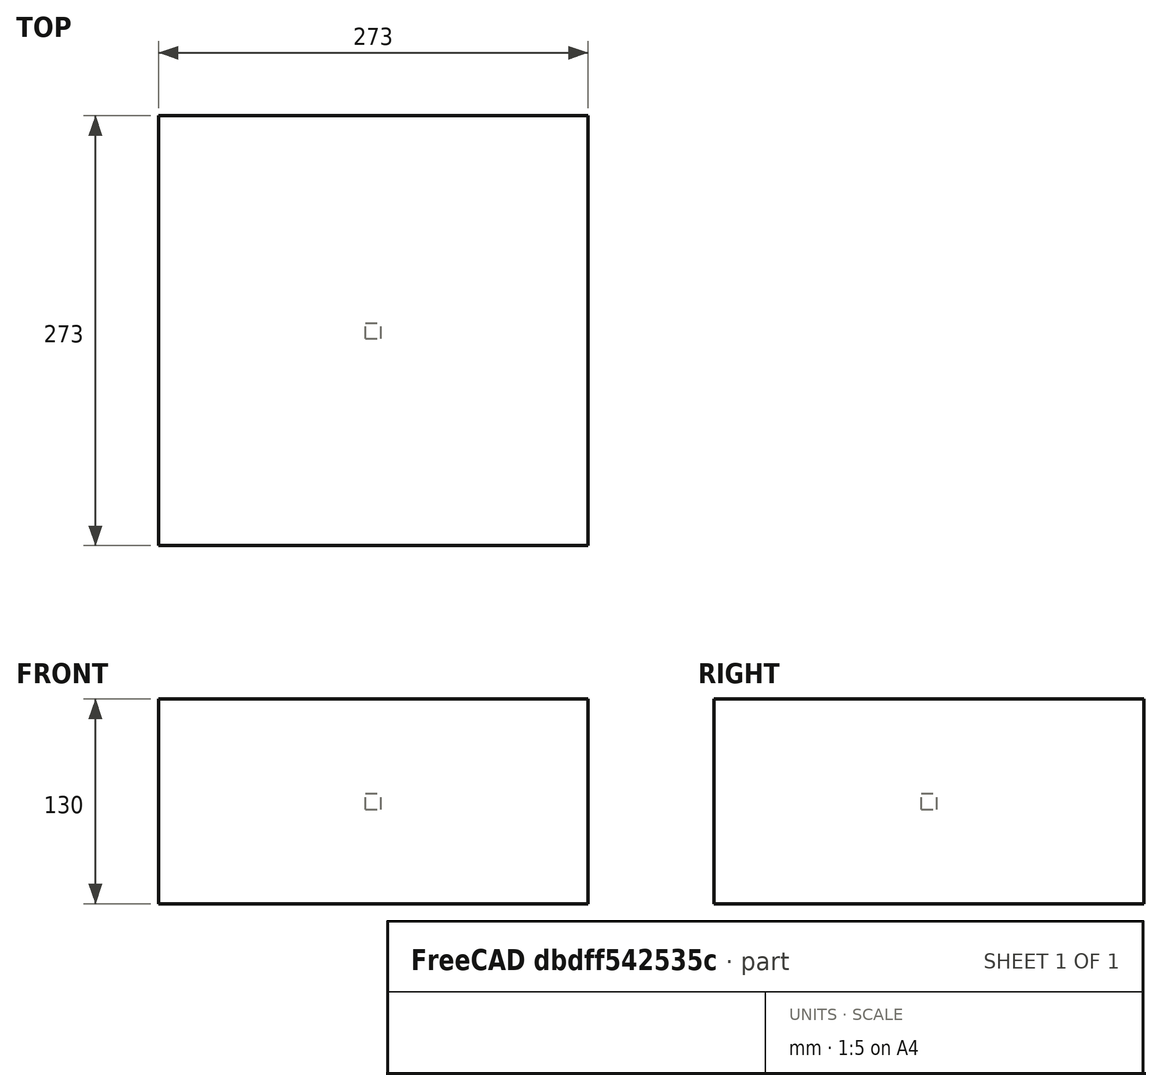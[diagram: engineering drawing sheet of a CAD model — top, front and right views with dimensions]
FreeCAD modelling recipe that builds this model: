
FCSTD DOCUMENT  (FreeCAD 0.20R29603 (Git))
Label: polarArray
License: All rights reserved
LicenseURL: http://en.wikipedia.org/wiki/All_rights_reserved
objects: App::DocumentObjectGroupPython×1251, Part::FeaturePython×3, App::Part×3
note: 2 computed .brp shape members not serialized (recipe doc carries the construction recipe); baked Part::Feature solids carry a one-line shape summary decoded from their .brp

FEATURE [App::DocumentObjectGroupPython] HALFPI  # scripted group (container) (typed FeaturePython)
  name = HALFPI
  value = pi/2.
FEATURE [App::DocumentObjectGroupPython] PI  # scripted group (container) (typed FeaturePython)
  name = PI
  value = 1.*pi
FEATURE [App::DocumentObjectGroupPython] TWOPI  # scripted group (container) (typed FeaturePython)
  name = TWOPI
  value = 2.*pi
FEATURE [App::DocumentObjectGroupPython] Constants  # scripted group (container) (typed FeaturePython)
  Group = -> [HALFPI,PI,TWOPI]
FEATURE [App::DocumentObjectGroupPython] Variables  # scripted group (container) (typed FeaturePython)
FEATURE [App::DocumentObjectGroupPython] Quantities  # scripted group (container) (typed FeaturePython)
FEATURE [App::DocumentObjectGroupPython] Isotopes  # scripted group (container) (typed FeaturePython)
FEATURE [App::DocumentObjectGroupPython] Elements  # scripted group (container) (typed FeaturePython)
FEATURE [App::DocumentObjectGroupPython] Matrix  # scripted group (container) (typed FeaturePython)
FEATURE [App::DocumentObjectGroupPython] Surfaces  # scripted group (container) (typed FeaturePython)
FEATURE [App::DocumentObjectGroupPython] Opticals  # scripted group (container) (typed FeaturePython)
  Group = -> [Matrix,Surfaces]
FEATURE [App::DocumentObjectGroupPython] G4Isotopes  # scripted group (container) (typed FeaturePython)
FEATURE [App::DocumentObjectGroupPython] H_element  # scripted group (container) (typed FeaturePython)
  Z = 1
  atom_value = 1.008
  formula = H
  name = H_element
FEATURE [App::DocumentObjectGroupPython] He_element  # scripted group (container) (typed FeaturePython)
  Z = 2
  atom_value = 4.0026
  formula = He
  name = He_element
FEATURE [App::DocumentObjectGroupPython] Li_element  # scripted group (container) (typed FeaturePython)
  Z = 3
  atom_value = 6.94
  formula = Li
  name = Li_element
FEATURE [App::DocumentObjectGroupPython] Be_element  # scripted group (container) (typed FeaturePython)
  Z = 4
  atom_value = 9.01218
  formula = Be
  name = Be_element
FEATURE [App::DocumentObjectGroupPython] B_element  # scripted group (container) (typed FeaturePython)
  Z = 5
  atom_value = 10.81
  formula = B
  name = B_element
FEATURE [App::DocumentObjectGroupPython] C_element  # scripted group (container) (typed FeaturePython)
  Z = 6
  atom_value = 12.011
  formula = C
  name = C_element
FEATURE [App::DocumentObjectGroupPython] N_element  # scripted group (container) (typed FeaturePython)
  Z = 7
  atom_value = 14.007
  formula = N
  name = N_element
FEATURE [App::DocumentObjectGroupPython] O_element  # scripted group (container) (typed FeaturePython)
  Z = 8
  atom_value = 15.999
  formula = O
  name = O_element
FEATURE [App::DocumentObjectGroupPython] F_element  # scripted group (container) (typed FeaturePython)
  Z = 9
  atom_value = 18.9984
  formula = F
  name = F_element
FEATURE [App::DocumentObjectGroupPython] Ne_element  # scripted group (container) (typed FeaturePython)
  Z = 10
  atom_value = 20.1797
  formula = Ne
  name = Ne_element
FEATURE [App::DocumentObjectGroupPython] Na_element  # scripted group (container) (typed FeaturePython)
  Z = 11
  atom_value = 22.9898
  formula = Na
  name = Na_element
FEATURE [App::DocumentObjectGroupPython] Mg_element  # scripted group (container) (typed FeaturePython)
  Z = 12
  atom_value = 24.305
  formula = Mg
  name = Mg_element
FEATURE [App::DocumentObjectGroupPython] Al_element  # scripted group (container) (typed FeaturePython)
  Z = 13
  atom_value = 26.9815
  formula = Al
  name = Al_element
FEATURE [App::DocumentObjectGroupPython] Si_element  # scripted group (container) (typed FeaturePython)
  Z = 14
  atom_value = 28.085
  formula = Si
  name = Si_element
FEATURE [App::DocumentObjectGroupPython] P_element  # scripted group (container) (typed FeaturePython)
  Z = 15
  atom_value = 30.9738
  formula = P
  name = P_element
FEATURE [App::DocumentObjectGroupPython] S_element  # scripted group (container) (typed FeaturePython)
  Z = 16
  atom_value = 32.06
  formula = S
  name = S_element
FEATURE [App::DocumentObjectGroupPython] Cl_element  # scripted group (container) (typed FeaturePython)
  Z = 17
  atom_value = 35.45
  formula = Cl
  name = Cl_element
FEATURE [App::DocumentObjectGroupPython] Ar_element  # scripted group (container) (typed FeaturePython)
  Z = 18
  atom_value = 39.95
  formula = Ar
  name = Ar_element
FEATURE [App::DocumentObjectGroupPython] K_element  # scripted group (container) (typed FeaturePython)
  Z = 19
  atom_value = 39.0983
  formula = K
  name = K_element
FEATURE [App::DocumentObjectGroupPython] Ca_element  # scripted group (container) (typed FeaturePython)
  Z = 20
  atom_value = 40.078
  formula = Ca
  name = Ca_element
FEATURE [App::DocumentObjectGroupPython] Sc_element  # scripted group (container) (typed FeaturePython)
  Z = 21
  atom_value = 44.9559
  formula = Sc
  name = Sc_element
FEATURE [App::DocumentObjectGroupPython] Ti_element  # scripted group (container) (typed FeaturePython)
  Z = 22
  atom_value = 47.867
  formula = Ti
  name = Ti_element
FEATURE [App::DocumentObjectGroupPython] V_element  # scripted group (container) (typed FeaturePython)
  Z = 23
  atom_value = 50.9415
  formula = V
  name = V_element
FEATURE [App::DocumentObjectGroupPython] Cr_element  # scripted group (container) (typed FeaturePython)
  Z = 24
  atom_value = 51.9961
  formula = Cr
  name = Cr_element
FEATURE [App::DocumentObjectGroupPython] Mn_element  # scripted group (container) (typed FeaturePython)
  Z = 25
  atom_value = 54.938
  formula = Mn
  name = Mn_element
FEATURE [App::DocumentObjectGroupPython] Fe_element  # scripted group (container) (typed FeaturePython)
  Z = 26
  atom_value = 55.845
  formula = Fe
  name = Fe_element
FEATURE [App::DocumentObjectGroupPython] Co_element  # scripted group (container) (typed FeaturePython)
  Z = 27
  atom_value = 58.9332
  formula = Co
  name = Co_element
FEATURE [App::DocumentObjectGroupPython] Ni_element  # scripted group (container) (typed FeaturePython)
  Z = 28
  atom_value = 58.6934
  formula = Ni
  name = Ni_element
FEATURE [App::DocumentObjectGroupPython] Cu_element  # scripted group (container) (typed FeaturePython)
  Z = 29
  atom_value = 63.546
  formula = Cu
  name = Cu_element
FEATURE [App::DocumentObjectGroupPython] Zn_element  # scripted group (container) (typed FeaturePython)
  Z = 30
  atom_value = 65.38
  formula = Zn
  name = Zn_element
FEATURE [App::DocumentObjectGroupPython] Ga_element  # scripted group (container) (typed FeaturePython)
  Z = 31
  atom_value = 69.723
  formula = Ga
  name = Ga_element
FEATURE [App::DocumentObjectGroupPython] Ge_element  # scripted group (container) (typed FeaturePython)
  Z = 32
  atom_value = 72.63
  formula = Ge
  name = Ge_element
FEATURE [App::DocumentObjectGroupPython] As_element  # scripted group (container) (typed FeaturePython)
  Z = 33
  atom_value = 74.9216
  formula = As
  name = As_element
FEATURE [App::DocumentObjectGroupPython] Se_element  # scripted group (container) (typed FeaturePython)
  Z = 34
  atom_value = 78.971
  formula = Se
  name = Se_element
FEATURE [App::DocumentObjectGroupPython] Br_element  # scripted group (container) (typed FeaturePython)
  Z = 35
  atom_value = 79.904
  formula = Br
  name = Br_element
FEATURE [App::DocumentObjectGroupPython] Kr_element  # scripted group (container) (typed FeaturePython)
  Z = 36
  atom_value = 83.798
  formula = Kr
  name = Kr_element
FEATURE [App::DocumentObjectGroupPython] Rb_element  # scripted group (container) (typed FeaturePython)
  Z = 37
  atom_value = 85.4678
  formula = Rb
  name = Rb_element
FEATURE [App::DocumentObjectGroupPython] Sr_element  # scripted group (container) (typed FeaturePython)
  Z = 38
  atom_value = 87.62
  formula = Sr
  name = Sr_element
FEATURE [App::DocumentObjectGroupPython] Y_element  # scripted group (container) (typed FeaturePython)
  Z = 39
  atom_value = 88.9058
  formula = Y
  name = Y_element
FEATURE [App::DocumentObjectGroupPython] Zr_element  # scripted group (container) (typed FeaturePython)
  Z = 40
  atom_value = 91.224
  formula = Zr
  name = Zr_element
FEATURE [App::DocumentObjectGroupPython] Nb_element  # scripted group (container) (typed FeaturePython)
  Z = 41
  atom_value = 92.9064
  formula = Nb
  name = Nb_element
FEATURE [App::DocumentObjectGroupPython] Mo_element  # scripted group (container) (typed FeaturePython)
  Z = 42
  atom_value = 95.95
  formula = Mo
  name = Mo_element
FEATURE [App::DocumentObjectGroupPython] Tc_element  # scripted group (container) (typed FeaturePython)
  Z = 43
  atom_value = 97
  formula = Tc
  name = Tc_element
FEATURE [App::DocumentObjectGroupPython] Ru_element  # scripted group (container) (typed FeaturePython)
  Z = 44
  atom_value = 101.07
  formula = Ru
  name = Ru_element
FEATURE [App::DocumentObjectGroupPython] Rh_element  # scripted group (container) (typed FeaturePython)
  Z = 45
  atom_value = 102.905
  formula = Rh
  name = Rh_element
FEATURE [App::DocumentObjectGroupPython] Pd_element  # scripted group (container) (typed FeaturePython)
  Z = 46
  atom_value = 106.42
  formula = Pd
  name = Pd_element
FEATURE [App::DocumentObjectGroupPython] Ag_element  # scripted group (container) (typed FeaturePython)
  Z = 47
  atom_value = 107.868
  formula = Ag
  name = Ag_element
FEATURE [App::DocumentObjectGroupPython] Cd_element  # scripted group (container) (typed FeaturePython)
  Z = 48
  atom_value = 112.414
  formula = Cd
  name = Cd_element
FEATURE [App::DocumentObjectGroupPython] In_element  # scripted group (container) (typed FeaturePython)
  Z = 49
  atom_value = 114.818
  formula = In
  name = In_element
FEATURE [App::DocumentObjectGroupPython] Sn_element  # scripted group (container) (typed FeaturePython)
  Z = 50
  atom_value = 118.71
  formula = Sn
  name = Sn_element
FEATURE [App::DocumentObjectGroupPython] Sb_element  # scripted group (container) (typed FeaturePython)
  Z = 51
  atom_value = 121.76
  formula = Sb
  name = Sb_element
FEATURE [App::DocumentObjectGroupPython] Te_element  # scripted group (container) (typed FeaturePython)
  Z = 52
  atom_value = 127.6
  formula = Te
  name = Te_element
FEATURE [App::DocumentObjectGroupPython] I_element  # scripted group (container) (typed FeaturePython)
  Z = 53
  atom_value = 126.904
  formula = I
  name = I_element
FEATURE [App::DocumentObjectGroupPython] Xe_element  # scripted group (container) (typed FeaturePython)
  Z = 54
  atom_value = 131.293
  formula = Xe
  name = Xe_element
FEATURE [App::DocumentObjectGroupPython] Cs_element  # scripted group (container) (typed FeaturePython)
  Z = 55
  atom_value = 132.905
  formula = Cs
  name = Cs_element
FEATURE [App::DocumentObjectGroupPython] Ba_element  # scripted group (container) (typed FeaturePython)
  Z = 56
  atom_value = 137.327
  formula = Ba
  name = Ba_element
FEATURE [App::DocumentObjectGroupPython] La_element  # scripted group (container) (typed FeaturePython)
  Z = 57
  atom_value = 138.905
  formula = La
  name = La_element
FEATURE [App::DocumentObjectGroupPython] Ce_element  # scripted group (container) (typed FeaturePython)
  Z = 58
  atom_value = 140.116
  formula = Ce
  name = Ce_element
FEATURE [App::DocumentObjectGroupPython] Pr_element  # scripted group (container) (typed FeaturePython)
  Z = 59
  atom_value = 140.908
  formula = Pr
  name = Pr_element
FEATURE [App::DocumentObjectGroupPython] Nd_element  # scripted group (container) (typed FeaturePython)
  Z = 60
  atom_value = 144.242
  formula = Nd
  name = Nd_element
FEATURE [App::DocumentObjectGroupPython] Pm_element  # scripted group (container) (typed FeaturePython)
  Z = 61
  atom_value = 145
  formula = Pm
  name = Pm_element
FEATURE [App::DocumentObjectGroupPython] Sm_element  # scripted group (container) (typed FeaturePython)
  Z = 62
  atom_value = 150.36
  formula = Sm
  name = Sm_element
FEATURE [App::DocumentObjectGroupPython] Eu_element  # scripted group (container) (typed FeaturePython)
  Z = 63
  atom_value = 151.964
  formula = Eu
  name = Eu_element
FEATURE [App::DocumentObjectGroupPython] Gd_element  # scripted group (container) (typed FeaturePython)
  Z = 64
  atom_value = 157.25
  formula = Gd
  name = Gd_element
FEATURE [App::DocumentObjectGroupPython] Tb_element  # scripted group (container) (typed FeaturePython)
  Z = 65
  atom_value = 158.925
  formula = Tb
  name = Tb_element
FEATURE [App::DocumentObjectGroupPython] Dy_element  # scripted group (container) (typed FeaturePython)
  Z = 66
  atom_value = 162.5
  formula = Dy
  name = Dy_element
FEATURE [App::DocumentObjectGroupPython] Ho_element  # scripted group (container) (typed FeaturePython)
  Z = 67
  atom_value = 164.93
  formula = Ho
  name = Ho_element
FEATURE [App::DocumentObjectGroupPython] Er_element  # scripted group (container) (typed FeaturePython)
  Z = 68
  atom_value = 167.259
  formula = Er
  name = Er_element
FEATURE [App::DocumentObjectGroupPython] Tm_element  # scripted group (container) (typed FeaturePython)
  Z = 69
  atom_value = 168.934
  formula = Tm
  name = Tm_element
FEATURE [App::DocumentObjectGroupPython] Yb_element  # scripted group (container) (typed FeaturePython)
  Z = 70
  atom_value = 173.045
  formula = Yb
  name = Yb_element
FEATURE [App::DocumentObjectGroupPython] Lu_element  # scripted group (container) (typed FeaturePython)
  Z = 71
  atom_value = 174.967
  formula = Lu
  name = Lu_element
FEATURE [App::DocumentObjectGroupPython] Hf_element  # scripted group (container) (typed FeaturePython)
  Z = 72
  atom_value = 178.49
  formula = Hf
  name = Hf_element
FEATURE [App::DocumentObjectGroupPython] Ta_element  # scripted group (container) (typed FeaturePython)
  Z = 73
  atom_value = 180.948
  formula = Ta
  name = Ta_element
FEATURE [App::DocumentObjectGroupPython] W_element  # scripted group (container) (typed FeaturePython)
  Z = 74
  atom_value = 183.84
  formula = W
  name = W_element
FEATURE [App::DocumentObjectGroupPython] Re_element  # scripted group (container) (typed FeaturePython)
  Z = 75
  atom_value = 186.207
  formula = Re
  name = Re_element
FEATURE [App::DocumentObjectGroupPython] Os_element  # scripted group (container) (typed FeaturePython)
  Z = 76
  atom_value = 190.23
  formula = Os
  name = Os_element
FEATURE [App::DocumentObjectGroupPython] Ir_element  # scripted group (container) (typed FeaturePython)
  Z = 77
  atom_value = 192.217
  formula = Ir
  name = Ir_element
FEATURE [App::DocumentObjectGroupPython] Pt_element  # scripted group (container) (typed FeaturePython)
  Z = 78
  atom_value = 195.084
  formula = Pt
  name = Pt_element
FEATURE [App::DocumentObjectGroupPython] Au_element  # scripted group (container) (typed FeaturePython)
  Z = 79
  atom_value = 196.967
  formula = Au
  name = Au_element
FEATURE [App::DocumentObjectGroupPython] Hg_element  # scripted group (container) (typed FeaturePython)
  Z = 80
  atom_value = 200.592
  formula = Hg
  name = Hg_element
FEATURE [App::DocumentObjectGroupPython] Tl_element  # scripted group (container) (typed FeaturePython)
  Z = 81
  atom_value = 204.38
  formula = Tl
  name = Tl_element
FEATURE [App::DocumentObjectGroupPython] Pb_element  # scripted group (container) (typed FeaturePython)
  Z = 82
  atom_value = 207.2
  formula = Pb
  name = Pb_element
FEATURE [App::DocumentObjectGroupPython] Bi_element  # scripted group (container) (typed FeaturePython)
  Z = 83
  atom_value = 208.98
  formula = Bi
  name = Bi_element
FEATURE [App::DocumentObjectGroupPython] Po_element  # scripted group (container) (typed FeaturePython)
  Z = 84
  atom_value = 209
  formula = Po
  name = Po_element
FEATURE [App::DocumentObjectGroupPython] At_element  # scripted group (container) (typed FeaturePython)
  Z = 85
  atom_value = 210
  formula = At
  name = At_element
FEATURE [App::DocumentObjectGroupPython] Rn_element  # scripted group (container) (typed FeaturePython)
  Z = 86
  atom_value = 222
  formula = Rn
  name = Rn_element
FEATURE [App::DocumentObjectGroupPython] Fr_element  # scripted group (container) (typed FeaturePython)
  Z = 87
  atom_value = 223
  formula = Fr
  name = Fr_element
FEATURE [App::DocumentObjectGroupPython] Ra_element  # scripted group (container) (typed FeaturePython)
  Z = 88
  atom_value = 226
  formula = Ra
  name = Ra_element
FEATURE [App::DocumentObjectGroupPython] Ac_element  # scripted group (container) (typed FeaturePython)
  Z = 89
  atom_value = 227
  formula = Ac
  name = Ac_element
FEATURE [App::DocumentObjectGroupPython] Th_element  # scripted group (container) (typed FeaturePython)
  Z = 90
  atom_value = 232.038
  formula = Th
  name = Th_element
FEATURE [App::DocumentObjectGroupPython] Pa_element  # scripted group (container) (typed FeaturePython)
  Z = 91
  atom_value = 231.036
  formula = Pa
  name = Pa_element
FEATURE [App::DocumentObjectGroupPython] U_element  # scripted group (container) (typed FeaturePython)
  Z = 92
  atom_value = 238.029
  formula = U
  name = U_element
FEATURE [App::DocumentObjectGroupPython] Np_element  # scripted group (container) (typed FeaturePython)
  Z = 93
  atom_value = 237
  formula = Np
  name = Np_element
FEATURE [App::DocumentObjectGroupPython] Pu_element  # scripted group (container) (typed FeaturePython)
  Z = 94
  atom_value = 244
  formula = Pu
  name = Pu_element
FEATURE [App::DocumentObjectGroupPython] Am_element  # scripted group (container) (typed FeaturePython)
  Z = 95
  atom_value = 243
  formula = Am
  name = Am_element
FEATURE [App::DocumentObjectGroupPython] Cm_element  # scripted group (container) (typed FeaturePython)
  Z = 96
  atom_value = 247
  formula = Cm
  name = Cm_element
FEATURE [App::DocumentObjectGroupPython] Bk_element  # scripted group (container) (typed FeaturePython)
  Z = 97
  atom_value = 247
  formula = Bk
  name = Bk_element
FEATURE [App::DocumentObjectGroupPython] Cf_element  # scripted group (container) (typed FeaturePython)
  Z = 98
  atom_value = 251
  formula = Cf
  name = Cf_element
FEATURE [App::DocumentObjectGroupPython] G4Elements  # scripted group (container) (typed FeaturePython)
  Group = -> [H_element,He_element,Li_element,Be_element,B_element,C_element,N_element,O_element,F_element,Ne_element,Na_element,Mg_element,Al_element,Si_element,P_element,S_element,Cl_element,Ar_element,K_element,Ca_element,Sc_element,Ti_element,V_element,Cr_element,Mn_element,Fe_element,Co_element,Ni_element,Cu_element,Zn_element,Ga_element,Ge_element,As_element,Se_element,Br_element,Kr_element,Rb_element,+61 more]
FEATURE [App::DocumentObjectGroupPython] H_element001  label="H_element : 0.101"  # scripted group (container) (typed FeaturePython)
  n = 0.101327
FEATURE [App::DocumentObjectGroupPython] C_element001  label="C_element : 0.775"  # scripted group (container) (typed FeaturePython)
  n = 0.7755
FEATURE [App::DocumentObjectGroupPython] N_element001  label="N_element : 0.035"  # scripted group (container) (typed FeaturePython)
  n = 0.035057
FEATURE [App::DocumentObjectGroupPython] O_element001  label="O_element : 0.052"  # scripted group (container) (typed FeaturePython)
  n = 0.0523159
FEATURE [App::DocumentObjectGroupPython] F_element001  label="F_element : 0.017"  # scripted group (container) (typed FeaturePython)
  n = 0.017422
FEATURE [App::DocumentObjectGroupPython] Ca_element001  label="Ca_element : 0.018"  # scripted group (container) (typed FeaturePython)
  n = 0.018378
FEATURE [App::DocumentObjectGroupPython] G4_A_150_TISSUE  label="G4_A-150_TISSUE"  # scripted group (container) (typed FeaturePython)
  Dunit = g/cm3
  Dvalue = 1.127
  Group = -> [H_element001,C_element001,N_element001,O_element001,F_element001,Ca_element001]
  conduct = 2
  density = 1
  expand = 3
  formula = G4_A-150_TISSUE
  name = G4_A-150_TISSUE
  specific = 4
FEATURE [App::DocumentObjectGroupPython] C_element002  label="C_element : 3"  # scripted group (container) (typed FeaturePython)
  n = 3
  ref = C_element
FEATURE [App::DocumentObjectGroupPython] H_element002  label="H_element : 6"  # scripted group (container) (typed FeaturePython)
  n = 6
  ref = H_element
FEATURE [App::DocumentObjectGroupPython] O_element002  label="O_element : 1"  # scripted group (container) (typed FeaturePython)
  n = 1
  ref = O_element
FEATURE [App::DocumentObjectGroupPython] G4_ACETONE  # scripted group (container) (typed FeaturePython)
  Dunit = g/cm3
  Dvalue = 0.7899
  Group = -> [C_element002,H_element002,O_element002]
  conduct = 2
  density = 1
  expand = 3
  formula = G4_ACETONE
  name = G4_ACETONE
  specific = 4
FEATURE [App::DocumentObjectGroupPython] C_element003  label="C_element : 2"  # scripted group (container) (typed FeaturePython)
  n = 2
  ref = C_element
FEATURE [App::DocumentObjectGroupPython] H_element003  label="H_element : 2"  # scripted group (container) (typed FeaturePython)
  n = 2
  ref = H_element
FEATURE [App::DocumentObjectGroupPython] G4_ACETYLENE  # scripted group (container) (typed FeaturePython)
  Dunit = g/cm3
  Dvalue = 0.0010967
  Group = -> [C_element003,H_element003]
  conduct = 2
  density = 1
  expand = 3
  formula = G4_ACETYLENE
  name = G4_ACETYLENE
  specific = 4
FEATURE [App::DocumentObjectGroupPython] C_element004  label="C_element : 5"  # scripted group (container) (typed FeaturePython)
  n = 5
  ref = C_element
FEATURE [App::DocumentObjectGroupPython] H_element004  label="H_element : 5"  # scripted group (container) (typed FeaturePython)
  n = 5
  ref = H_element
FEATURE [App::DocumentObjectGroupPython] N_element002  label="N_element : 5"  # scripted group (container) (typed FeaturePython)
  n = 5
  ref = N_element
FEATURE [App::DocumentObjectGroupPython] G4_ADENINE  # scripted group (container) (typed FeaturePython)
  Dunit = g/cm3
  Dvalue = 1.6
  Group = -> [C_element004,H_element004,N_element002]
  conduct = 2
  density = 1
  expand = 3
  formula = G4_ADENINE
  name = G4_ADENINE
  specific = 4
FEATURE [App::DocumentObjectGroupPython] H_element005  label="H_element : 0.114"  # scripted group (container) (typed FeaturePython)
  n = 0.114
FEATURE [App::DocumentObjectGroupPython] C_element005  label="C_element : 0.598"  # scripted group (container) (typed FeaturePython)
  n = 0.598
FEATURE [App::DocumentObjectGroupPython] N_element003  label="N_element : 0.007"  # scripted group (container) (typed FeaturePython)
  n = 0.007
FEATURE [App::DocumentObjectGroupPython] O_element003  label="O_element : 0.278"  # scripted group (container) (typed FeaturePython)
  n = 0.278
FEATURE [App::DocumentObjectGroupPython] Na_element001  label="Na_element : 0.001"  # scripted group (container) (typed FeaturePython)
  n = 0.001
FEATURE [App::DocumentObjectGroupPython] S_element001  label="S_element : 0.001"  # scripted group (container) (typed FeaturePython)
  n = 0.001
FEATURE [App::DocumentObjectGroupPython] Cl_element001  label="Cl_element : 0.001"  # scripted group (container) (typed FeaturePython)
  n = 0.001
FEATURE [App::DocumentObjectGroupPython] G4_ADIPOSE_TISSUE_ICRP  # scripted group (container) (typed FeaturePython)
  Dunit = g/cm3
  Dvalue = 0.95
  Group = -> [H_element005,C_element005,N_element003,O_element003,Na_element001,S_element001,Cl_element001]
  conduct = 2
  density = 1
  expand = 3
  formula = G4_ADIPOSE_TISSUE_ICRP
  name = G4_ADIPOSE_TISSUE_ICRP
  specific = 4
FEATURE [App::DocumentObjectGroupPython] C_element006  label="C_element : 0.000"  # scripted group (container) (typed FeaturePython)
  n = 0.000124
FEATURE [App::DocumentObjectGroupPython] N_element004  label="N_element : 0.755"  # scripted group (container) (typed FeaturePython)
  n = 0.755268
FEATURE [App::DocumentObjectGroupPython] O_element004  label="O_element : 0.232"  # scripted group (container) (typed FeaturePython)
  n = 0.231781
FEATURE [App::DocumentObjectGroupPython] Ar_element001  label="Ar_element : 0.013"  # scripted group (container) (typed FeaturePython)
  n = 0.012827
FEATURE [App::DocumentObjectGroupPython] G4_AIR  # scripted group (container) (typed FeaturePython)
  Dunit = g/cm3
  Dvalue = 0.00120479
  Group = -> [C_element006,N_element004,O_element004,Ar_element001]
  conduct = 2
  density = 1
  expand = 3
  formula = G4_AIR
  name = G4_AIR
  specific = 4
FEATURE [App::DocumentObjectGroupPython] C_element007  label="C_element : 006"  # scripted group (container) (typed FeaturePython)
  n = 3
  ref = C_element
FEATURE [App::DocumentObjectGroupPython] H_element006  label="H_element : 7"  # scripted group (container) (typed FeaturePython)
  n = 7
  ref = H_element
FEATURE [App::DocumentObjectGroupPython] N_element005  label="N_element : 1"  # scripted group (container) (typed FeaturePython)
  n = 1
  ref = N_element
FEATURE [App::DocumentObjectGroupPython] O_element005  label="O_element : 2"  # scripted group (container) (typed FeaturePython)
  n = 2
  ref = O_element
FEATURE [App::DocumentObjectGroupPython] G4_ALANINE  # scripted group (container) (typed FeaturePython)
  Dunit = g/cm3
  Dvalue = 1.42
  Group = -> [C_element007,H_element006,N_element005,O_element005]
  conduct = 2
  density = 1
  expand = 3
  formula = G4_ALANINE
  name = G4_ALANINE
  specific = 4
FEATURE [App::DocumentObjectGroupPython] Al_element001  label="Al_element : 2"  # scripted group (container) (typed FeaturePython)
  n = 2
  ref = Al_element
FEATURE [App::DocumentObjectGroupPython] O_element006  label="O_element : 3"  # scripted group (container) (typed FeaturePython)
  n = 3
  ref = O_element
FEATURE [App::DocumentObjectGroupPython] G4_ALUMINUM_OXIDE  # scripted group (container) (typed FeaturePython)
  Dunit = g/cm3
  Dvalue = 3.97
  Group = -> [Al_element001,O_element006]
  conduct = 2
  density = 1
  expand = 3
  formula = G4_ALUMINUM_OXIDE
  name = G4_ALUMINUM_OXIDE
  specific = 4
FEATURE [App::DocumentObjectGroupPython] H_element007  label="H_element : 0.106"  # scripted group (container) (typed FeaturePython)
  n = 0.10593
FEATURE [App::DocumentObjectGroupPython] C_element008  label="C_element : 0.789"  # scripted group (container) (typed FeaturePython)
  n = 0.788974
FEATURE [App::DocumentObjectGroupPython] O_element007  label="O_element : 0.105"  # scripted group (container) (typed FeaturePython)
  n = 0.105096
FEATURE [App::DocumentObjectGroupPython] G4_AMBER  # scripted group (container) (typed FeaturePython)
  Dunit = g/cm3
  Dvalue = 1.1
  Group = -> [H_element007,C_element008,O_element007]
  conduct = 2
  density = 1
  expand = 3
  formula = G4_AMBER
  name = G4_AMBER
  specific = 4
FEATURE [App::DocumentObjectGroupPython] N_element006  label="N_element : 006"  # scripted group (container) (typed FeaturePython)
  n = 1
  ref = N_element
FEATURE [App::DocumentObjectGroupPython] H_element008  label="H_element : 3"  # scripted group (container) (typed FeaturePython)
  n = 3
  ref = H_element
FEATURE [App::DocumentObjectGroupPython] G4_AMMONIA  # scripted group (container) (typed FeaturePython)
  Dunit = g/cm3
  Dvalue = 0.000826019
  Group = -> [N_element006,H_element008]
  conduct = 2
  density = 1
  expand = 3
  formula = G4_AMMONIA
  name = G4_AMMONIA
  specific = 4
FEATURE [App::DocumentObjectGroupPython] C_element009  label="C_element : 6"  # scripted group (container) (typed FeaturePython)
  n = 6
  ref = C_element
FEATURE [App::DocumentObjectGroupPython] H_element009  label="H_element : 008"  # scripted group (container) (typed FeaturePython)
  n = 7
  ref = H_element
FEATURE [App::DocumentObjectGroupPython] N_element007  label="N_element : 007"  # scripted group (container) (typed FeaturePython)
  n = 1
  ref = N_element
FEATURE [App::DocumentObjectGroupPython] G4_ANILINE  # scripted group (container) (typed FeaturePython)
  Dunit = g/cm3
  Dvalue = 1.0235
  Group = -> [C_element009,H_element009,N_element007]
  conduct = 2
  density = 1
  expand = 3
  formula = G4_ANILINE
  name = G4_ANILINE
  specific = 4
FEATURE [App::DocumentObjectGroupPython] C_element010  label="C_element : 14"  # scripted group (container) (typed FeaturePython)
  n = 14
  ref = C_element
FEATURE [App::DocumentObjectGroupPython] H_element010  label="H_element : 10"  # scripted group (container) (typed FeaturePython)
  n = 10
  ref = H_element
FEATURE [App::DocumentObjectGroupPython] G4_ANTHRACENE  # scripted group (container) (typed FeaturePython)
  Dunit = g/cm3
  Dvalue = 1.283
  Group = -> [C_element010,H_element010]
  conduct = 2
  density = 1
  expand = 3
  formula = G4_ANTHRACENE
  name = G4_ANTHRACENE
  specific = 4
FEATURE [App::DocumentObjectGroupPython] H_element011  label="H_element : 0.065"  # scripted group (container) (typed FeaturePython)
  n = 0.0654709
FEATURE [App::DocumentObjectGroupPython] C_element011  label="C_element : 0.537"  # scripted group (container) (typed FeaturePython)
  n = 0.536944
FEATURE [App::DocumentObjectGroupPython] N_element008  label="N_element : 0.021"  # scripted group (container) (typed FeaturePython)
  n = 0.0215
FEATURE [App::DocumentObjectGroupPython] O_element008  label="O_element : 0.032"  # scripted group (container) (typed FeaturePython)
  n = 0.032085
FEATURE [App::DocumentObjectGroupPython] F_element002  label="F_element : 0.167"  # scripted group (container) (typed FeaturePython)
  n = 0.167411
FEATURE [App::DocumentObjectGroupPython] Ca_element002  label="Ca_element : 0.177"  # scripted group (container) (typed FeaturePython)
  n = 0.176589
FEATURE [App::DocumentObjectGroupPython] G4_B_100_BONE  label="G4_B-100_BONE"  # scripted group (container) (typed FeaturePython)
  Dunit = g/cm3
  Dvalue = 1.45
  Group = -> [H_element011,C_element011,N_element008,O_element008,F_element002,Ca_element002]
  conduct = 2
  density = 1
  expand = 3
  formula = G4_B-100_BONE
  name = G4_B-100_BONE
  specific = 4
FEATURE [App::DocumentObjectGroupPython] H_element012  label="H_element : 0.057"  # scripted group (container) (typed FeaturePython)
  n = 0.057441
FEATURE [App::DocumentObjectGroupPython] C_element012  label="C_element : 0.790"  # scripted group (container) (typed FeaturePython)
  n = 0.774591
FEATURE [App::DocumentObjectGroupPython] O_element009  label="O_element : 0.168"  # scripted group (container) (typed FeaturePython)
  n = 0.167968
FEATURE [App::DocumentObjectGroupPython] G4_BAKELITE  # scripted group (container) (typed FeaturePython)
  Dunit = g/cm3
  Dvalue = 1.25
  Group = -> [H_element012,C_element012,O_element009]
  conduct = 2
  density = 1
  expand = 3
  formula = G4_BAKELITE
  name = G4_BAKELITE
  specific = 4
FEATURE [App::DocumentObjectGroupPython] Ba_element001  label="Ba_element : 1"  # scripted group (container) (typed FeaturePython)
  n = 1
  ref = Ba_element
FEATURE [App::DocumentObjectGroupPython] F_element003  label="F_element : 2"  # scripted group (container) (typed FeaturePython)
  n = 2
  ref = F_element
FEATURE [App::DocumentObjectGroupPython] G4_BARIUM_FLUORIDE  # scripted group (container) (typed FeaturePython)
  Dunit = g/cm3
  Dvalue = 4.89
  Group = -> [Ba_element001,F_element003]
  conduct = 2
  density = 1
  expand = 3
  formula = G4_BARIUM_FLUORIDE
  name = G4_BARIUM_FLUORIDE
  specific = 4
FEATURE [App::DocumentObjectGroupPython] Ba_element002  label="Ba_element : 002"  # scripted group (container) (typed FeaturePython)
  n = 1
  ref = Ba_element
FEATURE [App::DocumentObjectGroupPython] S_element002  label="S_element : 1"  # scripted group (container) (typed FeaturePython)
  n = 1
  ref = S_element
FEATURE [App::DocumentObjectGroupPython] O_element010  label="O_element : 4"  # scripted group (container) (typed FeaturePython)
  n = 4
  ref = O_element
FEATURE [App::DocumentObjectGroupPython] G4_BARIUM_SULFATE  # scripted group (container) (typed FeaturePython)
  Dunit = g/cm3
  Dvalue = 4.5
  Group = -> [Ba_element002,S_element002,O_element010]
  conduct = 2
  density = 1
  expand = 3
  formula = G4_BARIUM_SULFATE
  name = G4_BARIUM_SULFATE
  specific = 4
FEATURE [App::DocumentObjectGroupPython] C_element013  label="C_element : 007"  # scripted group (container) (typed FeaturePython)
  n = 6
  ref = C_element
FEATURE [App::DocumentObjectGroupPython] H_element013  label="H_element : 009"  # scripted group (container) (typed FeaturePython)
  n = 6
  ref = H_element
FEATURE [App::DocumentObjectGroupPython] G4_BENZENE  # scripted group (container) (typed FeaturePython)
  Dunit = g/cm3
  Dvalue = 0.87865
  Group = -> [C_element013,H_element013]
  conduct = 2
  density = 1
  expand = 3
  formula = G4_BENZENE
  name = G4_BENZENE
  specific = 4
FEATURE [App::DocumentObjectGroupPython] Be_element001  label="Be_element : 1"  # scripted group (container) (typed FeaturePython)
  n = 1
  ref = Be_element
FEATURE [App::DocumentObjectGroupPython] O_element011  label="O_element : 005"  # scripted group (container) (typed FeaturePython)
  n = 1
  ref = O_element
FEATURE [App::DocumentObjectGroupPython] G4_BERYLLIUM_OXIDE  # scripted group (container) (typed FeaturePython)
  Dunit = g/cm3
  Dvalue = 3.01
  Group = -> [Be_element001,O_element011]
  conduct = 2
  density = 1
  expand = 3
  formula = G4_BERYLLIUM_OXIDE
  name = G4_BERYLLIUM_OXIDE
  specific = 4
FEATURE [App::DocumentObjectGroupPython] Bi_element001  label="Bi_element : 4"  # scripted group (container) (typed FeaturePython)
  n = 4
  ref = Bi_element
FEATURE [App::DocumentObjectGroupPython] Ge_element001  label="Ge_element : 3"  # scripted group (container) (typed FeaturePython)
  n = 3
  ref = Ge_element
FEATURE [App::DocumentObjectGroupPython] O_element012  label="O_element : 12"  # scripted group (container) (typed FeaturePython)
  n = 12
  ref = O_element
FEATURE [App::DocumentObjectGroupPython] G4_BGO  # scripted group (container) (typed FeaturePython)
  Dunit = g/cm3
  Dvalue = 7.13
  Group = -> [Bi_element001,Ge_element001,O_element012]
  conduct = 2
  density = 1
  expand = 3
  formula = G4_BGO
  name = G4_BGO
  specific = 4
FEATURE [App::DocumentObjectGroupPython] H_element014  label="H_element : 0.102"  # scripted group (container) (typed FeaturePython)
  n = 0.102
FEATURE [App::DocumentObjectGroupPython] C_element014  label="C_element : 0.110"  # scripted group (container) (typed FeaturePython)
  n = 0.11
FEATURE [App::DocumentObjectGroupPython] N_element009  label="N_element : 0.033"  # scripted group (container) (typed FeaturePython)
  n = 0.033
FEATURE [App::DocumentObjectGroupPython] O_element013  label="O_element : 0.745"  # scripted group (container) (typed FeaturePython)
  n = 0.745
FEATURE [App::DocumentObjectGroupPython] Na_element002  label="Na_element : 0.002"  # scripted group (container) (typed FeaturePython)
  n = 0.001
FEATURE [App::DocumentObjectGroupPython] P_element001  label="P_element : 0.001"  # scripted group (container) (typed FeaturePython)
  n = 0.001
FEATURE [App::DocumentObjectGroupPython] S_element003  label="S_element : 0.002"  # scripted group (container) (typed FeaturePython)
  n = 0.002
FEATURE [App::DocumentObjectGroupPython] Cl_element002  label="Cl_element : 0.003"  # scripted group (container) (typed FeaturePython)
  n = 0.003
FEATURE [App::DocumentObjectGroupPython] K_element001  label="K_element : 0.002"  # scripted group (container) (typed FeaturePython)
  n = 0.002
FEATURE [App::DocumentObjectGroupPython] Fe_element001  label="Fe_element : 0.001"  # scripted group (container) (typed FeaturePython)
  n = 0.001
FEATURE [App::DocumentObjectGroupPython] G4_BLOOD_ICRP  # scripted group (container) (typed FeaturePython)
  Dunit = g/cm3
  Dvalue = 1.06
  Group = -> [H_element014,C_element014,N_element009,O_element013,Na_element002,P_element001,S_element003,Cl_element002,K_element001,Fe_element001]
  conduct = 2
  density = 1
  expand = 3
  formula = G4_BLOOD_ICRP
  name = G4_BLOOD_ICRP
  specific = 4
FEATURE [App::DocumentObjectGroupPython] H_element015  label="H_element : 0.064"  # scripted group (container) (typed FeaturePython)
  n = 0.064
FEATURE [App::DocumentObjectGroupPython] C_element015  label="C_element : 0.278"  # scripted group (container) (typed FeaturePython)
  n = 0.278
FEATURE [App::DocumentObjectGroupPython] N_element010  label="N_element : 0.027"  # scripted group (container) (typed FeaturePython)
  n = 0.027
FEATURE [App::DocumentObjectGroupPython] O_element014  label="O_element : 0.410"  # scripted group (container) (typed FeaturePython)
  n = 0.41
FEATURE [App::DocumentObjectGroupPython] Mg_element001  label="Mg_element : 0.002"  # scripted group (container) (typed FeaturePython)
  n = 0.002
FEATURE [App::DocumentObjectGroupPython] P_element002  label="P_element : 0.070"  # scripted group (container) (typed FeaturePython)
  n = 0.07
FEATURE [App::DocumentObjectGroupPython] S_element004  label="S_element : 0.003"  # scripted group (container) (typed FeaturePython)
  n = 0.002
FEATURE [App::DocumentObjectGroupPython] Ca_element003  label="Ca_element : 0.147"  # scripted group (container) (typed FeaturePython)
  n = 0.147
FEATURE [App::DocumentObjectGroupPython] G4_BONE_COMPACT_ICRU  # scripted group (container) (typed FeaturePython)
  Dunit = g/cm3
  Dvalue = 1.85
  Group = -> [H_element015,C_element015,N_element010,O_element014,Mg_element001,P_element002,S_element004,Ca_element003]
  conduct = 2
  density = 1
  expand = 3
  formula = G4_BONE_COMPACT_ICRU
  name = G4_BONE_COMPACT_ICRU
  specific = 4
FEATURE [App::DocumentObjectGroupPython] H_element016  label="H_element : 0.034"  # scripted group (container) (typed FeaturePython)
  n = 0.034
FEATURE [App::DocumentObjectGroupPython] C_element016  label="C_element : 0.155"  # scripted group (container) (typed FeaturePython)
  n = 0.155
FEATURE [App::DocumentObjectGroupPython] N_element011  label="N_element : 0.042"  # scripted group (container) (typed FeaturePython)
  n = 0.042
FEATURE [App::DocumentObjectGroupPython] O_element015  label="O_element : 0.435"  # scripted group (container) (typed FeaturePython)
  n = 0.435
FEATURE [App::DocumentObjectGroupPython] Na_element003  label="Na_element : 0.003"  # scripted group (container) (typed FeaturePython)
  n = 0.001
FEATURE [App::DocumentObjectGroupPython] Mg_element002  label="Mg_element : 0.003"  # scripted group (container) (typed FeaturePython)
  n = 0.002
FEATURE [App::DocumentObjectGroupPython] P_element003  label="P_element : 0.103"  # scripted group (container) (typed FeaturePython)
  n = 0.103
FEATURE [App::DocumentObjectGroupPython] S_element005  label="S_element : 0.004"  # scripted group (container) (typed FeaturePython)
  n = 0.003
FEATURE [App::DocumentObjectGroupPython] Ca_element004  label="Ca_element : 0.225"  # scripted group (container) (typed FeaturePython)
  n = 0.225
FEATURE [App::DocumentObjectGroupPython] G4_BONE_CORTICAL_ICRP  # scripted group (container) (typed FeaturePython)
  Dunit = g/cm3
  Dvalue = 1.92
  Group = -> [H_element016,C_element016,N_element011,O_element015,Na_element003,Mg_element002,P_element003,S_element005,Ca_element004]
  conduct = 2
  density = 1
  expand = 3
  formula = G4_BONE_CORTICAL_ICRP
  name = G4_BONE_CORTICAL_ICRP
  specific = 4
FEATURE [App::DocumentObjectGroupPython] B_element001  label="B_element : 4"  # scripted group (container) (typed FeaturePython)
  n = 4
  ref = B_element
FEATURE [App::DocumentObjectGroupPython] C_element017  label="C_element : 1"  # scripted group (container) (typed FeaturePython)
  n = 1
  ref = C_element
FEATURE [App::DocumentObjectGroupPython] G4_BORON_CARBIDE  # scripted group (container) (typed FeaturePython)
  Dunit = g/cm3
  Dvalue = 2.52
  Group = -> [B_element001,C_element017]
  conduct = 2
  density = 1
  expand = 3
  formula = G4_BORON_CARBIDE
  name = G4_BORON_CARBIDE
  specific = 4
FEATURE [App::DocumentObjectGroupPython] B_element002  label="B_element : 2"  # scripted group (container) (typed FeaturePython)
  n = 2
  ref = B_element
FEATURE [App::DocumentObjectGroupPython] O_element016  label="O_element : 006"  # scripted group (container) (typed FeaturePython)
  n = 3
  ref = O_element
FEATURE [App::DocumentObjectGroupPython] G4_BORON_OXIDE  # scripted group (container) (typed FeaturePython)
  Dunit = g/cm3
  Dvalue = 1.812
  Group = -> [B_element002,O_element016]
  conduct = 2
  density = 1
  expand = 3
  formula = G4_BORON_OXIDE
  name = G4_BORON_OXIDE
  specific = 4
FEATURE [App::DocumentObjectGroupPython] H_element017  label="H_element : 0.107"  # scripted group (container) (typed FeaturePython)
  n = 0.107
FEATURE [App::DocumentObjectGroupPython] C_element018  label="C_element : 0.145"  # scripted group (container) (typed FeaturePython)
  n = 0.145
FEATURE [App::DocumentObjectGroupPython] N_element012  label="N_element : 0.022"  # scripted group (container) (typed FeaturePython)
  n = 0.022
FEATURE [App::DocumentObjectGroupPython] O_element017  label="O_element : 0.712"  # scripted group (container) (typed FeaturePython)
  n = 0.712
FEATURE [App::DocumentObjectGroupPython] Na_element004  label="Na_element : 0.004"  # scripted group (container) (typed FeaturePython)
  n = 0.002
FEATURE [App::DocumentObjectGroupPython] P_element004  label="P_element : 0.004"  # scripted group (container) (typed FeaturePython)
  n = 0.004
FEATURE [App::DocumentObjectGroupPython] S_element006  label="S_element : 0.005"  # scripted group (container) (typed FeaturePython)
  n = 0.002
FEATURE [App::DocumentObjectGroupPython] Cl_element003  label="Cl_element : 0.004"  # scripted group (container) (typed FeaturePython)
  n = 0.003
FEATURE [App::DocumentObjectGroupPython] K_element002  label="K_element : 0.003"  # scripted group (container) (typed FeaturePython)
  n = 0.003
FEATURE [App::DocumentObjectGroupPython] G4_BRAIN_ICRP  # scripted group (container) (typed FeaturePython)
  Dunit = g/cm3
  Dvalue = 1.04
  Group = -> [H_element017,C_element018,N_element012,O_element017,Na_element004,P_element004,S_element006,Cl_element003,K_element002]
  conduct = 2
  density = 1
  expand = 3
  formula = G4_BRAIN_ICRP
  name = G4_BRAIN_ICRP
  specific = 4
FEATURE [App::DocumentObjectGroupPython] C_element019  label="C_element : 4"  # scripted group (container) (typed FeaturePython)
  n = 4
  ref = C_element
FEATURE [App::DocumentObjectGroupPython] H_element018  label="H_element : 010"  # scripted group (container) (typed FeaturePython)
  n = 10
  ref = H_element
FEATURE [App::DocumentObjectGroupPython] G4_BUTANE  # scripted group (container) (typed FeaturePython)
  Dunit = g/cm3
  Dvalue = 0.00249343
  Group = -> [C_element019,H_element018]
  conduct = 2
  density = 1
  expand = 3
  formula = G4_BUTANE
  name = G4_BUTANE
  specific = 4
FEATURE [App::DocumentObjectGroupPython] C_element020  label="C_element : 008"  # scripted group (container) (typed FeaturePython)
  n = 4
  ref = C_element
FEATURE [App::DocumentObjectGroupPython] H_element019  label="H_element : 011"  # scripted group (container) (typed FeaturePython)
  n = 10
  ref = H_element
FEATURE [App::DocumentObjectGroupPython] O_element018  label="O_element : 007"  # scripted group (container) (typed FeaturePython)
  n = 1
  ref = O_element
FEATURE [App::DocumentObjectGroupPython] G4_N_BUTYL_ALCOHOL  label="G4_N-BUTYL_ALCOHOL"  # scripted group (container) (typed FeaturePython)
  Dunit = g/cm3
  Dvalue = 0.8098
  Group = -> [C_element020,H_element019,O_element018]
  conduct = 2
  density = 1
  expand = 3
  formula = G4_N-BUTYL_ALCOHOL
  name = G4_N-BUTYL_ALCOHOL
  specific = 4
FEATURE [App::DocumentObjectGroupPython] H_element020  label="H_element : 0.025"  # scripted group (container) (typed FeaturePython)
  n = 0.02468
FEATURE [App::DocumentObjectGroupPython] C_element021  label="C_element : 0.502"  # scripted group (container) (typed FeaturePython)
  n = 0.501611
FEATURE [App::DocumentObjectGroupPython] O_element019  label="O_element : 0.005"  # scripted group (container) (typed FeaturePython)
  n = 0.004527
FEATURE [App::DocumentObjectGroupPython] F_element004  label="F_element : 0.465"  # scripted group (container) (typed FeaturePython)
  n = 0.465209
FEATURE [App::DocumentObjectGroupPython] Si_element001  label="Si_element : 0.004"  # scripted group (container) (typed FeaturePython)
  n = 0.003973
FEATURE [App::DocumentObjectGroupPython] G4_C_552  label="G4_C-552"  # scripted group (container) (typed FeaturePython)
  Dunit = g/cm3
  Dvalue = 1.76
  Group = -> [H_element020,C_element021,O_element019,F_element004,Si_element001]
  conduct = 2
  density = 1
  expand = 3
  formula = G4_C-552
  name = G4_C-552
  specific = 4
FEATURE [App::DocumentObjectGroupPython] Cd_element001  label="Cd_element : 1"  # scripted group (container) (typed FeaturePython)
  n = 1
  ref = Cd_element
FEATURE [App::DocumentObjectGroupPython] Te_element001  label="Te_element : 1"  # scripted group (container) (typed FeaturePython)
  n = 1
  ref = Te_element
FEATURE [App::DocumentObjectGroupPython] G4_CADMIUM_TELLURIDE  # scripted group (container) (typed FeaturePython)
  Dunit = g/cm3
  Dvalue = 6.2
  Group = -> [Cd_element001,Te_element001]
  conduct = 2
  density = 1
  expand = 3
  formula = G4_CADMIUM_TELLURIDE
  name = G4_CADMIUM_TELLURIDE
  specific = 4
FEATURE [App::DocumentObjectGroupPython] Cd_element002  label="Cd_element : 002"  # scripted group (container) (typed FeaturePython)
  n = 1
  ref = Cd_element
FEATURE [App::DocumentObjectGroupPython] W_element001  label="W_element : 1"  # scripted group (container) (typed FeaturePython)
  n = 1
  ref = W_element
FEATURE [App::DocumentObjectGroupPython] O_element020  label="O_element : 008"  # scripted group (container) (typed FeaturePython)
  n = 4
  ref = O_element
FEATURE [App::DocumentObjectGroupPython] G4_CADMIUM_TUNGSTATE  # scripted group (container) (typed FeaturePython)
  Dunit = g/cm3
  Dvalue = 7.9
  Group = -> [Cd_element002,W_element001,O_element020]
  conduct = 2
  density = 1
  expand = 3
  formula = G4_CADMIUM_TUNGSTATE
  name = G4_CADMIUM_TUNGSTATE
  specific = 4
FEATURE [App::DocumentObjectGroupPython] Ca_element005  label="Ca_element : 1"  # scripted group (container) (typed FeaturePython)
  n = 1
  ref = Ca_element
FEATURE [App::DocumentObjectGroupPython] C_element022  label="C_element : 009"  # scripted group (container) (typed FeaturePython)
  n = 1
  ref = C_element
FEATURE [App::DocumentObjectGroupPython] O_element021  label="O_element : 009"  # scripted group (container) (typed FeaturePython)
  n = 3
  ref = O_element
FEATURE [App::DocumentObjectGroupPython] G4_CALCIUM_CARBONATE  # scripted group (container) (typed FeaturePython)
  Dunit = g/cm3
  Dvalue = 2.8
  Group = -> [Ca_element005,C_element022,O_element021]
  conduct = 2
  density = 1
  expand = 3
  formula = G4_CALCIUM_CARBONATE
  name = G4_CALCIUM_CARBONATE
  specific = 4
FEATURE [App::DocumentObjectGroupPython] Ca_element006  label="Ca_element : 002"  # scripted group (container) (typed FeaturePython)
  n = 1
  ref = Ca_element
FEATURE [App::DocumentObjectGroupPython] F_element005  label="F_element : 003"  # scripted group (container) (typed FeaturePython)
  n = 2
  ref = F_element
FEATURE [App::DocumentObjectGroupPython] G4_CALCIUM_FLUORIDE  # scripted group (container) (typed FeaturePython)
  Dunit = g/cm3
  Dvalue = 3.18
  Group = -> [Ca_element006,F_element005]
  conduct = 2
  density = 1
  expand = 3
  formula = G4_CALCIUM_FLUORIDE
  name = G4_CALCIUM_FLUORIDE
  specific = 4
FEATURE [App::DocumentObjectGroupPython] Ca_element007  label="Ca_element : 003"  # scripted group (container) (typed FeaturePython)
  n = 1
  ref = Ca_element
FEATURE [App::DocumentObjectGroupPython] O_element022  label="O_element : 010"  # scripted group (container) (typed FeaturePython)
  n = 1
  ref = O_element
FEATURE [App::DocumentObjectGroupPython] G4_CALCIUM_OXIDE  # scripted group (container) (typed FeaturePython)
  Dunit = g/cm3
  Dvalue = 3.3
  Group = -> [Ca_element007,O_element022]
  conduct = 2
  density = 1
  expand = 3
  formula = G4_CALCIUM_OXIDE
  name = G4_CALCIUM_OXIDE
  specific = 4
FEATURE [App::DocumentObjectGroupPython] Ca_element008  label="Ca_element : 004"  # scripted group (container) (typed FeaturePython)
  n = 1
  ref = Ca_element
FEATURE [App::DocumentObjectGroupPython] S_element007  label="S_element : 002"  # scripted group (container) (typed FeaturePython)
  n = 1
  ref = S_element
FEATURE [App::DocumentObjectGroupPython] O_element023  label="O_element : 011"  # scripted group (container) (typed FeaturePython)
  n = 4
  ref = O_element
FEATURE [App::DocumentObjectGroupPython] G4_CALCIUM_SULFATE  # scripted group (container) (typed FeaturePython)
  Dunit = g/cm3
  Dvalue = 2.96
  Group = -> [Ca_element008,S_element007,O_element023]
  conduct = 2
  density = 1
  expand = 3
  formula = G4_CALCIUM_SULFATE
  name = G4_CALCIUM_SULFATE
  specific = 4
FEATURE [App::DocumentObjectGroupPython] Ca_element009  label="Ca_element : 005"  # scripted group (container) (typed FeaturePython)
  n = 1
  ref = Ca_element
FEATURE [App::DocumentObjectGroupPython] W_element002  label="W_element : 002"  # scripted group (container) (typed FeaturePython)
  n = 1
  ref = W_element
FEATURE [App::DocumentObjectGroupPython] O_element024  label="O_element : 012"  # scripted group (container) (typed FeaturePython)
  n = 4
  ref = O_element
FEATURE [App::DocumentObjectGroupPython] G4_CALCIUM_TUNGSTATE  # scripted group (container) (typed FeaturePython)
  Dunit = g/cm3
  Dvalue = 6.062
  Group = -> [Ca_element009,W_element002,O_element024]
  conduct = 2
  density = 1
  expand = 3
  formula = G4_CALCIUM_TUNGSTATE
  name = G4_CALCIUM_TUNGSTATE
  specific = 4
FEATURE [App::DocumentObjectGroupPython] C_element023  label="C_element : 010"  # scripted group (container) (typed FeaturePython)
  n = 1
  ref = C_element
FEATURE [App::DocumentObjectGroupPython] O_element025  label="O_element : 013"  # scripted group (container) (typed FeaturePython)
  n = 2
  ref = O_element
FEATURE [App::DocumentObjectGroupPython] G4_CARBON_DIOXIDE  # scripted group (container) (typed FeaturePython)
  Dunit = g/cm3
  Dvalue = 0.00184212
  Group = -> [C_element023,O_element025]
  conduct = 2
  density = 1
  expand = 3
  formula = G4_CARBON_DIOXIDE
  name = G4_CARBON_DIOXIDE
  specific = 4
FEATURE [App::DocumentObjectGroupPython] C_element024  label="C_element : 011"  # scripted group (container) (typed FeaturePython)
  n = 1
  ref = C_element
FEATURE [App::DocumentObjectGroupPython] Cl_element004  label="Cl_element : 4"  # scripted group (container) (typed FeaturePython)
  n = 4
  ref = Cl_element
FEATURE [App::DocumentObjectGroupPython] G4_CARBON_TETRACHLORIDE  # scripted group (container) (typed FeaturePython)
  Dunit = g/cm3
  Dvalue = 1.594
  Group = -> [C_element024,Cl_element004]
  conduct = 2
  density = 1
  expand = 3
  formula = G4_CARBON_TETRACHLORIDE
  name = G4_CARBON_TETRACHLORIDE
  specific = 4
FEATURE [App::DocumentObjectGroupPython] C_element025  label="C_element : 012"  # scripted group (container) (typed FeaturePython)
  n = 6
  ref = C_element
FEATURE [App::DocumentObjectGroupPython] H_element021  label="H_element : 012"  # scripted group (container) (typed FeaturePython)
  n = 10
  ref = H_element
FEATURE [App::DocumentObjectGroupPython] O_element026  label="O_element : 5"  # scripted group (container) (typed FeaturePython)
  n = 5
  ref = O_element
FEATURE [App::DocumentObjectGroupPython] G4_CELLULOSE_CELLOPHANE  # scripted group (container) (typed FeaturePython)
  Dunit = g/cm3
  Dvalue = 1.42
  Group = -> [C_element025,H_element021,O_element026]
  conduct = 2
  density = 1
  expand = 3
  formula = G4_CELLULOSE_CELLOPHANE
  name = G4_CELLULOSE_CELLOPHANE
  specific = 4
FEATURE [App::DocumentObjectGroupPython] H_element022  label="H_element : 0.067"  # scripted group (container) (typed FeaturePython)
  n = 0.067125
FEATURE [App::DocumentObjectGroupPython] C_element026  label="C_element : 0.545"  # scripted group (container) (typed FeaturePython)
  n = 0.545403
FEATURE [App::DocumentObjectGroupPython] O_element027  label="O_element : 0.387"  # scripted group (container) (typed FeaturePython)
  n = 0.387472
FEATURE [App::DocumentObjectGroupPython] G4_CELLULOSE_BUTYRATE  # scripted group (container) (typed FeaturePython)
  Dunit = g/cm3
  Dvalue = 1.2
  Group = -> [H_element022,C_element026,O_element027]
  conduct = 2
  density = 1
  expand = 3
  formula = G4_CELLULOSE_BUTYRATE
  name = G4_CELLULOSE_BUTYRATE
  specific = 4
FEATURE [App::DocumentObjectGroupPython] H_element023  label="H_element : 0.029"  # scripted group (container) (typed FeaturePython)
  n = 0.029216
FEATURE [App::DocumentObjectGroupPython] C_element027  label="C_element : 0.271"  # scripted group (container) (typed FeaturePython)
  n = 0.271296
FEATURE [App::DocumentObjectGroupPython] N_element013  label="N_element : 0.121"  # scripted group (container) (typed FeaturePython)
  n = 0.121276
FEATURE [App::DocumentObjectGroupPython] O_element028  label="O_element : 0.578"  # scripted group (container) (typed FeaturePython)
  n = 0.578212
FEATURE [App::DocumentObjectGroupPython] G4_CELLULOSE_NITRATE  # scripted group (container) (typed FeaturePython)
  Dunit = g/cm3
  Dvalue = 1.49
  Group = -> [H_element023,C_element027,N_element013,O_element028]
  conduct = 2
  density = 1
  expand = 3
  formula = G4_CELLULOSE_NITRATE
  name = G4_CELLULOSE_NITRATE
  specific = 4
FEATURE [App::DocumentObjectGroupPython] H_element024  label="H_element : 0.108"  # scripted group (container) (typed FeaturePython)
  n = 0.107596
FEATURE [App::DocumentObjectGroupPython] N_element014  label="N_element : 0.001"  # scripted group (container) (typed FeaturePython)
  n = 0.0008
FEATURE [App::DocumentObjectGroupPython] O_element029  label="O_element : 0.875"  # scripted group (container) (typed FeaturePython)
  n = 0.874976
FEATURE [App::DocumentObjectGroupPython] S_element008  label="S_element : 0.015"  # scripted group (container) (typed FeaturePython)
  n = 0.014627
FEATURE [App::DocumentObjectGroupPython] Ce_element001  label="Ce_element : 0.002"  # scripted group (container) (typed FeaturePython)
  n = 0.002001
FEATURE [App::DocumentObjectGroupPython] G4_CERIC_SULFATE  # scripted group (container) (typed FeaturePython)
  Dunit = g/cm3
  Dvalue = 1.03
  Group = -> [H_element024,N_element014,O_element029,S_element008,Ce_element001]
  conduct = 2
  density = 1
  expand = 3
  formula = G4_CERIC_SULFATE
  name = G4_CERIC_SULFATE
  specific = 4
FEATURE [App::DocumentObjectGroupPython] Cs_element001  label="Cs_element : 1"  # scripted group (container) (typed FeaturePython)
  n = 1
  ref = Cs_element
FEATURE [App::DocumentObjectGroupPython] F_element006  label="F_element : 1"  # scripted group (container) (typed FeaturePython)
  n = 1
  ref = F_element
FEATURE [App::DocumentObjectGroupPython] G4_CESIUM_FLUORIDE  # scripted group (container) (typed FeaturePython)
  Dunit = g/cm3
  Dvalue = 4.115
  Group = -> [Cs_element001,F_element006]
  conduct = 2
  density = 1
  expand = 3
  formula = G4_CESIUM_FLUORIDE
  name = G4_CESIUM_FLUORIDE
  specific = 4
FEATURE [App::DocumentObjectGroupPython] Cs_element002  label="Cs_element : 002"  # scripted group (container) (typed FeaturePython)
  n = 1
  ref = Cs_element
FEATURE [App::DocumentObjectGroupPython] I_element001  label="I_element : 1"  # scripted group (container) (typed FeaturePython)
  n = 1
  ref = I_element
FEATURE [App::DocumentObjectGroupPython] G4_CESIUM_IODIDE  # scripted group (container) (typed FeaturePython)
  Dunit = g/cm3
  Dvalue = 4.51
  Group = -> [Cs_element002,I_element001]
  conduct = 2
  density = 1
  expand = 3
  formula = G4_CESIUM_IODIDE
  name = G4_CESIUM_IODIDE
  specific = 4
FEATURE [App::DocumentObjectGroupPython] C_element028  label="C_element : 013"  # scripted group (container) (typed FeaturePython)
  n = 6
  ref = C_element
FEATURE [App::DocumentObjectGroupPython] H_element025  label="H_element : 013"  # scripted group (container) (typed FeaturePython)
  n = 5
  ref = H_element
FEATURE [App::DocumentObjectGroupPython] Cl_element005  label="Cl_element : 1"  # scripted group (container) (typed FeaturePython)
  n = 1
  ref = Cl_element
FEATURE [App::DocumentObjectGroupPython] G4_CHLOROBENZENE  # scripted group (container) (typed FeaturePython)
  Dunit = g/cm3
  Dvalue = 1.1058
  Group = -> [C_element028,H_element025,Cl_element005]
  conduct = 2
  density = 1
  expand = 3
  formula = G4_CHLOROBENZENE
  name = G4_CHLOROBENZENE
  specific = 4
FEATURE [App::DocumentObjectGroupPython] C_element029  label="C_element : 014"  # scripted group (container) (typed FeaturePython)
  n = 1
  ref = C_element
FEATURE [App::DocumentObjectGroupPython] H_element026  label="H_element : 1"  # scripted group (container) (typed FeaturePython)
  n = 1
  ref = H_element
FEATURE [App::DocumentObjectGroupPython] Cl_element006  label="Cl_element : 3"  # scripted group (container) (typed FeaturePython)
  n = 3
  ref = Cl_element
FEATURE [App::DocumentObjectGroupPython] G4_CHLOROFORM  # scripted group (container) (typed FeaturePython)
  Dunit = g/cm3
  Dvalue = 1.4832
  Group = -> [C_element029,H_element026,Cl_element006]
  conduct = 2
  density = 1
  expand = 3
  formula = G4_CHLOROFORM
  name = G4_CHLOROFORM
  specific = 4
FEATURE [App::DocumentObjectGroupPython] H_element027  label="H_element : 0.010"  # scripted group (container) (typed FeaturePython)
  n = 0.01
FEATURE [App::DocumentObjectGroupPython] C_element030  label="C_element : 0.001"  # scripted group (container) (typed FeaturePython)
  n = 0.001
FEATURE [App::DocumentObjectGroupPython] O_element030  label="O_element : 0.529"  # scripted group (container) (typed FeaturePython)
  n = 0.529107
FEATURE [App::DocumentObjectGroupPython] Na_element005  label="Na_element : 0.016"  # scripted group (container) (typed FeaturePython)
  n = 0.016
FEATURE [App::DocumentObjectGroupPython] Mg_element003  label="Mg_element : 0.004"  # scripted group (container) (typed FeaturePython)
  n = 0.002
FEATURE [App::DocumentObjectGroupPython] Al_element002  label="Al_element : 0.034"  # scripted group (container) (typed FeaturePython)
  n = 0.033872
FEATURE [App::DocumentObjectGroupPython] Si_element002  label="Si_element : 0.337"  # scripted group (container) (typed FeaturePython)
  n = 0.337021
FEATURE [App::DocumentObjectGroupPython] K_element003  label="K_element : 0.013"  # scripted group (container) (typed FeaturePython)
  n = 0.013
FEATURE [App::DocumentObjectGroupPython] Ca_element010  label="Ca_element : 0.044"  # scripted group (container) (typed FeaturePython)
  n = 0.044
FEATURE [App::DocumentObjectGroupPython] Fe_element002  label="Fe_element : 0.014"  # scripted group (container) (typed FeaturePython)
  n = 0.014
FEATURE [App::DocumentObjectGroupPython] G4_CONCRETE  # scripted group (container) (typed FeaturePython)
  Dunit = g/cm3
  Dvalue = 2.3
  Group = -> [H_element027,C_element030,O_element030,Na_element005,Mg_element003,Al_element002,Si_element002,K_element003,Ca_element010,Fe_element002]
  conduct = 2
  density = 1
  expand = 3
  formula = G4_CONCRETE
  name = G4_CONCRETE
  specific = 4
FEATURE [App::DocumentObjectGroupPython] C_element031  label="C_element : 015"  # scripted group (container) (typed FeaturePython)
  n = 6
  ref = C_element
FEATURE [App::DocumentObjectGroupPython] H_element028  label="H_element : 12"  # scripted group (container) (typed FeaturePython)
  n = 12
  ref = H_element
FEATURE [App::DocumentObjectGroupPython] G4_CYCLOHEXANE  # scripted group (container) (typed FeaturePython)
  Dunit = g/cm3
  Dvalue = 0.779
  Group = -> [C_element031,H_element028]
  conduct = 2
  density = 1
  expand = 3
  formula = G4_CYCLOHEXANE
  name = G4_CYCLOHEXANE
  specific = 4
FEATURE [App::DocumentObjectGroupPython] C_element032  label="C_element : 016"  # scripted group (container) (typed FeaturePython)
  n = 6
  ref = C_element
FEATURE [App::DocumentObjectGroupPython] H_element029  label="H_element : 4"  # scripted group (container) (typed FeaturePython)
  n = 4
  ref = H_element
FEATURE [App::DocumentObjectGroupPython] Cl_element007  label="Cl_element : 2"  # scripted group (container) (typed FeaturePython)
  n = 2
  ref = Cl_element
FEATURE [App::DocumentObjectGroupPython] G4_1_2_DICHLOROBENZENE  label="G4_1.2-DICHLOROBENZENE"  # scripted group (container) (typed FeaturePython)
  Dunit = g/cm3
  Dvalue = 1.3048
  Group = -> [C_element032,H_element029,Cl_element007]
  conduct = 2
  density = 1
  expand = 3
  formula = G4_1.2-DICHLOROBENZENE
  name = G4_1.2-DICHLOROBENZENE
  specific = 4
FEATURE [App::DocumentObjectGroupPython] C_element033  label="C_element : 017"  # scripted group (container) (typed FeaturePython)
  n = 4
  ref = C_element
FEATURE [App::DocumentObjectGroupPython] H_element030  label="H_element : 8"  # scripted group (container) (typed FeaturePython)
  n = 8
  ref = H_element
FEATURE [App::DocumentObjectGroupPython] O_element031  label="O_element : 014"  # scripted group (container) (typed FeaturePython)
  n = 1
  ref = O_element
FEATURE [App::DocumentObjectGroupPython] Cl_element008  label="Cl_element : 005"  # scripted group (container) (typed FeaturePython)
  n = 2
  ref = Cl_element
FEATURE [App::DocumentObjectGroupPython] G4_DICHLORODIETHYL_ETHER  # scripted group (container) (typed FeaturePython)
  Dunit = g/cm3
  Dvalue = 1.2199
  Group = -> [C_element033,H_element030,O_element031,Cl_element008]
  conduct = 2
  density = 1
  expand = 3
  formula = G4_DICHLORODIETHYL_ETHER
  name = G4_DICHLORODIETHYL_ETHER
  specific = 4
FEATURE [App::DocumentObjectGroupPython] C_element034  label="C_element : 018"  # scripted group (container) (typed FeaturePython)
  n = 2
  ref = C_element
FEATURE [App::DocumentObjectGroupPython] H_element031  label="H_element : 014"  # scripted group (container) (typed FeaturePython)
  n = 4
  ref = H_element
FEATURE [App::DocumentObjectGroupPython] Cl_element009  label="Cl_element : 006"  # scripted group (container) (typed FeaturePython)
  n = 2
  ref = Cl_element
FEATURE [App::DocumentObjectGroupPython] G4_1_2_DICHLOROETHANE  label="G4_1.2-DICHLOROETHANE"  # scripted group (container) (typed FeaturePython)
  Dunit = g/cm3
  Dvalue = 1.2351
  Group = -> [C_element034,H_element031,Cl_element009]
  conduct = 2
  density = 1
  expand = 3
  formula = G4_1.2-DICHLOROETHANE
  name = G4_1.2-DICHLOROETHANE
  specific = 4
FEATURE [App::DocumentObjectGroupPython] C_element035  label="C_element : 019"  # scripted group (container) (typed FeaturePython)
  n = 4
  ref = C_element
FEATURE [App::DocumentObjectGroupPython] H_element032  label="H_element : 015"  # scripted group (container) (typed FeaturePython)
  n = 10
  ref = H_element
FEATURE [App::DocumentObjectGroupPython] O_element032  label="O_element : 015"  # scripted group (container) (typed FeaturePython)
  n = 1
  ref = O_element
FEATURE [App::DocumentObjectGroupPython] G4_DIETHYL_ETHER  # scripted group (container) (typed FeaturePython)
  Dunit = g/cm3
  Dvalue = 0.71378
  Group = -> [C_element035,H_element032,O_element032]
  conduct = 2
  density = 1
  expand = 3
  formula = G4_DIETHYL_ETHER
  name = G4_DIETHYL_ETHER
  specific = 4
FEATURE [App::DocumentObjectGroupPython] C_element036  label="C_element : 020"  # scripted group (container) (typed FeaturePython)
  n = 3
  ref = C_element
FEATURE [App::DocumentObjectGroupPython] H_element033  label="H_element : 016"  # scripted group (container) (typed FeaturePython)
  n = 7
  ref = H_element
FEATURE [App::DocumentObjectGroupPython] N_element015  label="N_element : 008"  # scripted group (container) (typed FeaturePython)
  n = 1
  ref = N_element
FEATURE [App::DocumentObjectGroupPython] O_element033  label="O_element : 016"  # scripted group (container) (typed FeaturePython)
  n = 1
  ref = O_element
FEATURE [App::DocumentObjectGroupPython] G4_N_N_DIMETHYL_FORMAMIDE  label="G4_N.N-DIMETHYL_FORMAMIDE"  # scripted group (container) (typed FeaturePython)
  Dunit = g/cm3
  Dvalue = 0.9487
  Group = -> [C_element036,H_element033,N_element015,O_element033]
  conduct = 2
  density = 1
  expand = 3
  formula = G4_N.N-DIMETHYL_FORMAMIDE
  name = G4_N.N-DIMETHYL_FORMAMIDE
  specific = 4
FEATURE [App::DocumentObjectGroupPython] C_element037  label="C_element : 021"  # scripted group (container) (typed FeaturePython)
  n = 2
  ref = C_element
FEATURE [App::DocumentObjectGroupPython] H_element034  label="H_element : 017"  # scripted group (container) (typed FeaturePython)
  n = 6
  ref = H_element
FEATURE [App::DocumentObjectGroupPython] O_element034  label="O_element : 017"  # scripted group (container) (typed FeaturePython)
  n = 1
  ref = O_element
FEATURE [App::DocumentObjectGroupPython] S_element009  label="S_element : 003"  # scripted group (container) (typed FeaturePython)
  n = 1
  ref = S_element
FEATURE [App::DocumentObjectGroupPython] G4_DIMETHYL_SULFOXIDE  # scripted group (container) (typed FeaturePython)
  Dunit = g/cm3
  Dvalue = 1.1014
  Group = -> [C_element037,H_element034,O_element034,S_element009]
  conduct = 2
  density = 1
  expand = 3
  formula = G4_DIMETHYL_SULFOXIDE
  name = G4_DIMETHYL_SULFOXIDE
  specific = 4
FEATURE [App::DocumentObjectGroupPython] C_element038  label="C_element : 022"  # scripted group (container) (typed FeaturePython)
  n = 2
  ref = C_element
FEATURE [App::DocumentObjectGroupPython] H_element035  label="H_element : 018"  # scripted group (container) (typed FeaturePython)
  n = 6
  ref = H_element
FEATURE [App::DocumentObjectGroupPython] G4_ETHANE  # scripted group (container) (typed FeaturePython)
  Dunit = g/cm3
  Dvalue = 0.00125324
  Group = -> [C_element038,H_element035]
  conduct = 2
  density = 1
  expand = 3
  formula = G4_ETHANE
  name = G4_ETHANE
  specific = 4
FEATURE [App::DocumentObjectGroupPython] C_element039  label="C_element : 023"  # scripted group (container) (typed FeaturePython)
  n = 2
  ref = C_element
FEATURE [App::DocumentObjectGroupPython] H_element036  label="H_element : 019"  # scripted group (container) (typed FeaturePython)
  n = 6
  ref = H_element
FEATURE [App::DocumentObjectGroupPython] O_element035  label="O_element : 018"  # scripted group (container) (typed FeaturePython)
  n = 1
  ref = O_element
FEATURE [App::DocumentObjectGroupPython] G4_ETHYL_ALCOHOL  # scripted group (container) (typed FeaturePython)
  Dunit = g/cm3
  Dvalue = 0.7893
  Group = -> [C_element039,H_element036,O_element035]
  conduct = 2
  density = 1
  expand = 3
  formula = G4_ETHYL_ALCOHOL
  name = G4_ETHYL_ALCOHOL
  specific = 4
FEATURE [App::DocumentObjectGroupPython] H_element037  label="H_element : 0.090"  # scripted group (container) (typed FeaturePython)
  n = 0.090027
FEATURE [App::DocumentObjectGroupPython] C_element040  label="C_element : 0.585"  # scripted group (container) (typed FeaturePython)
  n = 0.585182
FEATURE [App::DocumentObjectGroupPython] O_element036  label="O_element : 0.325"  # scripted group (container) (typed FeaturePython)
  n = 0.324791
FEATURE [App::DocumentObjectGroupPython] G4_ETHYL_CELLULOSE  # scripted group (container) (typed FeaturePython)
  Dunit = g/cm3
  Dvalue = 1.13
  Group = -> [H_element037,C_element040,O_element036]
  conduct = 2
  density = 1
  expand = 3
  formula = G4_ETHYL_CELLULOSE
  name = G4_ETHYL_CELLULOSE
  specific = 4
FEATURE [App::DocumentObjectGroupPython] C_element041  label="C_element : 024"  # scripted group (container) (typed FeaturePython)
  n = 2
  ref = C_element
FEATURE [App::DocumentObjectGroupPython] H_element038  label="H_element : 020"  # scripted group (container) (typed FeaturePython)
  n = 4
  ref = H_element
FEATURE [App::DocumentObjectGroupPython] G4_ETHYLENE  # scripted group (container) (typed FeaturePython)
  Dunit = g/cm3
  Dvalue = 0.00117497
  Group = -> [C_element041,H_element038]
  conduct = 2
  density = 1
  expand = 3
  formula = G4_ETHYLENE
  name = G4_ETHYLENE
  specific = 4
FEATURE [App::DocumentObjectGroupPython] H_element039  label="H_element : 0.096"  # scripted group (container) (typed FeaturePython)
  n = 0.096
FEATURE [App::DocumentObjectGroupPython] C_element042  label="C_element : 0.195"  # scripted group (container) (typed FeaturePython)
  n = 0.195
FEATURE [App::DocumentObjectGroupPython] N_element016  label="N_element : 0.057"  # scripted group (container) (typed FeaturePython)
  n = 0.057
FEATURE [App::DocumentObjectGroupPython] O_element037  label="O_element : 0.646"  # scripted group (container) (typed FeaturePython)
  n = 0.646
FEATURE [App::DocumentObjectGroupPython] Na_element006  label="Na_element : 0.017"  # scripted group (container) (typed FeaturePython)
  n = 0.001
FEATURE [App::DocumentObjectGroupPython] P_element005  label="P_element : 0.104"  # scripted group (container) (typed FeaturePython)
  n = 0.001
FEATURE [App::DocumentObjectGroupPython] S_element010  label="S_element : 0.016"  # scripted group (container) (typed FeaturePython)
  n = 0.003
FEATURE [App::DocumentObjectGroupPython] Cl_element010  label="Cl_element : 0.005"  # scripted group (container) (typed FeaturePython)
  n = 0.001
FEATURE [App::DocumentObjectGroupPython] G4_EYE_LENS_ICRP  # scripted group (container) (typed FeaturePython)
  Dunit = g/cm3
  Dvalue = 1.07
  Group = -> [H_element039,C_element042,N_element016,O_element037,Na_element006,P_element005,S_element010,Cl_element010]
  conduct = 2
  density = 1
  expand = 3
  formula = G4_EYE_LENS_ICRP
  name = G4_EYE_LENS_ICRP
  specific = 4
FEATURE [App::DocumentObjectGroupPython] Fe_element003  label="Fe_element : 2"  # scripted group (container) (typed FeaturePython)
  n = 2
  ref = Fe_element
FEATURE [App::DocumentObjectGroupPython] O_element038  label="O_element : 019"  # scripted group (container) (typed FeaturePython)
  n = 3
  ref = O_element
FEATURE [App::DocumentObjectGroupPython] G4_FERRIC_OXIDE  # scripted group (container) (typed FeaturePython)
  Dunit = g/cm3
  Dvalue = 5.2
  Group = -> [Fe_element003,O_element038]
  conduct = 2
  density = 1
  expand = 3
  formula = G4_FERRIC_OXIDE
  name = G4_FERRIC_OXIDE
  specific = 4
FEATURE [App::DocumentObjectGroupPython] Fe_element004  label="Fe_element : 1"  # scripted group (container) (typed FeaturePython)
  n = 1
  ref = Fe_element
FEATURE [App::DocumentObjectGroupPython] B_element003  label="B_element : 1"  # scripted group (container) (typed FeaturePython)
  n = 1
  ref = B_element
FEATURE [App::DocumentObjectGroupPython] G4_FERROBORIDE  # scripted group (container) (typed FeaturePython)
  Dunit = g/cm3
  Dvalue = 7.15
  Group = -> [Fe_element004,B_element003]
  conduct = 2
  density = 1
  expand = 3
  formula = G4_FERROBORIDE
  name = G4_FERROBORIDE
  specific = 4
FEATURE [App::DocumentObjectGroupPython] Fe_element005  label="Fe_element : 003"  # scripted group (container) (typed FeaturePython)
  n = 1
  ref = Fe_element
FEATURE [App::DocumentObjectGroupPython] O_element039  label="O_element : 020"  # scripted group (container) (typed FeaturePython)
  n = 1
  ref = O_element
FEATURE [App::DocumentObjectGroupPython] G4_FERROUS_OXIDE  # scripted group (container) (typed FeaturePython)
  Dunit = g/cm3
  Dvalue = 5.7
  Group = -> [Fe_element005,O_element039]
  conduct = 2
  density = 1
  expand = 3
  formula = G4_FERROUS_OXIDE
  name = G4_FERROUS_OXIDE
  specific = 4
FEATURE [App::DocumentObjectGroupPython] H_element040  label="H_element : 0.115"  # scripted group (container) (typed FeaturePython)
  n = 0.108259
FEATURE [App::DocumentObjectGroupPython] N_element017  label="N_element : 0.000"  # scripted group (container) (typed FeaturePython)
  n = 2.7e-05
FEATURE [App::DocumentObjectGroupPython] O_element040  label="O_element : 0.879"  # scripted group (container) (typed FeaturePython)
  n = 0.878636
FEATURE [App::DocumentObjectGroupPython] Na_element007  label="Na_element : 0.000"  # scripted group (container) (typed FeaturePython)
  n = 2.2e-05
FEATURE [App::DocumentObjectGroupPython] S_element011  label="S_element : 0.013"  # scripted group (container) (typed FeaturePython)
  n = 0.012968
FEATURE [App::DocumentObjectGroupPython] Cl_element011  label="Cl_element : 0.000"  # scripted group (container) (typed FeaturePython)
  n = 3.4e-05
FEATURE [App::DocumentObjectGroupPython] Fe_element006  label="Fe_element : 0.000"  # scripted group (container) (typed FeaturePython)
  n = 5.4e-05
FEATURE [App::DocumentObjectGroupPython] G4_FERROUS_SULFATE  # scripted group (container) (typed FeaturePython)
  Dunit = g/cm3
  Dvalue = 1.024
  Group = -> [H_element040,N_element017,O_element040,Na_element007,S_element011,Cl_element011,Fe_element006]
  conduct = 2
  density = 1
  expand = 3
  formula = G4_FERROUS_SULFATE
  name = G4_FERROUS_SULFATE
  specific = 4
FEATURE [App::DocumentObjectGroupPython] C_element043  label="C_element : 0.099"  # scripted group (container) (typed FeaturePython)
  n = 0.099335
FEATURE [App::DocumentObjectGroupPython] F_element007  label="F_element : 0.314"  # scripted group (container) (typed FeaturePython)
  n = 0.314247
FEATURE [App::DocumentObjectGroupPython] Cl_element012  label="Cl_element : 0.586"  # scripted group (container) (typed FeaturePython)
  n = 0.586418
FEATURE [App::DocumentObjectGroupPython] G4_FREON_12  label="G4_FREON-12"  # scripted group (container) (typed FeaturePython)
  Dunit = g/cm3
  Dvalue = 1.12
  Group = -> [C_element043,F_element007,Cl_element012]
  conduct = 2
  density = 1
  expand = 3
  formula = G4_FREON-12
  name = G4_FREON-12
  specific = 4
FEATURE [App::DocumentObjectGroupPython] C_element044  label="C_element : 0.057"  # scripted group (container) (typed FeaturePython)
  n = 0.057245
FEATURE [App::DocumentObjectGroupPython] F_element008  label="F_element : 0.181"  # scripted group (container) (typed FeaturePython)
  n = 0.181096
FEATURE [App::DocumentObjectGroupPython] Br_element001  label="Br_element : 0.762"  # scripted group (container) (typed FeaturePython)
  n = 0.761659
FEATURE [App::DocumentObjectGroupPython] G4_FREON_12B2  label="G4_FREON-12B2"  # scripted group (container) (typed FeaturePython)
  Dunit = g/cm3
  Dvalue = 1.8
  Group = -> [C_element044,F_element008,Br_element001]
  conduct = 2
  density = 1
  expand = 3
  formula = G4_FREON-12B2
  name = G4_FREON-12B2
  specific = 4
FEATURE [App::DocumentObjectGroupPython] C_element045  label="C_element : 0.115"  # scripted group (container) (typed FeaturePython)
  n = 0.114983
FEATURE [App::DocumentObjectGroupPython] F_element009  label="F_element : 0.546"  # scripted group (container) (typed FeaturePython)
  n = 0.545621
FEATURE [App::DocumentObjectGroupPython] Cl_element013  label="Cl_element : 0.339"  # scripted group (container) (typed FeaturePython)
  n = 0.339396
FEATURE [App::DocumentObjectGroupPython] G4_FREON_13  label="G4_FREON-13"  # scripted group (container) (typed FeaturePython)
  Dunit = g/cm3
  Dvalue = 0.95
  Group = -> [C_element045,F_element009,Cl_element013]
  conduct = 2
  density = 1
  expand = 3
  formula = G4_FREON-13
  name = G4_FREON-13
  specific = 4
FEATURE [App::DocumentObjectGroupPython] C_element046  label="C_element : 025"  # scripted group (container) (typed FeaturePython)
  n = 1
  ref = C_element
FEATURE [App::DocumentObjectGroupPython] F_element010  label="F_element : 3"  # scripted group (container) (typed FeaturePython)
  n = 3
  ref = F_element
FEATURE [App::DocumentObjectGroupPython] Br_element002  label="Br_element : 1"  # scripted group (container) (typed FeaturePython)
  n = 1
  ref = Br_element
FEATURE [App::DocumentObjectGroupPython] G4_FREON_13B1  label="G4_FREON-13B1"  # scripted group (container) (typed FeaturePython)
  Dunit = g/cm3
  Dvalue = 1.5
  Group = -> [C_element046,F_element010,Br_element002]
  conduct = 2
  density = 1
  expand = 3
  formula = G4_FREON-13B1
  name = G4_FREON-13B1
  specific = 4
FEATURE [App::DocumentObjectGroupPython] C_element047  label="C_element : 0.061"  # scripted group (container) (typed FeaturePython)
  n = 0.061309
FEATURE [App::DocumentObjectGroupPython] F_element011  label="F_element : 0.291"  # scripted group (container) (typed FeaturePython)
  n = 0.290924
FEATURE [App::DocumentObjectGroupPython] I_element002  label="I_element : 0.648"  # scripted group (container) (typed FeaturePython)
  n = 0.647767
FEATURE [App::DocumentObjectGroupPython] G4_FREON_13I1  label="G4_FREON-13I1"  # scripted group (container) (typed FeaturePython)
  Dunit = g/cm3
  Dvalue = 1.8
  Group = -> [C_element047,F_element011,I_element002]
  conduct = 2
  density = 1
  expand = 3
  formula = G4_FREON-13I1
  name = G4_FREON-13I1
  specific = 4
FEATURE [App::DocumentObjectGroupPython] Gd_element001  label="Gd_element : 2"  # scripted group (container) (typed FeaturePython)
  n = 2
  ref = Gd_element
FEATURE [App::DocumentObjectGroupPython] O_element041  label="O_element : 021"  # scripted group (container) (typed FeaturePython)
  n = 2
  ref = O_element
FEATURE [App::DocumentObjectGroupPython] S_element012  label="S_element : 004"  # scripted group (container) (typed FeaturePython)
  n = 1
  ref = S_element
FEATURE [App::DocumentObjectGroupPython] G4_GADOLINIUM_OXYSULFIDE  # scripted group (container) (typed FeaturePython)
  Dunit = g/cm3
  Dvalue = 7.44
  Group = -> [Gd_element001,O_element041,S_element012]
  conduct = 2
  density = 1
  expand = 3
  formula = G4_GADOLINIUM_OXYSULFIDE
  name = G4_GADOLINIUM_OXYSULFIDE
  specific = 4
FEATURE [App::DocumentObjectGroupPython] Ga_element001  label="Ga_element : 1"  # scripted group (container) (typed FeaturePython)
  n = 1
  ref = Ga_element
FEATURE [App::DocumentObjectGroupPython] As_element001  label="As_element : 1"  # scripted group (container) (typed FeaturePython)
  n = 1
  ref = As_element
FEATURE [App::DocumentObjectGroupPython] G4_GALLIUM_ARSENIDE  # scripted group (container) (typed FeaturePython)
  Dunit = g/cm3
  Dvalue = 5.31
  Group = -> [Ga_element001,As_element001]
  conduct = 2
  density = 1
  expand = 3
  formula = G4_GALLIUM_ARSENIDE
  name = G4_GALLIUM_ARSENIDE
  specific = 4
FEATURE [App::DocumentObjectGroupPython] H_element041  label="H_element : 0.081"  # scripted group (container) (typed FeaturePython)
  n = 0.08118
FEATURE [App::DocumentObjectGroupPython] C_element048  label="C_element : 0.416"  # scripted group (container) (typed FeaturePython)
  n = 0.41606
FEATURE [App::DocumentObjectGroupPython] N_element018  label="N_element : 0.111"  # scripted group (container) (typed FeaturePython)
  n = 0.11124
FEATURE [App::DocumentObjectGroupPython] O_element042  label="O_element : 0.381"  # scripted group (container) (typed FeaturePython)
  n = 0.38064
FEATURE [App::DocumentObjectGroupPython] S_element013  label="S_element : 0.011"  # scripted group (container) (typed FeaturePython)
  n = 0.01088
FEATURE [App::DocumentObjectGroupPython] G4_GEL_PHOTO_EMULSION  # scripted group (container) (typed FeaturePython)
  Dunit = g/cm3
  Dvalue = 1.2914
  Group = -> [H_element041,C_element048,N_element018,O_element042,S_element013]
  conduct = 2
  density = 1
  expand = 3
  formula = G4_GEL_PHOTO_EMULSION
  name = G4_GEL_PHOTO_EMULSION
  specific = 4
FEATURE [App::DocumentObjectGroupPython] B_element004  label="B_element : 0.040"  # scripted group (container) (typed FeaturePython)
  n = 0.0400639
FEATURE [App::DocumentObjectGroupPython] O_element043  label="O_element : 0.540"  # scripted group (container) (typed FeaturePython)
  n = 0.539561
FEATURE [App::DocumentObjectGroupPython] Na_element008  label="Na_element : 0.028"  # scripted group (container) (typed FeaturePython)
  n = 0.0281909
FEATURE [App::DocumentObjectGroupPython] Al_element003  label="Al_element : 0.012"  # scripted group (container) (typed FeaturePython)
  n = 0.011644
FEATURE [App::DocumentObjectGroupPython] Si_element003  label="Si_element : 0.377"  # scripted group (container) (typed FeaturePython)
  n = 0.377219
FEATURE [App::DocumentObjectGroupPython] K_element004  label="K_element : 0.014"  # scripted group (container) (typed FeaturePython)
  n = 0.00332099
FEATURE [App::DocumentObjectGroupPython] G4_Pyrex_Glass  # scripted group (container) (typed FeaturePython)
  Dunit = g/cm3
  Dvalue = 2.23
  Group = -> [B_element004,O_element043,Na_element008,Al_element003,Si_element003,K_element004]
  conduct = 2
  density = 1
  expand = 3
  formula = G4_Pyrex_Glass
  name = G4_Pyrex_Glass
  specific = 4
FEATURE [App::DocumentObjectGroupPython] O_element044  label="O_element : 0.156"  # scripted group (container) (typed FeaturePython)
  n = 0.156453
FEATURE [App::DocumentObjectGroupPython] Si_element004  label="Si_element : 0.081"  # scripted group (container) (typed FeaturePython)
  n = 0.080866
FEATURE [App::DocumentObjectGroupPython] Ti_element001  label="Ti_element : 0.008"  # scripted group (container) (typed FeaturePython)
  n = 0.008092
FEATURE [App::DocumentObjectGroupPython] As_element002  label="As_element : 0.003"  # scripted group (container) (typed FeaturePython)
  n = 0.002651
FEATURE [App::DocumentObjectGroupPython] Pb_element001  label="Pb_element : 0.752"  # scripted group (container) (typed FeaturePython)
  n = 0.751938
FEATURE [App::DocumentObjectGroupPython] G4_GLASS_LEAD  # scripted group (container) (typed FeaturePython)
  Dunit = g/cm3
  Dvalue = 6.22
  Group = -> [O_element044,Si_element004,Ti_element001,As_element002,Pb_element001]
  conduct = 2
  density = 1
  expand = 3
  formula = G4_GLASS_LEAD
  name = G4_GLASS_LEAD
  specific = 4
FEATURE [App::DocumentObjectGroupPython] O_element045  label="O_element : 0.460"  # scripted group (container) (typed FeaturePython)
  n = 0.4598
FEATURE [App::DocumentObjectGroupPython] Na_element009  label="Na_element : 0.096"  # scripted group (container) (typed FeaturePython)
  n = 0.0964411
FEATURE [App::DocumentObjectGroupPython] Si_element005  label="Si_element : 0.378"  # scripted group (container) (typed FeaturePython)
  n = 0.336553
FEATURE [App::DocumentObjectGroupPython] Ca_element011  label="Ca_element : 0.107"  # scripted group (container) (typed FeaturePython)
  n = 0.107205
FEATURE [App::DocumentObjectGroupPython] G4_GLASS_PLATE  # scripted group (container) (typed FeaturePython)
  Dunit = g/cm3
  Dvalue = 2.4
  Group = -> [O_element045,Na_element009,Si_element005,Ca_element011]
  conduct = 2
  density = 1
  expand = 3
  formula = G4_GLASS_PLATE
  name = G4_GLASS_PLATE
  specific = 4
FEATURE [App::DocumentObjectGroupPython] C_element049  label="C_element : 026"  # scripted group (container) (typed FeaturePython)
  n = 5
  ref = C_element
FEATURE [App::DocumentObjectGroupPython] H_element042  label="H_element : 021"  # scripted group (container) (typed FeaturePython)
  n = 10
  ref = H_element
FEATURE [App::DocumentObjectGroupPython] N_element019  label="N_element : 2"  # scripted group (container) (typed FeaturePython)
  n = 2
  ref = N_element
FEATURE [App::DocumentObjectGroupPython] O_element046  label="O_element : 022"  # scripted group (container) (typed FeaturePython)
  n = 3
  ref = O_element
FEATURE [App::DocumentObjectGroupPython] G4_GLUTAMINE  # scripted group (container) (typed FeaturePython)
  Dunit = g/cm3
  Dvalue = 1.46
  Group = -> [C_element049,H_element042,N_element019,O_element046]
  conduct = 2
  density = 1
  expand = 3
  formula = G4_GLUTAMINE
  name = G4_GLUTAMINE
  specific = 4
FEATURE [App::DocumentObjectGroupPython] C_element050  label="C_element : 027"  # scripted group (container) (typed FeaturePython)
  n = 3
  ref = C_element
FEATURE [App::DocumentObjectGroupPython] H_element043  label="H_element : 022"  # scripted group (container) (typed FeaturePython)
  n = 8
  ref = H_element
FEATURE [App::DocumentObjectGroupPython] O_element047  label="O_element : 023"  # scripted group (container) (typed FeaturePython)
  n = 3
  ref = O_element
FEATURE [App::DocumentObjectGroupPython] G4_GLYCEROL  # scripted group (container) (typed FeaturePython)
  Dunit = g/cm3
  Dvalue = 1.2613
  Group = -> [C_element050,H_element043,O_element047]
  conduct = 2
  density = 1
  expand = 3
  formula = G4_GLYCEROL
  name = G4_GLYCEROL
  specific = 4
FEATURE [App::DocumentObjectGroupPython] C_element051  label="C_element : 028"  # scripted group (container) (typed FeaturePython)
  n = 5
  ref = C_element
FEATURE [App::DocumentObjectGroupPython] H_element044  label="H_element : 023"  # scripted group (container) (typed FeaturePython)
  n = 5
  ref = H_element
FEATURE [App::DocumentObjectGroupPython] N_element020  label="N_element : 009"  # scripted group (container) (typed FeaturePython)
  n = 5
  ref = N_element
FEATURE [App::DocumentObjectGroupPython] O_element048  label="O_element : 024"  # scripted group (container) (typed FeaturePython)
  n = 1
  ref = O_element
FEATURE [App::DocumentObjectGroupPython] G4_GUANINE  # scripted group (container) (typed FeaturePython)
  Dunit = g/cm3
  Dvalue = 2.2
  Group = -> [C_element051,H_element044,N_element020,O_element048]
  conduct = 2
  density = 1
  expand = 3
  formula = G4_GUANINE
  name = G4_GUANINE
  specific = 4
FEATURE [App::DocumentObjectGroupPython] Ca_element012  label="Ca_element : 006"  # scripted group (container) (typed FeaturePython)
  n = 1
  ref = Ca_element
FEATURE [App::DocumentObjectGroupPython] S_element014  label="S_element : 005"  # scripted group (container) (typed FeaturePython)
  n = 1
  ref = S_element
FEATURE [App::DocumentObjectGroupPython] O_element049  label="O_element : 6"  # scripted group (container) (typed FeaturePython)
  n = 6
  ref = O_element
FEATURE [App::DocumentObjectGroupPython] H_element045  label="H_element : 024"  # scripted group (container) (typed FeaturePython)
  n = 4
  ref = H_element
FEATURE [App::DocumentObjectGroupPython] G4_GYPSUM  # scripted group (container) (typed FeaturePython)
  Dunit = g/cm3
  Dvalue = 2.32
  Group = -> [Ca_element012,S_element014,O_element049,H_element045]
  conduct = 2
  density = 1
  expand = 3
  formula = G4_GYPSUM
  name = G4_GYPSUM
  specific = 4
FEATURE [App::DocumentObjectGroupPython] C_element052  label="C_element : 7"  # scripted group (container) (typed FeaturePython)
  n = 7
  ref = C_element
FEATURE [App::DocumentObjectGroupPython] H_element046  label="H_element : 16"  # scripted group (container) (typed FeaturePython)
  n = 16
  ref = H_element
FEATURE [App::DocumentObjectGroupPython] G4_N_HEPTANE  label="G4_N-HEPTANE"  # scripted group (container) (typed FeaturePython)
  Dunit = g/cm3
  Dvalue = 0.68376
  Group = -> [C_element052,H_element046]
  conduct = 2
  density = 1
  expand = 3
  formula = G4_N-HEPTANE
  name = G4_N-HEPTANE
  specific = 4
FEATURE [App::DocumentObjectGroupPython] C_element053  label="C_element : 029"  # scripted group (container) (typed FeaturePython)
  n = 6
  ref = C_element
FEATURE [App::DocumentObjectGroupPython] H_element047  label="H_element : 14"  # scripted group (container) (typed FeaturePython)
  n = 14
  ref = H_element
FEATURE [App::DocumentObjectGroupPython] G4_N_HEXANE  label="G4_N-HEXANE"  # scripted group (container) (typed FeaturePython)
  Dunit = g/cm3
  Dvalue = 0.6603
  Group = -> [C_element053,H_element047]
  conduct = 2
  density = 1
  expand = 3
  formula = G4_N-HEXANE
  name = G4_N-HEXANE
  specific = 4
FEATURE [App::DocumentObjectGroupPython] C_element054  label="C_element : 22"  # scripted group (container) (typed FeaturePython)
  n = 22
  ref = C_element
FEATURE [App::DocumentObjectGroupPython] H_element048  label="H_element : 025"  # scripted group (container) (typed FeaturePython)
  n = 10
  ref = H_element
FEATURE [App::DocumentObjectGroupPython] N_element021  label="N_element : 010"  # scripted group (container) (typed FeaturePython)
  n = 2
  ref = N_element
FEATURE [App::DocumentObjectGroupPython] O_element050  label="O_element : 025"  # scripted group (container) (typed FeaturePython)
  n = 5
  ref = O_element
FEATURE [App::DocumentObjectGroupPython] G4_KAPTON  # scripted group (container) (typed FeaturePython)
  Dunit = g/cm3
  Dvalue = 1.42
  Group = -> [C_element054,H_element048,N_element021,O_element050]
  conduct = 2
  density = 1
  expand = 3
  formula = G4_KAPTON
  name = G4_KAPTON
  specific = 4
FEATURE [App::DocumentObjectGroupPython] La_element001  label="La_element : 1"  # scripted group (container) (typed FeaturePython)
  n = 1
  ref = La_element
FEATURE [App::DocumentObjectGroupPython] Br_element003  label="Br_element : 002"  # scripted group (container) (typed FeaturePython)
  n = 1
  ref = Br_element
FEATURE [App::DocumentObjectGroupPython] O_element051  label="O_element : 026"  # scripted group (container) (typed FeaturePython)
  n = 1
  ref = O_element
FEATURE [App::DocumentObjectGroupPython] G4_LANTHANUM_OXYBROMIDE  # scripted group (container) (typed FeaturePython)
  Dunit = g/cm3
  Dvalue = 6.28
  Group = -> [La_element001,Br_element003,O_element051]
  conduct = 2
  density = 1
  expand = 3
  formula = G4_LANTHANUM_OXYBROMIDE
  name = G4_LANTHANUM_OXYBROMIDE
  specific = 4
FEATURE [App::DocumentObjectGroupPython] La_element002  label="La_element : 2"  # scripted group (container) (typed FeaturePython)
  n = 2
  ref = La_element
FEATURE [App::DocumentObjectGroupPython] O_element052  label="O_element : 027"  # scripted group (container) (typed FeaturePython)
  n = 2
  ref = O_element
FEATURE [App::DocumentObjectGroupPython] S_element015  label="S_element : 006"  # scripted group (container) (typed FeaturePython)
  n = 1
  ref = S_element
FEATURE [App::DocumentObjectGroupPython] G4_LANTHANUM_OXYSULFIDE  # scripted group (container) (typed FeaturePython)
  Dunit = g/cm3
  Dvalue = 5.86
  Group = -> [La_element002,O_element052,S_element015]
  conduct = 2
  density = 1
  expand = 3
  formula = G4_LANTHANUM_OXYSULFIDE
  name = G4_LANTHANUM_OXYSULFIDE
  specific = 4
FEATURE [App::DocumentObjectGroupPython] O_element053  label="O_element : 0.072"  # scripted group (container) (typed FeaturePython)
  n = 0.071682
FEATURE [App::DocumentObjectGroupPython] Pb_element002  label="Pb_element : 0.928"  # scripted group (container) (typed FeaturePython)
  n = 0.928318
FEATURE [App::DocumentObjectGroupPython] G4_LEAD_OXIDE  # scripted group (container) (typed FeaturePython)
  Dunit = g/cm3
  Dvalue = 9.53
  Group = -> [O_element053,Pb_element002]
  conduct = 2
  density = 1
  expand = 3
  formula = G4_LEAD_OXIDE
  name = G4_LEAD_OXIDE
  specific = 4
FEATURE [App::DocumentObjectGroupPython] Li_element001  label="Li_element : 1"  # scripted group (container) (typed FeaturePython)
  n = 1
  ref = Li_element
FEATURE [App::DocumentObjectGroupPython] N_element022  label="N_element : 011"  # scripted group (container) (typed FeaturePython)
  n = 1
  ref = N_element
FEATURE [App::DocumentObjectGroupPython] H_element049  label="H_element : 026"  # scripted group (container) (typed FeaturePython)
  n = 2
  ref = H_element
FEATURE [App::DocumentObjectGroupPython] G4_LITHIUM_AMIDE  # scripted group (container) (typed FeaturePython)
  Dunit = g/cm3
  Dvalue = 1.178
  Group = -> [Li_element001,N_element022,H_element049]
  conduct = 2
  density = 1
  expand = 3
  formula = G4_LITHIUM_AMIDE
  name = G4_LITHIUM_AMIDE
  specific = 4
FEATURE [App::DocumentObjectGroupPython] Li_element002  label="Li_element : 2"  # scripted group (container) (typed FeaturePython)
  n = 2
  ref = Li_element
FEATURE [App::DocumentObjectGroupPython] C_element055  label="C_element : 030"  # scripted group (container) (typed FeaturePython)
  n = 1
  ref = C_element
FEATURE [App::DocumentObjectGroupPython] O_element054  label="O_element : 028"  # scripted group (container) (typed FeaturePython)
  n = 3
  ref = O_element
FEATURE [App::DocumentObjectGroupPython] G4_LITHIUM_CARBONATE  # scripted group (container) (typed FeaturePython)
  Dunit = g/cm3
  Dvalue = 2.11
  Group = -> [Li_element002,C_element055,O_element054]
  conduct = 2
  density = 1
  expand = 3
  formula = G4_LITHIUM_CARBONATE
  name = G4_LITHIUM_CARBONATE
  specific = 4
FEATURE [App::DocumentObjectGroupPython] Li_element003  label="Li_element : 003"  # scripted group (container) (typed FeaturePython)
  n = 1
  ref = Li_element
FEATURE [App::DocumentObjectGroupPython] F_element012  label="F_element : 004"  # scripted group (container) (typed FeaturePython)
  n = 1
  ref = F_element
FEATURE [App::DocumentObjectGroupPython] G4_LITHIUM_FLUORIDE  # scripted group (container) (typed FeaturePython)
  Dunit = g/cm3
  Dvalue = 2.635
  Group = -> [Li_element003,F_element012]
  conduct = 2
  density = 1
  expand = 3
  formula = G4_LITHIUM_FLUORIDE
  name = G4_LITHIUM_FLUORIDE
  specific = 4
FEATURE [App::DocumentObjectGroupPython] Li_element004  label="Li_element : 004"  # scripted group (container) (typed FeaturePython)
  n = 1
  ref = Li_element
FEATURE [App::DocumentObjectGroupPython] H_element050  label="H_element : 027"  # scripted group (container) (typed FeaturePython)
  n = 1
  ref = H_element
FEATURE [App::DocumentObjectGroupPython] G4_LITHIUM_HYDRIDE  # scripted group (container) (typed FeaturePython)
  Dunit = g/cm3
  Dvalue = 0.82
  Group = -> [Li_element004,H_element050]
  conduct = 2
  density = 1
  expand = 3
  formula = G4_LITHIUM_HYDRIDE
  name = G4_LITHIUM_HYDRIDE
  specific = 4
FEATURE [App::DocumentObjectGroupPython] Li_element005  label="Li_element : 005"  # scripted group (container) (typed FeaturePython)
  n = 1
  ref = Li_element
FEATURE [App::DocumentObjectGroupPython] I_element003  label="I_element : 002"  # scripted group (container) (typed FeaturePython)
  n = 1
  ref = I_element
FEATURE [App::DocumentObjectGroupPython] G4_LITHIUM_IODIDE  # scripted group (container) (typed FeaturePython)
  Dunit = g/cm3
  Dvalue = 3.494
  Group = -> [Li_element005,I_element003]
  conduct = 2
  density = 1
  expand = 3
  formula = G4_LITHIUM_IODIDE
  name = G4_LITHIUM_IODIDE
  specific = 4
FEATURE [App::DocumentObjectGroupPython] Li_element006  label="Li_element : 006"  # scripted group (container) (typed FeaturePython)
  n = 2
  ref = Li_element
FEATURE [App::DocumentObjectGroupPython] O_element055  label="O_element : 029"  # scripted group (container) (typed FeaturePython)
  n = 1
  ref = O_element
FEATURE [App::DocumentObjectGroupPython] G4_LITHIUM_OXIDE  # scripted group (container) (typed FeaturePython)
  Dunit = g/cm3
  Dvalue = 2.013
  Group = -> [Li_element006,O_element055]
  conduct = 2
  density = 1
  expand = 3
  formula = G4_LITHIUM_OXIDE
  name = G4_LITHIUM_OXIDE
  specific = 4
FEATURE [App::DocumentObjectGroupPython] Li_element007  label="Li_element : 007"  # scripted group (container) (typed FeaturePython)
  n = 2
  ref = Li_element
FEATURE [App::DocumentObjectGroupPython] B_element005  label="B_element : 005"  # scripted group (container) (typed FeaturePython)
  n = 4
  ref = B_element
FEATURE [App::DocumentObjectGroupPython] O_element056  label="O_element : 7"  # scripted group (container) (typed FeaturePython)
  n = 7
  ref = O_element
FEATURE [App::DocumentObjectGroupPython] G4_LITHIUM_TETRABORATE  # scripted group (container) (typed FeaturePython)
  Dunit = g/cm3
  Dvalue = 2.44
  Group = -> [Li_element007,B_element005,O_element056]
  conduct = 2
  density = 1
  expand = 3
  formula = G4_LITHIUM_TETRABORATE
  name = G4_LITHIUM_TETRABORATE
  specific = 4
FEATURE [App::DocumentObjectGroupPython] H_element051  label="H_element : 0.105"  # scripted group (container) (typed FeaturePython)
  n = 0.105
FEATURE [App::DocumentObjectGroupPython] C_element056  label="C_element : 0.083"  # scripted group (container) (typed FeaturePython)
  n = 0.083
FEATURE [App::DocumentObjectGroupPython] N_element023  label="N_element : 0.023"  # scripted group (container) (typed FeaturePython)
  n = 0.023
FEATURE [App::DocumentObjectGroupPython] O_element057  label="O_element : 0.779"  # scripted group (container) (typed FeaturePython)
  n = 0.779
FEATURE [App::DocumentObjectGroupPython] Na_element010  label="Na_element : 0.097"  # scripted group (container) (typed FeaturePython)
  n = 0.002
FEATURE [App::DocumentObjectGroupPython] P_element006  label="P_element : 0.105"  # scripted group (container) (typed FeaturePython)
  n = 0.001
FEATURE [App::DocumentObjectGroupPython] S_element016  label="S_element : 0.017"  # scripted group (container) (typed FeaturePython)
  n = 0.002
FEATURE [App::DocumentObjectGroupPython] Cl_element014  label="Cl_element : 0.587"  # scripted group (container) (typed FeaturePython)
  n = 0.003
FEATURE [App::DocumentObjectGroupPython] K_element005  label="K_element : 0.015"  # scripted group (container) (typed FeaturePython)
  n = 0.002
FEATURE [App::DocumentObjectGroupPython] G4_LUNG_ICRP  # scripted group (container) (typed FeaturePython)
  Dunit = g/cm3
  Dvalue = 1.04
  Group = -> [H_element051,C_element056,N_element023,O_element057,Na_element010,P_element006,S_element016,Cl_element014,K_element005]
  conduct = 2
  density = 1
  expand = 3
  formula = G4_LUNG_ICRP
  name = G4_LUNG_ICRP
  specific = 4
FEATURE [App::DocumentObjectGroupPython] H_element052  label="H_element : 0.116"  # scripted group (container) (typed FeaturePython)
  n = 0.114318
FEATURE [App::DocumentObjectGroupPython] C_element057  label="C_element : 0.656"  # scripted group (container) (typed FeaturePython)
  n = 0.655824
FEATURE [App::DocumentObjectGroupPython] O_element058  label="O_element : 0.092"  # scripted group (container) (typed FeaturePython)
  n = 0.0921831
FEATURE [App::DocumentObjectGroupPython] Mg_element004  label="Mg_element : 0.135"  # scripted group (container) (typed FeaturePython)
  n = 0.134792
FEATURE [App::DocumentObjectGroupPython] Ca_element013  label="Ca_element : 0.003"  # scripted group (container) (typed FeaturePython)
  n = 0.002883
FEATURE [App::DocumentObjectGroupPython] G4_M3_WAX  # scripted group (container) (typed FeaturePython)
  Dunit = g/cm3
  Dvalue = 1.05
  Group = -> [H_element052,C_element057,O_element058,Mg_element004,Ca_element013]
  conduct = 2
  density = 1
  expand = 3
  formula = G4_M3_WAX
  name = G4_M3_WAX
  specific = 4
FEATURE [App::DocumentObjectGroupPython] Mg_element005  label="Mg_element : 1"  # scripted group (container) (typed FeaturePython)
  n = 1
  ref = Mg_element
FEATURE [App::DocumentObjectGroupPython] C_element058  label="C_element : 031"  # scripted group (container) (typed FeaturePython)
  n = 1
  ref = C_element
FEATURE [App::DocumentObjectGroupPython] O_element059  label="O_element : 030"  # scripted group (container) (typed FeaturePython)
  n = 3
  ref = O_element
FEATURE [App::DocumentObjectGroupPython] G4_MAGNESIUM_CARBONATE  # scripted group (container) (typed FeaturePython)
  Dunit = g/cm3
  Dvalue = 2.958
  Group = -> [Mg_element005,C_element058,O_element059]
  conduct = 2
  density = 1
  expand = 3
  formula = G4_MAGNESIUM_CARBONATE
  name = G4_MAGNESIUM_CARBONATE
  specific = 4
FEATURE [App::DocumentObjectGroupPython] Mg_element006  label="Mg_element : 002"  # scripted group (container) (typed FeaturePython)
  n = 1
  ref = Mg_element
FEATURE [App::DocumentObjectGroupPython] F_element013  label="F_element : 005"  # scripted group (container) (typed FeaturePython)
  n = 2
  ref = F_element
FEATURE [App::DocumentObjectGroupPython] G4_MAGNESIUM_FLUORIDE  # scripted group (container) (typed FeaturePython)
  Dunit = g/cm3
  Dvalue = 3
  Group = -> [Mg_element006,F_element013]
  conduct = 2
  density = 1
  expand = 3
  formula = G4_MAGNESIUM_FLUORIDE
  name = G4_MAGNESIUM_FLUORIDE
  specific = 4
FEATURE [App::DocumentObjectGroupPython] Mg_element007  label="Mg_element : 003"  # scripted group (container) (typed FeaturePython)
  n = 1
  ref = Mg_element
FEATURE [App::DocumentObjectGroupPython] O_element060  label="O_element : 031"  # scripted group (container) (typed FeaturePython)
  n = 1
  ref = O_element
FEATURE [App::DocumentObjectGroupPython] G4_MAGNESIUM_OXIDE  # scripted group (container) (typed FeaturePython)
  Dunit = g/cm3
  Dvalue = 3.58
  Group = -> [Mg_element007,O_element060]
  conduct = 2
  density = 1
  expand = 3
  formula = G4_MAGNESIUM_OXIDE
  name = G4_MAGNESIUM_OXIDE
  specific = 4
FEATURE [App::DocumentObjectGroupPython] Mg_element008  label="Mg_element : 004"  # scripted group (container) (typed FeaturePython)
  n = 1
  ref = Mg_element
FEATURE [App::DocumentObjectGroupPython] B_element006  label="B_element : 006"  # scripted group (container) (typed FeaturePython)
  n = 4
  ref = B_element
FEATURE [App::DocumentObjectGroupPython] O_element061  label="O_element : 032"  # scripted group (container) (typed FeaturePython)
  n = 7
  ref = O_element
FEATURE [App::DocumentObjectGroupPython] G4_MAGNESIUM_TETRABORATE  # scripted group (container) (typed FeaturePython)
  Dunit = g/cm3
  Dvalue = 2.53
  Group = -> [Mg_element008,B_element006,O_element061]
  conduct = 2
  density = 1
  expand = 3
  formula = G4_MAGNESIUM_TETRABORATE
  name = G4_MAGNESIUM_TETRABORATE
  specific = 4
FEATURE [App::DocumentObjectGroupPython] Hg_element001  label="Hg_element : 1"  # scripted group (container) (typed FeaturePython)
  n = 1
  ref = Hg_element
FEATURE [App::DocumentObjectGroupPython] I_element004  label="I_element : 2"  # scripted group (container) (typed FeaturePython)
  n = 2
  ref = I_element
FEATURE [App::DocumentObjectGroupPython] G4_MERCURIC_IODIDE  # scripted group (container) (typed FeaturePython)
  Dunit = g/cm3
  Dvalue = 6.36
  Group = -> [Hg_element001,I_element004]
  conduct = 2
  density = 1
  expand = 3
  formula = G4_MERCURIC_IODIDE
  name = G4_MERCURIC_IODIDE
  specific = 4
FEATURE [App::DocumentObjectGroupPython] C_element059  label="C_element : 032"  # scripted group (container) (typed FeaturePython)
  n = 1
  ref = C_element
FEATURE [App::DocumentObjectGroupPython] H_element053  label="H_element : 028"  # scripted group (container) (typed FeaturePython)
  n = 4
  ref = H_element
FEATURE [App::DocumentObjectGroupPython] G4_METHANE  # scripted group (container) (typed FeaturePython)
  Dunit = g/cm3
  Dvalue = 0.000667151
  Group = -> [C_element059,H_element053]
  conduct = 2
  density = 1
  expand = 3
  formula = G4_METHANE
  name = G4_METHANE
  specific = 4
FEATURE [App::DocumentObjectGroupPython] C_element060  label="C_element : 033"  # scripted group (container) (typed FeaturePython)
  n = 1
  ref = C_element
FEATURE [App::DocumentObjectGroupPython] H_element054  label="H_element : 029"  # scripted group (container) (typed FeaturePython)
  n = 4
  ref = H_element
FEATURE [App::DocumentObjectGroupPython] O_element062  label="O_element : 033"  # scripted group (container) (typed FeaturePython)
  n = 1
  ref = O_element
FEATURE [App::DocumentObjectGroupPython] G4_METHANOL  # scripted group (container) (typed FeaturePython)
  Dunit = g/cm3
  Dvalue = 0.7914
  Group = -> [C_element060,H_element054,O_element062]
  conduct = 2
  density = 1
  expand = 3
  formula = G4_METHANOL
  name = G4_METHANOL
  specific = 4
FEATURE [App::DocumentObjectGroupPython] H_element055  label="H_element : 0.134"  # scripted group (container) (typed FeaturePython)
  n = 0.13404
FEATURE [App::DocumentObjectGroupPython] C_element061  label="C_element : 0.778"  # scripted group (container) (typed FeaturePython)
  n = 0.77796
FEATURE [App::DocumentObjectGroupPython] O_element063  label="O_element : 0.035"  # scripted group (container) (typed FeaturePython)
  n = 0.03502
FEATURE [App::DocumentObjectGroupPython] Mg_element009  label="Mg_element : 0.039"  # scripted group (container) (typed FeaturePython)
  n = 0.038594
FEATURE [App::DocumentObjectGroupPython] Ti_element002  label="Ti_element : 0.014"  # scripted group (container) (typed FeaturePython)
  n = 0.014386
FEATURE [App::DocumentObjectGroupPython] G4_MIX_D_WAX  # scripted group (container) (typed FeaturePython)
  Dunit = g/cm3
  Dvalue = 0.99
  Group = -> [H_element055,C_element061,O_element063,Mg_element009,Ti_element002]
  conduct = 2
  density = 1
  expand = 3
  formula = G4_MIX_D_WAX
  name = G4_MIX_D_WAX
  specific = 4
FEATURE [App::DocumentObjectGroupPython] H_element056  label="H_element : 0.135"  # scripted group (container) (typed FeaturePython)
  n = 0.081192
FEATURE [App::DocumentObjectGroupPython] C_element062  label="C_element : 0.583"  # scripted group (container) (typed FeaturePython)
  n = 0.583442
FEATURE [App::DocumentObjectGroupPython] N_element024  label="N_element : 0.018"  # scripted group (container) (typed FeaturePython)
  n = 0.017798
FEATURE [App::DocumentObjectGroupPython] O_element064  label="O_element : 0.186"  # scripted group (container) (typed FeaturePython)
  n = 0.186381
FEATURE [App::DocumentObjectGroupPython] Mg_element010  label="Mg_element : 0.130"  # scripted group (container) (typed FeaturePython)
  n = 0.130287
FEATURE [App::DocumentObjectGroupPython] Cl_element015  label="Cl_element : 0.588"  # scripted group (container) (typed FeaturePython)
  n = 0.0009
FEATURE [App::DocumentObjectGroupPython] G4_MS20_TISSUE  # scripted group (container) (typed FeaturePython)
  Dunit = g/cm3
  Dvalue = 1
  Group = -> [H_element056,C_element062,N_element024,O_element064,Mg_element010,Cl_element015]
  conduct = 2
  density = 1
  expand = 3
  formula = G4_MS20_TISSUE
  name = G4_MS20_TISSUE
  specific = 4
FEATURE [App::DocumentObjectGroupPython] H_element057  label="H_element : 0.136"  # scripted group (container) (typed FeaturePython)
  n = 0.102
FEATURE [App::DocumentObjectGroupPython] C_element063  label="C_element : 0.143"  # scripted group (container) (typed FeaturePython)
  n = 0.143
FEATURE [App::DocumentObjectGroupPython] N_element025  label="N_element : 0.034"  # scripted group (container) (typed FeaturePython)
  n = 0.034
FEATURE [App::DocumentObjectGroupPython] O_element065  label="O_element : 0.710"  # scripted group (container) (typed FeaturePython)
  n = 0.71
FEATURE [App::DocumentObjectGroupPython] Na_element011  label="Na_element : 0.098"  # scripted group (container) (typed FeaturePython)
  n = 0.001
FEATURE [App::DocumentObjectGroupPython] P_element007  label="P_element : 0.002"  # scripted group (container) (typed FeaturePython)
  n = 0.002
FEATURE [App::DocumentObjectGroupPython] S_element017  label="S_element : 0.018"  # scripted group (container) (typed FeaturePython)
  n = 0.003
FEATURE [App::DocumentObjectGroupPython] Cl_element016  label="Cl_element : 0.589"  # scripted group (container) (typed FeaturePython)
  n = 0.001
FEATURE [App::DocumentObjectGroupPython] K_element006  label="K_element : 0.004"  # scripted group (container) (typed FeaturePython)
  n = 0.004
FEATURE [App::DocumentObjectGroupPython] G4_MUSCLE_SKELETAL_ICRP  # scripted group (container) (typed FeaturePython)
  Dunit = g/cm3
  Dvalue = 1.05
  Group = -> [H_element057,C_element063,N_element025,O_element065,Na_element011,P_element007,S_element017,Cl_element016,K_element006]
  conduct = 2
  density = 1
  expand = 3
  formula = G4_MUSCLE_SKELETAL_ICRP
  name = G4_MUSCLE_SKELETAL_ICRP
  specific = 4
FEATURE [App::DocumentObjectGroupPython] H_element058  label="H_element : 0.137"  # scripted group (container) (typed FeaturePython)
  n = 0.102102
FEATURE [App::DocumentObjectGroupPython] C_element064  label="C_element : 0.123"  # scripted group (container) (typed FeaturePython)
  n = 0.123123
FEATURE [App::DocumentObjectGroupPython] N_element026  label="N_element : 0.756"  # scripted group (container) (typed FeaturePython)
  n = 0.035035
FEATURE [App::DocumentObjectGroupPython] O_element066  label="O_element : 0.730"  # scripted group (container) (typed FeaturePython)
  n = 0.72973
FEATURE [App::DocumentObjectGroupPython] Na_element012  label="Na_element : 0.099"  # scripted group (container) (typed FeaturePython)
  n = 0.001001
FEATURE [App::DocumentObjectGroupPython] P_element008  label="P_element : 0.106"  # scripted group (container) (typed FeaturePython)
  n = 0.002002
FEATURE [App::DocumentObjectGroupPython] S_element018  label="S_element : 0.019"  # scripted group (container) (typed FeaturePython)
  n = 0.004004
FEATURE [App::DocumentObjectGroupPython] K_element007  label="K_element : 0.016"  # scripted group (container) (typed FeaturePython)
  n = 0.003003
FEATURE [App::DocumentObjectGroupPython] G4_MUSCLE_STRIATED_ICRU  # scripted group (container) (typed FeaturePython)
  Dunit = g/cm3
  Dvalue = 1.04
  Group = -> [H_element058,C_element064,N_element026,O_element066,Na_element012,P_element008,S_element018,K_element007]
  conduct = 2
  density = 1
  expand = 3
  formula = G4_MUSCLE_STRIATED_ICRU
  name = G4_MUSCLE_STRIATED_ICRU
  specific = 4
FEATURE [App::DocumentObjectGroupPython] H_element059  label="H_element : 0.098"  # scripted group (container) (typed FeaturePython)
  n = 0.0982341
FEATURE [App::DocumentObjectGroupPython] C_element065  label="C_element : 0.156"  # scripted group (container) (typed FeaturePython)
  n = 0.156214
FEATURE [App::DocumentObjectGroupPython] N_element027  label="N_element : 0.757"  # scripted group (container) (typed FeaturePython)
  n = 0.035451
FEATURE [App::DocumentObjectGroupPython] O_element067  label="O_element : 0.880"  # scripted group (container) (typed FeaturePython)
  n = 0.710101
FEATURE [App::DocumentObjectGroupPython] G4_MUSCLE_WITH_SUCROSE  # scripted group (container) (typed FeaturePython)
  Dunit = g/cm3
  Dvalue = 1.11
  Group = -> [H_element059,C_element065,N_element027,O_element067]
  conduct = 2
  density = 1
  expand = 3
  formula = G4_MUSCLE_WITH_SUCROSE
  name = G4_MUSCLE_WITH_SUCROSE
  specific = 4
FEATURE [App::DocumentObjectGroupPython] H_element060  label="H_element : 0.138"  # scripted group (container) (typed FeaturePython)
  n = 0.101969
FEATURE [App::DocumentObjectGroupPython] C_element066  label="C_element : 0.120"  # scripted group (container) (typed FeaturePython)
  n = 0.120058
FEATURE [App::DocumentObjectGroupPython] N_element028  label="N_element : 0.758"  # scripted group (container) (typed FeaturePython)
  n = 0.035451
FEATURE [App::DocumentObjectGroupPython] O_element068  label="O_element : 0.743"  # scripted group (container) (typed FeaturePython)
  n = 0.742522
FEATURE [App::DocumentObjectGroupPython] G4_MUSCLE_WITHOUT_SUCROSE  # scripted group (container) (typed FeaturePython)
  Dunit = g/cm3
  Dvalue = 1.07
  Group = -> [H_element060,C_element066,N_element028,O_element068]
  conduct = 2
  density = 1
  expand = 3
  formula = G4_MUSCLE_WITHOUT_SUCROSE
  name = G4_MUSCLE_WITHOUT_SUCROSE
  specific = 4
FEATURE [App::DocumentObjectGroupPython] C_element067  label="C_element : 10"  # scripted group (container) (typed FeaturePython)
  n = 10
  ref = C_element
FEATURE [App::DocumentObjectGroupPython] H_element061  label="H_element : 030"  # scripted group (container) (typed FeaturePython)
  n = 8
  ref = H_element
FEATURE [App::DocumentObjectGroupPython] G4_NAPHTHALENE  # scripted group (container) (typed FeaturePython)
  Dunit = g/cm3
  Dvalue = 1.145
  Group = -> [C_element067,H_element061]
  conduct = 2
  density = 1
  expand = 3
  formula = G4_NAPHTHALENE
  name = G4_NAPHTHALENE
  specific = 4
FEATURE [App::DocumentObjectGroupPython] C_element068  label="C_element : 034"  # scripted group (container) (typed FeaturePython)
  n = 6
  ref = C_element
FEATURE [App::DocumentObjectGroupPython] H_element062  label="H_element : 031"  # scripted group (container) (typed FeaturePython)
  n = 5
  ref = H_element
FEATURE [App::DocumentObjectGroupPython] N_element029  label="N_element : 012"  # scripted group (container) (typed FeaturePython)
  n = 1
  ref = N_element
FEATURE [App::DocumentObjectGroupPython] O_element069  label="O_element : 034"  # scripted group (container) (typed FeaturePython)
  n = 2
  ref = O_element
FEATURE [App::DocumentObjectGroupPython] G4_NITROBENZENE  # scripted group (container) (typed FeaturePython)
  Dunit = g/cm3
  Dvalue = 1.19867
  Group = -> [C_element068,H_element062,N_element029,O_element069]
  conduct = 2
  density = 1
  expand = 3
  formula = G4_NITROBENZENE
  name = G4_NITROBENZENE
  specific = 4
FEATURE [App::DocumentObjectGroupPython] N_element030  label="N_element : 013"  # scripted group (container) (typed FeaturePython)
  n = 2
  ref = N_element
FEATURE [App::DocumentObjectGroupPython] O_element070  label="O_element : 035"  # scripted group (container) (typed FeaturePython)
  n = 1
  ref = O_element
FEATURE [App::DocumentObjectGroupPython] G4_NITROUS_OXIDE  # scripted group (container) (typed FeaturePython)
  Dunit = g/cm3
  Dvalue = 0.00183094
  Group = -> [N_element030,O_element070]
  conduct = 2
  density = 1
  expand = 3
  formula = G4_NITROUS_OXIDE
  name = G4_NITROUS_OXIDE
  specific = 4
FEATURE [App::DocumentObjectGroupPython] H_element063  label="H_element : 0.104"  # scripted group (container) (typed FeaturePython)
  n = 0.103509
FEATURE [App::DocumentObjectGroupPython] C_element069  label="C_element : 0.648"  # scripted group (container) (typed FeaturePython)
  n = 0.648416
FEATURE [App::DocumentObjectGroupPython] N_element031  label="N_element : 0.100"  # scripted group (container) (typed FeaturePython)
  n = 0.0995361
FEATURE [App::DocumentObjectGroupPython] O_element071  label="O_element : 0.149"  # scripted group (container) (typed FeaturePython)
  n = 0.148539
FEATURE [App::DocumentObjectGroupPython] G4_NYLON_8062  label="G4_NYLON-8062"  # scripted group (container) (typed FeaturePython)
  Dunit = g/cm3
  Dvalue = 1.08
  Group = -> [H_element063,C_element069,N_element031,O_element071]
  conduct = 2
  density = 1
  expand = 3
  formula = G4_NYLON-8062
  name = G4_NYLON-8062
  specific = 4
FEATURE [App::DocumentObjectGroupPython] C_element070  label="C_element : 035"  # scripted group (container) (typed FeaturePython)
  n = 6
  ref = C_element
FEATURE [App::DocumentObjectGroupPython] H_element064  label="H_element : 11"  # scripted group (container) (typed FeaturePython)
  n = 11
  ref = H_element
FEATURE [App::DocumentObjectGroupPython] N_element032  label="N_element : 014"  # scripted group (container) (typed FeaturePython)
  n = 1
  ref = N_element
FEATURE [App::DocumentObjectGroupPython] O_element072  label="O_element : 036"  # scripted group (container) (typed FeaturePython)
  n = 1
  ref = O_element
FEATURE [App::DocumentObjectGroupPython] G4_NYLON_6_6  label="G4_NYLON-6-6"  # scripted group (container) (typed FeaturePython)
  Dunit = g/cm3
  Dvalue = 1.14
  Group = -> [C_element070,H_element064,N_element032,O_element072]
  conduct = 2
  density = 1
  expand = 3
  formula = G4_NYLON-6-6
  name = G4_NYLON-6-6
  specific = 4
FEATURE [App::DocumentObjectGroupPython] H_element065  label="H_element : 0.139"  # scripted group (container) (typed FeaturePython)
  n = 0.107062
FEATURE [App::DocumentObjectGroupPython] C_element071  label="C_element : 0.680"  # scripted group (container) (typed FeaturePython)
  n = 0.680449
FEATURE [App::DocumentObjectGroupPython] N_element033  label="N_element : 0.099"  # scripted group (container) (typed FeaturePython)
  n = 0.099189
FEATURE [App::DocumentObjectGroupPython] O_element073  label="O_element : 0.113"  # scripted group (container) (typed FeaturePython)
  n = 0.1133
FEATURE [App::DocumentObjectGroupPython] G4_NYLON_6_10  label="G4_NYLON-6-10"  # scripted group (container) (typed FeaturePython)
  Dunit = g/cm3
  Dvalue = 1.14
  Group = -> [H_element065,C_element071,N_element033,O_element073]
  conduct = 2
  density = 1
  expand = 3
  formula = G4_NYLON-6-10
  name = G4_NYLON-6-10
  specific = 4
FEATURE [App::DocumentObjectGroupPython] H_element066  label="H_element : 0.140"  # scripted group (container) (typed FeaturePython)
  n = 0.115476
FEATURE [App::DocumentObjectGroupPython] C_element072  label="C_element : 0.721"  # scripted group (container) (typed FeaturePython)
  n = 0.720818
FEATURE [App::DocumentObjectGroupPython] N_element034  label="N_element : 0.076"  # scripted group (container) (typed FeaturePython)
  n = 0.0764169
FEATURE [App::DocumentObjectGroupPython] O_element074  label="O_element : 0.087"  # scripted group (container) (typed FeaturePython)
  n = 0.0872889
FEATURE [App::DocumentObjectGroupPython] G4_NYLON_11_RILSAN  label="G4_NYLON-11_RILSAN"  # scripted group (container) (typed FeaturePython)
  Dunit = g/cm3
  Dvalue = 1.425
  Group = -> [H_element066,C_element072,N_element034,O_element074]
  conduct = 2
  density = 1
  expand = 3
  formula = G4_NYLON-11_RILSAN
  name = G4_NYLON-11_RILSAN
  specific = 4
FEATURE [App::DocumentObjectGroupPython] C_element073  label="C_element : 8"  # scripted group (container) (typed FeaturePython)
  n = 8
  ref = C_element
FEATURE [App::DocumentObjectGroupPython] H_element067  label="H_element : 18"  # scripted group (container) (typed FeaturePython)
  n = 18
  ref = H_element
FEATURE [App::DocumentObjectGroupPython] G4_OCTANE  # scripted group (container) (typed FeaturePython)
  Dunit = g/cm3
  Dvalue = 0.7026
  Group = -> [C_element073,H_element067]
  conduct = 2
  density = 1
  expand = 3
  formula = G4_OCTANE
  name = G4_OCTANE
  specific = 4
FEATURE [App::DocumentObjectGroupPython] C_element074  label="C_element : 25"  # scripted group (container) (typed FeaturePython)
  n = 25
  ref = C_element
FEATURE [App::DocumentObjectGroupPython] H_element068  label="H_element : 52"  # scripted group (container) (typed FeaturePython)
  n = 52
  ref = H_element
FEATURE [App::DocumentObjectGroupPython] G4_PARAFFIN  # scripted group (container) (typed FeaturePython)
  Dunit = g/cm3
  Dvalue = 0.93
  Group = -> [C_element074,H_element068]
  conduct = 2
  density = 1
  expand = 3
  formula = G4_PARAFFIN
  name = G4_PARAFFIN
  specific = 4
FEATURE [App::DocumentObjectGroupPython] C_element075  label="C_element : 036"  # scripted group (container) (typed FeaturePython)
  n = 5
  ref = C_element
FEATURE [App::DocumentObjectGroupPython] H_element069  label="H_element : 032"  # scripted group (container) (typed FeaturePython)
  n = 12
  ref = H_element
FEATURE [App::DocumentObjectGroupPython] G4_N_PENTANE  label="G4_N-PENTANE"  # scripted group (container) (typed FeaturePython)
  Dunit = g/cm3
  Dvalue = 0.6262
  Group = -> [C_element075,H_element069]
  conduct = 2
  density = 1
  expand = 3
  formula = G4_N-PENTANE
  name = G4_N-PENTANE
  specific = 4
FEATURE [App::DocumentObjectGroupPython] H_element070  label="H_element : 0.014"  # scripted group (container) (typed FeaturePython)
  n = 0.0141
FEATURE [App::DocumentObjectGroupPython] C_element076  label="C_element : 0.072"  # scripted group (container) (typed FeaturePython)
  n = 0.072261
FEATURE [App::DocumentObjectGroupPython] N_element035  label="N_element : 0.019"  # scripted group (container) (typed FeaturePython)
  n = 0.01932
FEATURE [App::DocumentObjectGroupPython] O_element075  label="O_element : 0.066"  # scripted group (container) (typed FeaturePython)
  n = 0.066101
FEATURE [App::DocumentObjectGroupPython] S_element019  label="S_element : 0.020"  # scripted group (container) (typed FeaturePython)
  n = 0.00189
FEATURE [App::DocumentObjectGroupPython] Br_element004  label="Br_element : 0.349"  # scripted group (container) (typed FeaturePython)
  n = 0.349103
FEATURE [App::DocumentObjectGroupPython] Ag_element001  label="Ag_element : 0.474"  # scripted group (container) (typed FeaturePython)
  n = 0.474105
FEATURE [App::DocumentObjectGroupPython] I_element005  label="I_element : 0.003"  # scripted group (container) (typed FeaturePython)
  n = 0.00312
FEATURE [App::DocumentObjectGroupPython] G4_PHOTO_EMULSION  # scripted group (container) (typed FeaturePython)
  Dunit = g/cm3
  Dvalue = 3.815
  Group = -> [H_element070,C_element076,N_element035,O_element075,S_element019,Br_element004,Ag_element001,I_element005]
  conduct = 2
  density = 1
  expand = 3
  formula = G4_PHOTO_EMULSION
  name = G4_PHOTO_EMULSION
  specific = 4
FEATURE [App::DocumentObjectGroupPython] C_element077  label="C_element : 9"  # scripted group (container) (typed FeaturePython)
  n = 9
  ref = C_element
FEATURE [App::DocumentObjectGroupPython] H_element071  label="H_element : 033"  # scripted group (container) (typed FeaturePython)
  n = 10
  ref = H_element
FEATURE [App::DocumentObjectGroupPython] G4_PLASTIC_SC_VINYLTOLUENE  # scripted group (container) (typed FeaturePython)
  Dunit = g/cm3
  Dvalue = 1.032
  Group = -> [C_element077,H_element071]
  conduct = 2
  density = 1
  expand = 3
  formula = G4_PLASTIC_SC_VINYLTOLUENE
  name = G4_PLASTIC_SC_VINYLTOLUENE
  specific = 4
FEATURE [App::DocumentObjectGroupPython] Pu_element001  label="Pu_element : 1"  # scripted group (container) (typed FeaturePython)
  n = 1
  ref = Pu_element
FEATURE [App::DocumentObjectGroupPython] O_element076  label="O_element : 037"  # scripted group (container) (typed FeaturePython)
  n = 2
  ref = O_element
FEATURE [App::DocumentObjectGroupPython] G4_PLUTONIUM_DIOXIDE  # scripted group (container) (typed FeaturePython)
  Dunit = g/cm3
  Dvalue = 11.46
  Group = -> [Pu_element001,O_element076]
  conduct = 2
  density = 1
  expand = 3
  formula = G4_PLUTONIUM_DIOXIDE
  name = G4_PLUTONIUM_DIOXIDE
  specific = 4
FEATURE [App::DocumentObjectGroupPython] C_element078  label="C_element : 037"  # scripted group (container) (typed FeaturePython)
  n = 3
  ref = C_element
FEATURE [App::DocumentObjectGroupPython] H_element072  label="H_element : 034"  # scripted group (container) (typed FeaturePython)
  n = 3
  ref = H_element
FEATURE [App::DocumentObjectGroupPython] N_element036  label="N_element : 015"  # scripted group (container) (typed FeaturePython)
  n = 1
  ref = N_element
FEATURE [App::DocumentObjectGroupPython] G4_POLYACRYLONITRILE  # scripted group (container) (typed FeaturePython)
  Dunit = g/cm3
  Dvalue = 1.17
  Group = -> [C_element078,H_element072,N_element036]
  conduct = 2
  density = 1
  expand = 3
  formula = G4_POLYACRYLONITRILE
  name = G4_POLYACRYLONITRILE
  specific = 4
FEATURE [App::DocumentObjectGroupPython] C_element079  label="C_element : 16"  # scripted group (container) (typed FeaturePython)
  n = 16
  ref = C_element
FEATURE [App::DocumentObjectGroupPython] H_element073  label="H_element : 035"  # scripted group (container) (typed FeaturePython)
  n = 14
  ref = H_element
FEATURE [App::DocumentObjectGroupPython] O_element077  label="O_element : 038"  # scripted group (container) (typed FeaturePython)
  n = 3
  ref = O_element
FEATURE [App::DocumentObjectGroupPython] G4_POLYCARBONATE  # scripted group (container) (typed FeaturePython)
  Dunit = g/cm3
  Dvalue = 1.2
  Group = -> [C_element079,H_element073,O_element077]
  conduct = 2
  density = 1
  expand = 3
  formula = G4_POLYCARBONATE
  name = G4_POLYCARBONATE
  specific = 4
FEATURE [App::DocumentObjectGroupPython] C_element080  label="C_element : 038"  # scripted group (container) (typed FeaturePython)
  n = 8
  ref = C_element
FEATURE [App::DocumentObjectGroupPython] H_element074  label="H_element : 036"  # scripted group (container) (typed FeaturePython)
  n = 7
  ref = H_element
FEATURE [App::DocumentObjectGroupPython] Cl_element017  label="Cl_element : 007"  # scripted group (container) (typed FeaturePython)
  n = 1
  ref = Cl_element
FEATURE [App::DocumentObjectGroupPython] G4_POLYCHLOROSTYRENE  # scripted group (container) (typed FeaturePython)
  Dunit = g/cm3
  Dvalue = 1.3
  Group = -> [C_element080,H_element074,Cl_element017]
  conduct = 2
  density = 1
  expand = 3
  formula = G4_POLYCHLOROSTYRENE
  name = G4_POLYCHLOROSTYRENE
  specific = 4
FEATURE [App::DocumentObjectGroupPython] C_element081  label="C_element : 039"  # scripted group (container) (typed FeaturePython)
  n = 1
  ref = C_element
FEATURE [App::DocumentObjectGroupPython] H_element075  label="H_element : 037"  # scripted group (container) (typed FeaturePython)
  n = 2
  ref = H_element
FEATURE [App::DocumentObjectGroupPython] G4_POLYETHYLENE  # scripted group (container) (typed FeaturePython)
  Dunit = g/cm3
  Dvalue = 0.94
  Group = -> [C_element081,H_element075]
  conduct = 2
  density = 1
  expand = 3
  formula = G4_POLYETHYLENE
  name = G4_POLYETHYLENE
  specific = 4
FEATURE [App::DocumentObjectGroupPython] C_element082  label="C_element : 040"  # scripted group (container) (typed FeaturePython)
  n = 10
  ref = C_element
FEATURE [App::DocumentObjectGroupPython] H_element076  label="H_element : 038"  # scripted group (container) (typed FeaturePython)
  n = 8
  ref = H_element
FEATURE [App::DocumentObjectGroupPython] O_element078  label="O_element : 039"  # scripted group (container) (typed FeaturePython)
  n = 4
  ref = O_element
FEATURE [App::DocumentObjectGroupPython] G4_MYLAR  # scripted group (container) (typed FeaturePython)
  Dunit = g/cm3
  Dvalue = 1.4
  Group = -> [C_element082,H_element076,O_element078]
  conduct = 2
  density = 1
  expand = 3
  formula = G4_MYLAR
  name = G4_MYLAR
  specific = 4
FEATURE [App::DocumentObjectGroupPython] C_element083  label="C_element : 041"  # scripted group (container) (typed FeaturePython)
  n = 5
  ref = C_element
FEATURE [App::DocumentObjectGroupPython] H_element077  label="H_element : 039"  # scripted group (container) (typed FeaturePython)
  n = 8
  ref = H_element
FEATURE [App::DocumentObjectGroupPython] O_element079  label="O_element : 040"  # scripted group (container) (typed FeaturePython)
  n = 2
  ref = O_element
FEATURE [App::DocumentObjectGroupPython] G4_PLEXIGLASS  # scripted group (container) (typed FeaturePython)
  Dunit = g/cm3
  Dvalue = 1.19
  Group = -> [C_element083,H_element077,O_element079]
  conduct = 2
  density = 1
  expand = 3
  formula = G4_PLEXIGLASS
  name = G4_PLEXIGLASS
  specific = 4
FEATURE [App::DocumentObjectGroupPython] C_element084  label="C_element : 042"  # scripted group (container) (typed FeaturePython)
  n = 1
  ref = C_element
FEATURE [App::DocumentObjectGroupPython] H_element078  label="H_element : 040"  # scripted group (container) (typed FeaturePython)
  n = 2
  ref = H_element
FEATURE [App::DocumentObjectGroupPython] O_element080  label="O_element : 041"  # scripted group (container) (typed FeaturePython)
  n = 1
  ref = O_element
FEATURE [App::DocumentObjectGroupPython] G4_POLYOXYMETHYLENE  # scripted group (container) (typed FeaturePython)
  Dunit = g/cm3
  Dvalue = 1.425
  Group = -> [C_element084,H_element078,O_element080]
  conduct = 2
  density = 1
  expand = 3
  formula = G4_POLYOXYMETHYLENE
  name = G4_POLYOXYMETHYLENE
  specific = 4
FEATURE [App::DocumentObjectGroupPython] C_element085  label="C_element : 043"  # scripted group (container) (typed FeaturePython)
  n = 2
  ref = C_element
FEATURE [App::DocumentObjectGroupPython] H_element079  label="H_element : 041"  # scripted group (container) (typed FeaturePython)
  n = 4
  ref = H_element
FEATURE [App::DocumentObjectGroupPython] G4_POLYPROPYLENE  # scripted group (container) (typed FeaturePython)
  Dunit = g/cm3
  Dvalue = 0.9
  Group = -> [C_element085,H_element079]
  conduct = 2
  density = 1
  expand = 3
  formula = G4_POLYPROPYLENE
  name = G4_POLYPROPYLENE
  specific = 4
FEATURE [App::DocumentObjectGroupPython] C_element086  label="C_element : 044"  # scripted group (container) (typed FeaturePython)
  n = 8
  ref = C_element
FEATURE [App::DocumentObjectGroupPython] H_element080  label="H_element : 042"  # scripted group (container) (typed FeaturePython)
  n = 8
  ref = H_element
FEATURE [App::DocumentObjectGroupPython] G4_POLYSTYRENE  # scripted group (container) (typed FeaturePython)
  Dunit = g/cm3
  Dvalue = 1.06
  Group = -> [C_element086,H_element080]
  conduct = 2
  density = 1
  expand = 3
  formula = G4_POLYSTYRENE
  name = G4_POLYSTYRENE
  specific = 4
FEATURE [App::DocumentObjectGroupPython] C_element087  label="C_element : 045"  # scripted group (container) (typed FeaturePython)
  n = 2
  ref = C_element
FEATURE [App::DocumentObjectGroupPython] F_element014  label="F_element : 4"  # scripted group (container) (typed FeaturePython)
  n = 4
  ref = F_element
FEATURE [App::DocumentObjectGroupPython] G4_TEFLON  # scripted group (container) (typed FeaturePython)
  Dunit = g/cm3
  Dvalue = 2.2
  Group = -> [C_element087,F_element014]
  conduct = 2
  density = 1
  expand = 3
  formula = G4_TEFLON
  name = G4_TEFLON
  specific = 4
FEATURE [App::DocumentObjectGroupPython] C_element088  label="C_element : 046"  # scripted group (container) (typed FeaturePython)
  n = 2
  ref = C_element
FEATURE [App::DocumentObjectGroupPython] F_element015  label="F_element : 006"  # scripted group (container) (typed FeaturePython)
  n = 3
  ref = F_element
FEATURE [App::DocumentObjectGroupPython] Cl_element018  label="Cl_element : 008"  # scripted group (container) (typed FeaturePython)
  n = 1
  ref = Cl_element
FEATURE [App::DocumentObjectGroupPython] G4_POLYTRIFLUOROCHLOROETHYLENE  # scripted group (container) (typed FeaturePython)
  Dunit = g/cm3
  Dvalue = 2.1
  Group = -> [C_element088,F_element015,Cl_element018]
  conduct = 2
  density = 1
  expand = 3
  formula = G4_POLYTRIFLUOROCHLOROETHYLENE
  name = G4_POLYTRIFLUOROCHLOROETHYLENE
  specific = 4
FEATURE [App::DocumentObjectGroupPython] C_element089  label="C_element : 047"  # scripted group (container) (typed FeaturePython)
  n = 4
  ref = C_element
FEATURE [App::DocumentObjectGroupPython] H_element081  label="H_element : 043"  # scripted group (container) (typed FeaturePython)
  n = 6
  ref = H_element
FEATURE [App::DocumentObjectGroupPython] O_element081  label="O_element : 042"  # scripted group (container) (typed FeaturePython)
  n = 2
  ref = O_element
FEATURE [App::DocumentObjectGroupPython] G4_POLYVINYL_ACETATE  # scripted group (container) (typed FeaturePython)
  Dunit = g/cm3
  Dvalue = 1.19
  Group = -> [C_element089,H_element081,O_element081]
  conduct = 2
  density = 1
  expand = 3
  formula = G4_POLYVINYL_ACETATE
  name = G4_POLYVINYL_ACETATE
  specific = 4
FEATURE [App::DocumentObjectGroupPython] C_element090  label="C_element : 048"  # scripted group (container) (typed FeaturePython)
  n = 2
  ref = C_element
FEATURE [App::DocumentObjectGroupPython] H_element082  label="H_element : 044"  # scripted group (container) (typed FeaturePython)
  n = 4
  ref = H_element
FEATURE [App::DocumentObjectGroupPython] O_element082  label="O_element : 043"  # scripted group (container) (typed FeaturePython)
  n = 1
  ref = O_element
FEATURE [App::DocumentObjectGroupPython] G4_POLYVINYL_ALCOHOL  # scripted group (container) (typed FeaturePython)
  Dunit = g/cm3
  Dvalue = 1.3
  Group = -> [C_element090,H_element082,O_element082]
  conduct = 2
  density = 1
  expand = 3
  formula = G4_POLYVINYL_ALCOHOL
  name = G4_POLYVINYL_ALCOHOL
  specific = 4
FEATURE [App::DocumentObjectGroupPython] C_element091  label="C_element : 049"  # scripted group (container) (typed FeaturePython)
  n = 8
  ref = C_element
FEATURE [App::DocumentObjectGroupPython] H_element083  label="H_element : 045"  # scripted group (container) (typed FeaturePython)
  n = 14
  ref = H_element
FEATURE [App::DocumentObjectGroupPython] O_element083  label="O_element : 044"  # scripted group (container) (typed FeaturePython)
  n = 2
  ref = O_element
FEATURE [App::DocumentObjectGroupPython] G4_POLYVINYL_BUTYRAL  # scripted group (container) (typed FeaturePython)
  Dunit = g/cm3
  Dvalue = 1.12
  Group = -> [C_element091,H_element083,O_element083]
  conduct = 2
  density = 1
  expand = 3
  formula = G4_POLYVINYL_BUTYRAL
  name = G4_POLYVINYL_BUTYRAL
  specific = 4
FEATURE [App::DocumentObjectGroupPython] C_element092  label="C_element : 050"  # scripted group (container) (typed FeaturePython)
  n = 2
  ref = C_element
FEATURE [App::DocumentObjectGroupPython] H_element084  label="H_element : 046"  # scripted group (container) (typed FeaturePython)
  n = 3
  ref = H_element
FEATURE [App::DocumentObjectGroupPython] Cl_element019  label="Cl_element : 009"  # scripted group (container) (typed FeaturePython)
  n = 1
  ref = Cl_element
FEATURE [App::DocumentObjectGroupPython] G4_POLYVINYL_CHLORIDE  # scripted group (container) (typed FeaturePython)
  Dunit = g/cm3
  Dvalue = 1.3
  Group = -> [C_element092,H_element084,Cl_element019]
  conduct = 2
  density = 1
  expand = 3
  formula = G4_POLYVINYL_CHLORIDE
  name = G4_POLYVINYL_CHLORIDE
  specific = 4
FEATURE [App::DocumentObjectGroupPython] C_element093  label="C_element : 051"  # scripted group (container) (typed FeaturePython)
  n = 2
  ref = C_element
FEATURE [App::DocumentObjectGroupPython] H_element085  label="H_element : 047"  # scripted group (container) (typed FeaturePython)
  n = 2
  ref = H_element
FEATURE [App::DocumentObjectGroupPython] Cl_element020  label="Cl_element : 010"  # scripted group (container) (typed FeaturePython)
  n = 2
  ref = Cl_element
FEATURE [App::DocumentObjectGroupPython] G4_POLYVINYLIDENE_CHLORIDE  # scripted group (container) (typed FeaturePython)
  Dunit = g/cm3
  Dvalue = 1.7
  Group = -> [C_element093,H_element085,Cl_element020]
  conduct = 2
  density = 1
  expand = 3
  formula = G4_POLYVINYLIDENE_CHLORIDE
  name = G4_POLYVINYLIDENE_CHLORIDE
  specific = 4
FEATURE [App::DocumentObjectGroupPython] C_element094  label="C_element : 052"  # scripted group (container) (typed FeaturePython)
  n = 2
  ref = C_element
FEATURE [App::DocumentObjectGroupPython] H_element086  label="H_element : 048"  # scripted group (container) (typed FeaturePython)
  n = 2
  ref = H_element
FEATURE [App::DocumentObjectGroupPython] F_element016  label="F_element : 007"  # scripted group (container) (typed FeaturePython)
  n = 2
  ref = F_element
FEATURE [App::DocumentObjectGroupPython] G4_POLYVINYLIDENE_FLUORIDE  # scripted group (container) (typed FeaturePython)
  Dunit = g/cm3
  Dvalue = 1.76
  Group = -> [C_element094,H_element086,F_element016]
  conduct = 2
  density = 1
  expand = 3
  formula = G4_POLYVINYLIDENE_FLUORIDE
  name = G4_POLYVINYLIDENE_FLUORIDE
  specific = 4
FEATURE [App::DocumentObjectGroupPython] C_element095  label="C_element : 053"  # scripted group (container) (typed FeaturePython)
  n = 6
  ref = C_element
FEATURE [App::DocumentObjectGroupPython] H_element087  label="H_element : 9"  # scripted group (container) (typed FeaturePython)
  n = 9
  ref = H_element
FEATURE [App::DocumentObjectGroupPython] N_element037  label="N_element : 016"  # scripted group (container) (typed FeaturePython)
  n = 1
  ref = N_element
FEATURE [App::DocumentObjectGroupPython] O_element084  label="O_element : 045"  # scripted group (container) (typed FeaturePython)
  n = 1
  ref = O_element
FEATURE [App::DocumentObjectGroupPython] G4_POLYVINYL_PYRROLIDONE  # scripted group (container) (typed FeaturePython)
  Dunit = g/cm3
  Dvalue = 1.25
  Group = -> [C_element095,H_element087,N_element037,O_element084]
  conduct = 2
  density = 1
  expand = 3
  formula = G4_POLYVINYL_PYRROLIDONE
  name = G4_POLYVINYL_PYRROLIDONE
  specific = 4
FEATURE [App::DocumentObjectGroupPython] K_element008  label="K_element : 1"  # scripted group (container) (typed FeaturePython)
  n = 1
  ref = K_element
FEATURE [App::DocumentObjectGroupPython] I_element006  label="I_element : 003"  # scripted group (container) (typed FeaturePython)
  n = 1
  ref = I_element
FEATURE [App::DocumentObjectGroupPython] G4_POTASSIUM_IODIDE  # scripted group (container) (typed FeaturePython)
  Dunit = g/cm3
  Dvalue = 3.13
  Group = -> [K_element008,I_element006]
  conduct = 2
  density = 1
  expand = 3
  formula = G4_POTASSIUM_IODIDE
  name = G4_POTASSIUM_IODIDE
  specific = 4
FEATURE [App::DocumentObjectGroupPython] K_element009  label="K_element : 2"  # scripted group (container) (typed FeaturePython)
  n = 2
  ref = K_element
FEATURE [App::DocumentObjectGroupPython] O_element085  label="O_element : 046"  # scripted group (container) (typed FeaturePython)
  n = 1
  ref = O_element
FEATURE [App::DocumentObjectGroupPython] G4_POTASSIUM_OXIDE  # scripted group (container) (typed FeaturePython)
  Dunit = g/cm3
  Dvalue = 2.32
  Group = -> [K_element009,O_element085]
  conduct = 2
  density = 1
  expand = 3
  formula = G4_POTASSIUM_OXIDE
  name = G4_POTASSIUM_OXIDE
  specific = 4
FEATURE [App::DocumentObjectGroupPython] C_element096  label="C_element : 054"  # scripted group (container) (typed FeaturePython)
  n = 3
  ref = C_element
FEATURE [App::DocumentObjectGroupPython] H_element088  label="H_element : 049"  # scripted group (container) (typed FeaturePython)
  n = 8
  ref = H_element
FEATURE [App::DocumentObjectGroupPython] G4_PROPANE  # scripted group (container) (typed FeaturePython)
  Dunit = g/cm3
  Dvalue = 0.00187939
  Group = -> [C_element096,H_element088]
  conduct = 2
  density = 1
  expand = 3
  formula = G4_PROPANE
  name = G4_PROPANE
  specific = 4
FEATURE [App::DocumentObjectGroupPython] C_element097  label="C_element : 055"  # scripted group (container) (typed FeaturePython)
  n = 3
  ref = C_element
FEATURE [App::DocumentObjectGroupPython] H_element089  label="H_element : 050"  # scripted group (container) (typed FeaturePython)
  n = 8
  ref = H_element
FEATURE [App::DocumentObjectGroupPython] G4_lPROPANE  # scripted group (container) (typed FeaturePython)
  Dunit = g/cm3
  Dvalue = 0.43
  Group = -> [C_element097,H_element089]
  conduct = 2
  density = 1
  expand = 3
  formula = G4_lPROPANE
  name = G4_lPROPANE
  specific = 4
FEATURE [App::DocumentObjectGroupPython] C_element098  label="C_element : 056"  # scripted group (container) (typed FeaturePython)
  n = 3
  ref = C_element
FEATURE [App::DocumentObjectGroupPython] H_element090  label="H_element : 051"  # scripted group (container) (typed FeaturePython)
  n = 8
  ref = H_element
FEATURE [App::DocumentObjectGroupPython] O_element086  label="O_element : 047"  # scripted group (container) (typed FeaturePython)
  n = 1
  ref = O_element
FEATURE [App::DocumentObjectGroupPython] G4_N_PROPYL_ALCOHOL  label="G4_N-PROPYL_ALCOHOL"  # scripted group (container) (typed FeaturePython)
  Dunit = g/cm3
  Dvalue = 0.8035
  Group = -> [C_element098,H_element090,O_element086]
  conduct = 2
  density = 1
  expand = 3
  formula = G4_N-PROPYL_ALCOHOL
  name = G4_N-PROPYL_ALCOHOL
  specific = 4
FEATURE [App::DocumentObjectGroupPython] C_element099  label="C_element : 057"  # scripted group (container) (typed FeaturePython)
  n = 5
  ref = C_element
FEATURE [App::DocumentObjectGroupPython] H_element091  label="H_element : 052"  # scripted group (container) (typed FeaturePython)
  n = 5
  ref = H_element
FEATURE [App::DocumentObjectGroupPython] N_element038  label="N_element : 017"  # scripted group (container) (typed FeaturePython)
  n = 1
  ref = N_element
FEATURE [App::DocumentObjectGroupPython] G4_PYRIDINE  # scripted group (container) (typed FeaturePython)
  Dunit = g/cm3
  Dvalue = 0.9819
  Group = -> [C_element099,H_element091,N_element038]
  conduct = 2
  density = 1
  expand = 3
  formula = G4_PYRIDINE
  name = G4_PYRIDINE
  specific = 4
FEATURE [App::DocumentObjectGroupPython] H_element092  label="H_element : 0.144"  # scripted group (container) (typed FeaturePython)
  n = 0.143711
FEATURE [App::DocumentObjectGroupPython] C_element100  label="C_element : 0.856"  # scripted group (container) (typed FeaturePython)
  n = 0.856289
FEATURE [App::DocumentObjectGroupPython] G4_RUBBER_BUTYL  # scripted group (container) (typed FeaturePython)
  Dunit = g/cm3
  Dvalue = 0.92
  Group = -> [H_element092,C_element100]
  conduct = 2
  density = 1
  expand = 3
  formula = G4_RUBBER_BUTYL
  name = G4_RUBBER_BUTYL
  specific = 4
FEATURE [App::DocumentObjectGroupPython] H_element093  label="H_element : 0.118"  # scripted group (container) (typed FeaturePython)
  n = 0.118371
FEATURE [App::DocumentObjectGroupPython] C_element101  label="C_element : 0.882"  # scripted group (container) (typed FeaturePython)
  n = 0.881629
FEATURE [App::DocumentObjectGroupPython] G4_RUBBER_NATURAL  # scripted group (container) (typed FeaturePython)
  Dunit = g/cm3
  Dvalue = 0.92
  Group = -> [H_element093,C_element101]
  conduct = 2
  density = 1
  expand = 3
  formula = G4_RUBBER_NATURAL
  name = G4_RUBBER_NATURAL
  specific = 4
FEATURE [App::DocumentObjectGroupPython] H_element094  label="H_element : 0.145"  # scripted group (container) (typed FeaturePython)
  n = 0.05692
FEATURE [App::DocumentObjectGroupPython] C_element102  label="C_element : 0.543"  # scripted group (container) (typed FeaturePython)
  n = 0.542646
FEATURE [App::DocumentObjectGroupPython] Cl_element021  label="Cl_element : 0.400"  # scripted group (container) (typed FeaturePython)
  n = 0.400434
FEATURE [App::DocumentObjectGroupPython] G4_RUBBER_NEOPRENE  # scripted group (container) (typed FeaturePython)
  Dunit = g/cm3
  Dvalue = 1.23
  Group = -> [H_element094,C_element102,Cl_element021]
  conduct = 2
  density = 1
  expand = 3
  formula = G4_RUBBER_NEOPRENE
  name = G4_RUBBER_NEOPRENE
  specific = 4
FEATURE [App::DocumentObjectGroupPython] Si_element006  label="Si_element : 1"  # scripted group (container) (typed FeaturePython)
  n = 1
  ref = Si_element
FEATURE [App::DocumentObjectGroupPython] O_element087  label="O_element : 048"  # scripted group (container) (typed FeaturePython)
  n = 2
  ref = O_element
FEATURE [App::DocumentObjectGroupPython] G4_SILICON_DIOXIDE  # scripted group (container) (typed FeaturePython)
  Dunit = g/cm3
  Dvalue = 2.32
  Group = -> [Si_element006,O_element087]
  conduct = 2
  density = 1
  expand = 3
  formula = G4_SILICON_DIOXIDE
  name = G4_SILICON_DIOXIDE
  specific = 4
FEATURE [App::DocumentObjectGroupPython] Ag_element002  label="Ag_element : 1"  # scripted group (container) (typed FeaturePython)
  n = 1
  ref = Ag_element
FEATURE [App::DocumentObjectGroupPython] Br_element005  label="Br_element : 003"  # scripted group (container) (typed FeaturePython)
  n = 1
  ref = Br_element
FEATURE [App::DocumentObjectGroupPython] G4_SILVER_BROMIDE  # scripted group (container) (typed FeaturePython)
  Dunit = g/cm3
  Dvalue = 6.473
  Group = -> [Ag_element002,Br_element005]
  conduct = 2
  density = 1
  expand = 3
  formula = G4_SILVER_BROMIDE
  name = G4_SILVER_BROMIDE
  specific = 4
FEATURE [App::DocumentObjectGroupPython] Ag_element003  label="Ag_element : 002"  # scripted group (container) (typed FeaturePython)
  n = 1
  ref = Ag_element
FEATURE [App::DocumentObjectGroupPython] Cl_element022  label="Cl_element : 011"  # scripted group (container) (typed FeaturePython)
  n = 1
  ref = Cl_element
FEATURE [App::DocumentObjectGroupPython] G4_SILVER_CHLORIDE  # scripted group (container) (typed FeaturePython)
  Dunit = g/cm3
  Dvalue = 5.56
  Group = -> [Ag_element003,Cl_element022]
  conduct = 2
  density = 1
  expand = 3
  formula = G4_SILVER_CHLORIDE
  name = G4_SILVER_CHLORIDE
  specific = 4
FEATURE [App::DocumentObjectGroupPython] Br_element006  label="Br_element : 0.423"  # scripted group (container) (typed FeaturePython)
  n = 0.422895
FEATURE [App::DocumentObjectGroupPython] Ag_element004  label="Ag_element : 0.574"  # scripted group (container) (typed FeaturePython)
  n = 0.573748
FEATURE [App::DocumentObjectGroupPython] I_element007  label="I_element : 0.649"  # scripted group (container) (typed FeaturePython)
  n = 0.003357
FEATURE [App::DocumentObjectGroupPython] G4_SILVER_HALIDES  # scripted group (container) (typed FeaturePython)
  Dunit = g/cm3
  Dvalue = 6.47
  Group = -> [Br_element006,Ag_element004,I_element007]
  conduct = 2
  density = 1
  expand = 3
  formula = G4_SILVER_HALIDES
  name = G4_SILVER_HALIDES
  specific = 4
FEATURE [App::DocumentObjectGroupPython] Ag_element005  label="Ag_element : 003"  # scripted group (container) (typed FeaturePython)
  n = 1
  ref = Ag_element
FEATURE [App::DocumentObjectGroupPython] I_element008  label="I_element : 004"  # scripted group (container) (typed FeaturePython)
  n = 1
  ref = I_element
FEATURE [App::DocumentObjectGroupPython] G4_SILVER_IODIDE  # scripted group (container) (typed FeaturePython)
  Dunit = g/cm3
  Dvalue = 6.01
  Group = -> [Ag_element005,I_element008]
  conduct = 2
  density = 1
  expand = 3
  formula = G4_SILVER_IODIDE
  name = G4_SILVER_IODIDE
  specific = 4
FEATURE [App::DocumentObjectGroupPython] H_element095  label="H_element : 0.100"  # scripted group (container) (typed FeaturePython)
  n = 0.1
FEATURE [App::DocumentObjectGroupPython] C_element103  label="C_element : 0.204"  # scripted group (container) (typed FeaturePython)
  n = 0.204
FEATURE [App::DocumentObjectGroupPython] N_element039  label="N_element : 0.759"  # scripted group (container) (typed FeaturePython)
  n = 0.042
FEATURE [App::DocumentObjectGroupPython] O_element088  label="O_element : 0.645"  # scripted group (container) (typed FeaturePython)
  n = 0.645
FEATURE [App::DocumentObjectGroupPython] Na_element013  label="Na_element : 0.100"  # scripted group (container) (typed FeaturePython)
  n = 0.002
FEATURE [App::DocumentObjectGroupPython] P_element009  label="P_element : 0.107"  # scripted group (container) (typed FeaturePython)
  n = 0.001
FEATURE [App::DocumentObjectGroupPython] S_element020  label="S_element : 0.021"  # scripted group (container) (typed FeaturePython)
  n = 0.002
FEATURE [App::DocumentObjectGroupPython] Cl_element023  label="Cl_element : 0.590"  # scripted group (container) (typed FeaturePython)
  n = 0.003
FEATURE [App::DocumentObjectGroupPython] K_element010  label="K_element : 0.001"  # scripted group (container) (typed FeaturePython)
  n = 0.001
FEATURE [App::DocumentObjectGroupPython] G4_SKIN_ICRP  # scripted group (container) (typed FeaturePython)
  Dunit = g/cm3
  Dvalue = 1.09
  Group = -> [H_element095,C_element103,N_element039,O_element088,Na_element013,P_element009,S_element020,Cl_element023,K_element010]
  conduct = 2
  density = 1
  expand = 3
  formula = G4_SKIN_ICRP
  name = G4_SKIN_ICRP
  specific = 4
FEATURE [App::DocumentObjectGroupPython] Na_element014  label="Na_element : 2"  # scripted group (container) (typed FeaturePython)
  n = 2
  ref = Na_element
FEATURE [App::DocumentObjectGroupPython] C_element104  label="C_element : 058"  # scripted group (container) (typed FeaturePython)
  n = 1
  ref = C_element
FEATURE [App::DocumentObjectGroupPython] O_element089  label="O_element : 049"  # scripted group (container) (typed FeaturePython)
  n = 3
  ref = O_element
FEATURE [App::DocumentObjectGroupPython] G4_SODIUM_CARBONATE  # scripted group (container) (typed FeaturePython)
  Dunit = g/cm3
  Dvalue = 2.532
  Group = -> [Na_element014,C_element104,O_element089]
  conduct = 2
  density = 1
  expand = 3
  formula = G4_SODIUM_CARBONATE
  name = G4_SODIUM_CARBONATE
  specific = 4
FEATURE [App::DocumentObjectGroupPython] Na_element015  label="Na_element : 1"  # scripted group (container) (typed FeaturePython)
  n = 1
  ref = Na_element
FEATURE [App::DocumentObjectGroupPython] I_element009  label="I_element : 005"  # scripted group (container) (typed FeaturePython)
  n = 1
  ref = I_element
FEATURE [App::DocumentObjectGroupPython] G4_SODIUM_IODIDE  # scripted group (container) (typed FeaturePython)
  Dunit = g/cm3
  Dvalue = 3.667
  Group = -> [Na_element015,I_element009]
  conduct = 2
  density = 1
  expand = 3
  formula = G4_SODIUM_IODIDE
  name = G4_SODIUM_IODIDE
  specific = 4
FEATURE [App::DocumentObjectGroupPython] Na_element016  label="Na_element : 003"  # scripted group (container) (typed FeaturePython)
  n = 2
  ref = Na_element
FEATURE [App::DocumentObjectGroupPython] O_element090  label="O_element : 050"  # scripted group (container) (typed FeaturePython)
  n = 1
  ref = O_element
FEATURE [App::DocumentObjectGroupPython] G4_SODIUM_MONOXIDE  # scripted group (container) (typed FeaturePython)
  Dunit = g/cm3
  Dvalue = 2.27
  Group = -> [Na_element016,O_element090]
  conduct = 2
  density = 1
  expand = 3
  formula = G4_SODIUM_MONOXIDE
  name = G4_SODIUM_MONOXIDE
  specific = 4
FEATURE [App::DocumentObjectGroupPython] Na_element017  label="Na_element : 004"  # scripted group (container) (typed FeaturePython)
  n = 1
  ref = Na_element
FEATURE [App::DocumentObjectGroupPython] N_element040  label="N_element : 018"  # scripted group (container) (typed FeaturePython)
  n = 1
  ref = N_element
FEATURE [App::DocumentObjectGroupPython] O_element091  label="O_element : 051"  # scripted group (container) (typed FeaturePython)
  n = 3
  ref = O_element
FEATURE [App::DocumentObjectGroupPython] G4_SODIUM_NITRATE  # scripted group (container) (typed FeaturePython)
  Dunit = g/cm3
  Dvalue = 2.261
  Group = -> [Na_element017,N_element040,O_element091]
  conduct = 2
  density = 1
  expand = 3
  formula = G4_SODIUM_NITRATE
  name = G4_SODIUM_NITRATE
  specific = 4
FEATURE [App::DocumentObjectGroupPython] C_element105  label="C_element : 059"  # scripted group (container) (typed FeaturePython)
  n = 14
  ref = C_element
FEATURE [App::DocumentObjectGroupPython] H_element096  label="H_element : 053"  # scripted group (container) (typed FeaturePython)
  n = 12
  ref = H_element
FEATURE [App::DocumentObjectGroupPython] G4_STILBENE  # scripted group (container) (typed FeaturePython)
  Dunit = g/cm3
  Dvalue = 0.9707
  Group = -> [C_element105,H_element096]
  conduct = 2
  density = 1
  expand = 3
  formula = G4_STILBENE
  name = G4_STILBENE
  specific = 4
FEATURE [App::DocumentObjectGroupPython] C_element106  label="C_element : 12"  # scripted group (container) (typed FeaturePython)
  n = 12
  ref = C_element
FEATURE [App::DocumentObjectGroupPython] H_element097  label="H_element : 22"  # scripted group (container) (typed FeaturePython)
  n = 22
  ref = H_element
FEATURE [App::DocumentObjectGroupPython] O_element092  label="O_element : 11"  # scripted group (container) (typed FeaturePython)
  n = 11
  ref = O_element
FEATURE [App::DocumentObjectGroupPython] G4_SUCROSE  # scripted group (container) (typed FeaturePython)
  Dunit = g/cm3
  Dvalue = 1.5805
  Group = -> [C_element106,H_element097,O_element092]
  conduct = 2
  density = 1
  expand = 3
  formula = G4_SUCROSE
  name = G4_SUCROSE
  specific = 4
FEATURE [App::DocumentObjectGroupPython] C_element107  label="C_element : 18"  # scripted group (container) (typed FeaturePython)
  n = 18
  ref = C_element
FEATURE [App::DocumentObjectGroupPython] H_element098  label="H_element : 054"  # scripted group (container) (typed FeaturePython)
  n = 14
  ref = H_element
FEATURE [App::DocumentObjectGroupPython] G4_TERPHENYL  # scripted group (container) (typed FeaturePython)
  Dunit = g/cm3
  Dvalue = 1.24
  Group = -> [C_element107,H_element098]
  conduct = 2
  density = 1
  expand = 3
  formula = G4_TERPHENYL
  name = G4_TERPHENYL
  specific = 4
FEATURE [App::DocumentObjectGroupPython] H_element099  label="H_element : 0.146"  # scripted group (container) (typed FeaturePython)
  n = 0.106
FEATURE [App::DocumentObjectGroupPython] C_element108  label="C_element : 0.883"  # scripted group (container) (typed FeaturePython)
  n = 0.099
FEATURE [App::DocumentObjectGroupPython] N_element041  label="N_element : 0.020"  # scripted group (container) (typed FeaturePython)
  n = 0.02
FEATURE [App::DocumentObjectGroupPython] O_element093  label="O_element : 0.766"  # scripted group (container) (typed FeaturePython)
  n = 0.766
FEATURE [App::DocumentObjectGroupPython] Na_element018  label="Na_element : 0.101"  # scripted group (container) (typed FeaturePython)
  n = 0.002
FEATURE [App::DocumentObjectGroupPython] P_element010  label="P_element : 0.108"  # scripted group (container) (typed FeaturePython)
  n = 0.001
FEATURE [App::DocumentObjectGroupPython] S_element021  label="S_element : 0.022"  # scripted group (container) (typed FeaturePython)
  n = 0.002
FEATURE [App::DocumentObjectGroupPython] Cl_element024  label="Cl_element : 0.002"  # scripted group (container) (typed FeaturePython)
  n = 0.002
FEATURE [App::DocumentObjectGroupPython] K_element011  label="K_element : 0.017"  # scripted group (container) (typed FeaturePython)
  n = 0.002
FEATURE [App::DocumentObjectGroupPython] G4_TESTIS_ICRP  # scripted group (container) (typed FeaturePython)
  Dunit = g/cm3
  Dvalue = 1.04
  Group = -> [H_element099,C_element108,N_element041,O_element093,Na_element018,P_element010,S_element021,Cl_element024,K_element011]
  conduct = 2
  density = 1
  expand = 3
  formula = G4_TESTIS_ICRP
  name = G4_TESTIS_ICRP
  specific = 4
FEATURE [App::DocumentObjectGroupPython] C_element109  label="C_element : 060"  # scripted group (container) (typed FeaturePython)
  n = 2
  ref = C_element
FEATURE [App::DocumentObjectGroupPython] Cl_element025  label="Cl_element : 012"  # scripted group (container) (typed FeaturePython)
  n = 4
  ref = Cl_element
FEATURE [App::DocumentObjectGroupPython] G4_TETRACHLOROETHYLENE  # scripted group (container) (typed FeaturePython)
  Dunit = g/cm3
  Dvalue = 1.625
  Group = -> [C_element109,Cl_element025]
  conduct = 2
  density = 1
  expand = 3
  formula = G4_TETRACHLOROETHYLENE
  name = G4_TETRACHLOROETHYLENE
  specific = 4
FEATURE [App::DocumentObjectGroupPython] Tl_element001  label="Tl_element : 1"  # scripted group (container) (typed FeaturePython)
  n = 1
  ref = Tl_element
FEATURE [App::DocumentObjectGroupPython] Cl_element026  label="Cl_element : 013"  # scripted group (container) (typed FeaturePython)
  n = 1
  ref = Cl_element
FEATURE [App::DocumentObjectGroupPython] G4_THALLIUM_CHLORIDE  # scripted group (container) (typed FeaturePython)
  Dunit = g/cm3
  Dvalue = 7.004
  Group = -> [Tl_element001,Cl_element026]
  conduct = 2
  density = 1
  expand = 3
  formula = G4_THALLIUM_CHLORIDE
  name = G4_THALLIUM_CHLORIDE
  specific = 4
FEATURE [App::DocumentObjectGroupPython] H_element100  label="H_element : 0.147"  # scripted group (container) (typed FeaturePython)
  n = 0.105
FEATURE [App::DocumentObjectGroupPython] C_element110  label="C_element : 0.256"  # scripted group (container) (typed FeaturePython)
  n = 0.256
FEATURE [App::DocumentObjectGroupPython] N_element042  label="N_element : 0.760"  # scripted group (container) (typed FeaturePython)
  n = 0.027
FEATURE [App::DocumentObjectGroupPython] O_element094  label="O_element : 0.602"  # scripted group (container) (typed FeaturePython)
  n = 0.602
FEATURE [App::DocumentObjectGroupPython] Na_element019  label="Na_element : 0.102"  # scripted group (container) (typed FeaturePython)
  n = 0.001
FEATURE [App::DocumentObjectGroupPython] P_element011  label="P_element : 0.109"  # scripted group (container) (typed FeaturePython)
  n = 0.002
FEATURE [App::DocumentObjectGroupPython] S_element022  label="S_element : 0.023"  # scripted group (container) (typed FeaturePython)
  n = 0.003
FEATURE [App::DocumentObjectGroupPython] Cl_element027  label="Cl_element : 0.591"  # scripted group (container) (typed FeaturePython)
  n = 0.002
FEATURE [App::DocumentObjectGroupPython] K_element012  label="K_element : 0.018"  # scripted group (container) (typed FeaturePython)
  n = 0.002
FEATURE [App::DocumentObjectGroupPython] G4_TISSUE_SOFT_ICRP  # scripted group (container) (typed FeaturePython)
  Dunit = g/cm3
  Dvalue = 1.03
  Group = -> [H_element100,C_element110,N_element042,O_element094,Na_element019,P_element011,S_element022,Cl_element027,K_element012]
  conduct = 2
  density = 1
  expand = 3
  formula = G4_TISSUE_SOFT_ICRP
  name = G4_TISSUE_SOFT_ICRP
  specific = 4
FEATURE [App::DocumentObjectGroupPython] H_element101  label="H_element : 0.148"  # scripted group (container) (typed FeaturePython)
  n = 0.101
FEATURE [App::DocumentObjectGroupPython] C_element111  label="C_element : 0.111"  # scripted group (container) (typed FeaturePython)
  n = 0.111
FEATURE [App::DocumentObjectGroupPython] N_element043  label="N_element : 0.026"  # scripted group (container) (typed FeaturePython)
  n = 0.026
FEATURE [App::DocumentObjectGroupPython] O_element095  label="O_element : 0.762"  # scripted group (container) (typed FeaturePython)
  n = 0.762
FEATURE [App::DocumentObjectGroupPython] G4_TISSUE_SOFT_ICRU_4  label="G4_TISSUE_SOFT_ICRU-4"  # scripted group (container) (typed FeaturePython)
  Dunit = g/cm3
  Dvalue = 1
  Group = -> [H_element101,C_element111,N_element043,O_element095]
  conduct = 2
  density = 1
  expand = 3
  formula = G4_TISSUE_SOFT_ICRU-4
  name = G4_TISSUE_SOFT_ICRU-4
  specific = 4
FEATURE [App::DocumentObjectGroupPython] H_element102  label="H_element : 0.149"  # scripted group (container) (typed FeaturePython)
  n = 0.101869
FEATURE [App::DocumentObjectGroupPython] C_element112  label="C_element : 0.456"  # scripted group (container) (typed FeaturePython)
  n = 0.456179
FEATURE [App::DocumentObjectGroupPython] N_element044  label="N_element : 0.761"  # scripted group (container) (typed FeaturePython)
  n = 0.035172
FEATURE [App::DocumentObjectGroupPython] O_element096  label="O_element : 0.407"  # scripted group (container) (typed FeaturePython)
  n = 0.40678
FEATURE [App::DocumentObjectGroupPython] G4_TISSUE_METHANE  label="G4_TISSUE-METHANE"  # scripted group (container) (typed FeaturePython)
  Dunit = g/cm3
  Dvalue = 0.00106409
  Group = -> [H_element102,C_element112,N_element044,O_element096]
  conduct = 2
  density = 1
  expand = 3
  formula = G4_TISSUE-METHANE
  name = G4_TISSUE-METHANE
  specific = 4
FEATURE [App::DocumentObjectGroupPython] H_element103  label="H_element : 0.103"  # scripted group (container) (typed FeaturePython)
  n = 0.102672
FEATURE [App::DocumentObjectGroupPython] C_element113  label="C_element : 0.569"  # scripted group (container) (typed FeaturePython)
  n = 0.56894
FEATURE [App::DocumentObjectGroupPython] N_element045  label="N_element : 0.762"  # scripted group (container) (typed FeaturePython)
  n = 0.035022
FEATURE [App::DocumentObjectGroupPython] O_element097  label="O_element : 0.293"  # scripted group (container) (typed FeaturePython)
  n = 0.293366
FEATURE [App::DocumentObjectGroupPython] G4_TISSUE_PROPANE  label="G4_TISSUE-PROPANE"  # scripted group (container) (typed FeaturePython)
  Dunit = g/cm3
  Dvalue = 0.00182628
  Group = -> [H_element103,C_element113,N_element045,O_element097]
  conduct = 2
  density = 1
  expand = 3
  formula = G4_TISSUE-PROPANE
  name = G4_TISSUE-PROPANE
  specific = 4
FEATURE [App::DocumentObjectGroupPython] Ti_element003  label="Ti_element : 1"  # scripted group (container) (typed FeaturePython)
  n = 1
  ref = Ti_element
FEATURE [App::DocumentObjectGroupPython] O_element098  label="O_element : 052"  # scripted group (container) (typed FeaturePython)
  n = 2
  ref = O_element
FEATURE [App::DocumentObjectGroupPython] G4_TITANIUM_DIOXIDE  # scripted group (container) (typed FeaturePython)
  Dunit = g/cm3
  Dvalue = 4.26
  Group = -> [Ti_element003,O_element098]
  conduct = 2
  density = 1
  expand = 3
  formula = G4_TITANIUM_DIOXIDE
  name = G4_TITANIUM_DIOXIDE
  specific = 4
FEATURE [App::DocumentObjectGroupPython] C_element114  label="C_element : 061"  # scripted group (container) (typed FeaturePython)
  n = 7
  ref = C_element
FEATURE [App::DocumentObjectGroupPython] H_element104  label="H_element : 055"  # scripted group (container) (typed FeaturePython)
  n = 8
  ref = H_element
FEATURE [App::DocumentObjectGroupPython] G4_TOLUENE  # scripted group (container) (typed FeaturePython)
  Dunit = g/cm3
  Dvalue = 0.8669
  Group = -> [C_element114,H_element104]
  conduct = 2
  density = 1
  expand = 3
  formula = G4_TOLUENE
  name = G4_TOLUENE
  specific = 4
FEATURE [App::DocumentObjectGroupPython] C_element115  label="C_element : 062"  # scripted group (container) (typed FeaturePython)
  n = 2
  ref = C_element
FEATURE [App::DocumentObjectGroupPython] H_element105  label="H_element : 056"  # scripted group (container) (typed FeaturePython)
  n = 1
  ref = H_element
FEATURE [App::DocumentObjectGroupPython] Cl_element028  label="Cl_element : 014"  # scripted group (container) (typed FeaturePython)
  n = 3
  ref = Cl_element
FEATURE [App::DocumentObjectGroupPython] G4_TRICHLOROETHYLENE  # scripted group (container) (typed FeaturePython)
  Dunit = g/cm3
  Dvalue = 1.46
  Group = -> [C_element115,H_element105,Cl_element028]
  conduct = 2
  density = 1
  expand = 3
  formula = G4_TRICHLOROETHYLENE
  name = G4_TRICHLOROETHYLENE
  specific = 4
FEATURE [App::DocumentObjectGroupPython] C_element116  label="C_element : 063"  # scripted group (container) (typed FeaturePython)
  n = 6
  ref = C_element
FEATURE [App::DocumentObjectGroupPython] H_element106  label="H_element : 15"  # scripted group (container) (typed FeaturePython)
  n = 15
  ref = H_element
FEATURE [App::DocumentObjectGroupPython] O_element099  label="O_element : 053"  # scripted group (container) (typed FeaturePython)
  n = 4
  ref = O_element
FEATURE [App::DocumentObjectGroupPython] P_element012  label="P_element : 1"  # scripted group (container) (typed FeaturePython)
  n = 1
  ref = P_element
FEATURE [App::DocumentObjectGroupPython] G4_TRIETHYL_PHOSPHATE  # scripted group (container) (typed FeaturePython)
  Dunit = g/cm3
  Dvalue = 1.07
  Group = -> [C_element116,H_element106,O_element099,P_element012]
  conduct = 2
  density = 1
  expand = 3
  formula = G4_TRIETHYL_PHOSPHATE
  name = G4_TRIETHYL_PHOSPHATE
  specific = 4
FEATURE [App::DocumentObjectGroupPython] W_element003  label="W_element : 003"  # scripted group (container) (typed FeaturePython)
  n = 1
  ref = W_element
FEATURE [App::DocumentObjectGroupPython] F_element017  label="F_element : 6"  # scripted group (container) (typed FeaturePython)
  n = 6
  ref = F_element
FEATURE [App::DocumentObjectGroupPython] G4_TUNGSTEN_HEXAFLUORIDE  # scripted group (container) (typed FeaturePython)
  Dunit = g/cm3
  Dvalue = 2.4
  Group = -> [W_element003,F_element017]
  conduct = 2
  density = 1
  expand = 3
  formula = G4_TUNGSTEN_HEXAFLUORIDE
  name = G4_TUNGSTEN_HEXAFLUORIDE
  specific = 4
FEATURE [App::DocumentObjectGroupPython] U_element001  label="U_element : 1"  # scripted group (container) (typed FeaturePython)
  n = 1
  ref = U_element
FEATURE [App::DocumentObjectGroupPython] C_element117  label="C_element : 064"  # scripted group (container) (typed FeaturePython)
  n = 2
  ref = C_element
FEATURE [App::DocumentObjectGroupPython] G4_URANIUM_DICARBIDE  # scripted group (container) (typed FeaturePython)
  Dunit = g/cm3
  Dvalue = 11.28
  Group = -> [U_element001,C_element117]
  conduct = 2
  density = 1
  expand = 3
  formula = G4_URANIUM_DICARBIDE
  name = G4_URANIUM_DICARBIDE
  specific = 4
FEATURE [App::DocumentObjectGroupPython] U_element002  label="U_element : 002"  # scripted group (container) (typed FeaturePython)
  n = 1
  ref = U_element
FEATURE [App::DocumentObjectGroupPython] C_element118  label="C_element : 065"  # scripted group (container) (typed FeaturePython)
  n = 1
  ref = C_element
FEATURE [App::DocumentObjectGroupPython] G4_URANIUM_MONOCARBIDE  # scripted group (container) (typed FeaturePython)
  Dunit = g/cm3
  Dvalue = 13.63
  Group = -> [U_element002,C_element118]
  conduct = 2
  density = 1
  expand = 3
  formula = G4_URANIUM_MONOCARBIDE
  name = G4_URANIUM_MONOCARBIDE
  specific = 4
FEATURE [App::DocumentObjectGroupPython] U_element003  label="U_element : 003"  # scripted group (container) (typed FeaturePython)
  n = 1
  ref = U_element
FEATURE [App::DocumentObjectGroupPython] O_element100  label="O_element : 054"  # scripted group (container) (typed FeaturePython)
  n = 2
  ref = O_element
FEATURE [App::DocumentObjectGroupPython] G4_URANIUM_OXIDE  # scripted group (container) (typed FeaturePython)
  Dunit = g/cm3
  Dvalue = 10.96
  Group = -> [U_element003,O_element100]
  conduct = 2
  density = 1
  expand = 3
  formula = G4_URANIUM_OXIDE
  name = G4_URANIUM_OXIDE
  specific = 4
FEATURE [App::DocumentObjectGroupPython] C_element119  label="C_element : 066"  # scripted group (container) (typed FeaturePython)
  n = 1
  ref = C_element
FEATURE [App::DocumentObjectGroupPython] H_element107  label="H_element : 057"  # scripted group (container) (typed FeaturePython)
  n = 4
  ref = H_element
FEATURE [App::DocumentObjectGroupPython] N_element046  label="N_element : 019"  # scripted group (container) (typed FeaturePython)
  n = 2
  ref = N_element
FEATURE [App::DocumentObjectGroupPython] O_element101  label="O_element : 055"  # scripted group (container) (typed FeaturePython)
  n = 1
  ref = O_element
FEATURE [App::DocumentObjectGroupPython] G4_UREA  # scripted group (container) (typed FeaturePython)
  Dunit = g/cm3
  Dvalue = 1.323
  Group = -> [C_element119,H_element107,N_element046,O_element101]
  conduct = 2
  density = 1
  expand = 3
  formula = G4_UREA
  name = G4_UREA
  specific = 4
FEATURE [App::DocumentObjectGroupPython] C_element120  label="C_element : 067"  # scripted group (container) (typed FeaturePython)
  n = 5
  ref = C_element
FEATURE [App::DocumentObjectGroupPython] H_element108  label="H_element : 058"  # scripted group (container) (typed FeaturePython)
  n = 11
  ref = H_element
FEATURE [App::DocumentObjectGroupPython] N_element047  label="N_element : 020"  # scripted group (container) (typed FeaturePython)
  n = 1
  ref = N_element
FEATURE [App::DocumentObjectGroupPython] O_element102  label="O_element : 056"  # scripted group (container) (typed FeaturePython)
  n = 2
  ref = O_element
FEATURE [App::DocumentObjectGroupPython] G4_VALINE  # scripted group (container) (typed FeaturePython)
  Dunit = g/cm3
  Dvalue = 1.23
  Group = -> [C_element120,H_element108,N_element047,O_element102]
  conduct = 2
  density = 1
  expand = 3
  formula = G4_VALINE
  name = G4_VALINE
  specific = 4
FEATURE [App::DocumentObjectGroupPython] H_element109  label="H_element : 0.009"  # scripted group (container) (typed FeaturePython)
  n = 0.009417
FEATURE [App::DocumentObjectGroupPython] C_element121  label="C_element : 0.281"  # scripted group (container) (typed FeaturePython)
  n = 0.280555
FEATURE [App::DocumentObjectGroupPython] F_element018  label="F_element : 0.710"  # scripted group (container) (typed FeaturePython)
  n = 0.710028
FEATURE [App::DocumentObjectGroupPython] G4_VITON  # scripted group (container) (typed FeaturePython)
  Dunit = g/cm3
  Dvalue = 1.8
  Group = -> [H_element109,C_element121,F_element018]
  conduct = 2
  density = 1
  expand = 3
  formula = G4_VITON
  name = G4_VITON
  specific = 4
FEATURE [App::DocumentObjectGroupPython] H_element110  label="H_element : 059"  # scripted group (container) (typed FeaturePython)
  n = 2
  ref = H_element
FEATURE [App::DocumentObjectGroupPython] O_element103  label="O_element : 057"  # scripted group (container) (typed FeaturePython)
  n = 1
  ref = O_element
FEATURE [App::DocumentObjectGroupPython] G4_WATER  # scripted group (container) (typed FeaturePython)
  Dunit = g/cm3
  Dvalue = 1
  Group = -> [H_element110,O_element103]
  conduct = 2
  density = 1
  expand = 3
  formula = G4_WATER
  name = G4_WATER
  specific = 4
FEATURE [App::DocumentObjectGroupPython] H_element111  label="H_element : 060"  # scripted group (container) (typed FeaturePython)
  n = 2
  ref = H_element
FEATURE [App::DocumentObjectGroupPython] O_element104  label="O_element : 058"  # scripted group (container) (typed FeaturePython)
  n = 1
  ref = O_element
FEATURE [App::DocumentObjectGroupPython] G4_WATER_VAPOR  # scripted group (container) (typed FeaturePython)
  Dunit = g/cm3
  Dvalue = 0.000756182
  Group = -> [H_element111,O_element104]
  conduct = 2
  density = 1
  expand = 3
  formula = G4_WATER_VAPOR
  name = G4_WATER_VAPOR
  specific = 4
FEATURE [App::DocumentObjectGroupPython] C_element122  label="C_element : 068"  # scripted group (container) (typed FeaturePython)
  n = 8
  ref = C_element
FEATURE [App::DocumentObjectGroupPython] H_element112  label="H_element : 061"  # scripted group (container) (typed FeaturePython)
  n = 10
  ref = H_element
FEATURE [App::DocumentObjectGroupPython] G4_XYLENE  # scripted group (container) (typed FeaturePython)
  Dunit = g/cm3
  Dvalue = 0.87
  Group = -> [C_element122,H_element112]
  conduct = 2
  density = 1
  expand = 3
  formula = G4_XYLENE
  name = G4_XYLENE
  specific = 4
FEATURE [App::DocumentObjectGroupPython] C_element123  label="C_element : 069"  # scripted group (container) (typed FeaturePython)
  n = 1
  ref = C_element
FEATURE [App::DocumentObjectGroupPython] G4_GRAPHITE  # scripted group (container) (typed FeaturePython)
  Dunit = g/cm3
  Dvalue = 2.21
  Group = -> [C_element123]
  conduct = 2
  density = 1
  expand = 3
  formula = G4_GRAPHITE
  name = G4_GRAPHITE
  specific = 4
FEATURE [App::DocumentObjectGroupPython] NIST  # scripted group (container) (typed FeaturePython)
  Group = -> [G4_A_150_TISSUE,G4_ACETONE,G4_ACETYLENE,G4_ADENINE,G4_ADIPOSE_TISSUE_ICRP,G4_AIR,G4_ALANINE,G4_ALUMINUM_OXIDE,G4_AMBER,G4_AMMONIA,G4_ANILINE,G4_ANTHRACENE,G4_B_100_BONE,G4_BAKELITE,G4_BARIUM_FLUORIDE,G4_BARIUM_SULFATE,G4_BENZENE,G4_BERYLLIUM_OXIDE,G4_BGO,G4_BLOOD_ICRP,G4_BONE_COMPACT_ICRU,G4_BONE_CORTICAL_ICRP,G4_BORON_CARBIDE,G4_BORON_OXIDE,G4_BRAIN_ICRP,G4_BUTANE,G4_N_BUTYL_ALCOHOL,G4_C_552,+152 more]
FEATURE [App::DocumentObjectGroupPython] H_element113  label="H_element : 062"  # scripted group (container) (typed FeaturePython)
  n = 1
  ref = H_element
FEATURE [App::DocumentObjectGroupPython] G4_H  # scripted group (container) (typed FeaturePython)
  Dunit = g/cm3
  Dvalue = 8.3748e-05
  Group = -> [H_element113]
  conduct = 2
  density = 1
  expand = 3
  formula = H
  name = G4_H
  specific = 4
FEATURE [App::DocumentObjectGroupPython] He_element001  label="He_element : 1"  # scripted group (container) (typed FeaturePython)
  n = 1
  ref = He_element
FEATURE [App::DocumentObjectGroupPython] G4_He  # scripted group (container) (typed FeaturePython)
  Dunit = g/cm3
  Dvalue = 0.000166322
  Group = -> [He_element001]
  conduct = 2
  density = 1
  expand = 3
  formula = He
  name = G4_He
  specific = 4
FEATURE [App::DocumentObjectGroupPython] Li_element008  label="Li_element : 008"  # scripted group (container) (typed FeaturePython)
  n = 1
  ref = Li_element
FEATURE [App::DocumentObjectGroupPython] G4_Li  # scripted group (container) (typed FeaturePython)
  Dunit = g/cm3
  Dvalue = 0.534
  Group = -> [Li_element008]
  conduct = 2
  density = 1
  expand = 3
  formula = Li
  name = G4_Li
  specific = 4
FEATURE [App::DocumentObjectGroupPython] Be_element002  label="Be_element : 002"  # scripted group (container) (typed FeaturePython)
  n = 1
  ref = Be_element
FEATURE [App::DocumentObjectGroupPython] G4_Be  # scripted group (container) (typed FeaturePython)
  Dunit = g/cm3
  Dvalue = 1.848
  Group = -> [Be_element002]
  conduct = 2
  density = 1
  expand = 3
  formula = Be
  name = G4_Be
  specific = 4
FEATURE [App::DocumentObjectGroupPython] B_element007  label="B_element : 007"  # scripted group (container) (typed FeaturePython)
  n = 1
  ref = B_element
FEATURE [App::DocumentObjectGroupPython] G4_B  # scripted group (container) (typed FeaturePython)
  Dunit = g/cm3
  Dvalue = 2.37
  Group = -> [B_element007]
  conduct = 2
  density = 1
  expand = 3
  formula = B
  name = G4_B
  specific = 4
FEATURE [App::DocumentObjectGroupPython] C_element124  label="C_element : 070"  # scripted group (container) (typed FeaturePython)
  n = 1
  ref = C_element
FEATURE [App::DocumentObjectGroupPython] G4_C  # scripted group (container) (typed FeaturePython)
  Dunit = g/cm3
  Dvalue = 2
  Group = -> [C_element124]
  conduct = 2
  density = 1
  expand = 3
  formula = C
  name = G4_C
  specific = 4
FEATURE [App::DocumentObjectGroupPython] N_element048  label="N_element : 021"  # scripted group (container) (typed FeaturePython)
  n = 1
  ref = N_element
FEATURE [App::DocumentObjectGroupPython] G4_N  # scripted group (container) (typed FeaturePython)
  Dunit = g/cm3
  Dvalue = 0.0011652
  Group = -> [N_element048]
  conduct = 2
  density = 1
  expand = 3
  formula = N
  name = G4_N
  specific = 4
FEATURE [App::DocumentObjectGroupPython] O_element105  label="O_element : 059"  # scripted group (container) (typed FeaturePython)
  n = 1
  ref = O_element
FEATURE [App::DocumentObjectGroupPython] G4_O  # scripted group (container) (typed FeaturePython)
  Dunit = g/cm3
  Dvalue = 0.00133151
  Group = -> [O_element105]
  conduct = 2
  density = 1
  expand = 3
  formula = O
  name = G4_O
  specific = 4
FEATURE [App::DocumentObjectGroupPython] F_element019  label="F_element : 008"  # scripted group (container) (typed FeaturePython)
  n = 1
  ref = F_element
FEATURE [App::DocumentObjectGroupPython] G4_F  # scripted group (container) (typed FeaturePython)
  Dunit = g/cm3
  Dvalue = 0.00158029
  Group = -> [F_element019]
  conduct = 2
  density = 1
  expand = 3
  formula = F
  name = G4_F
  specific = 4
FEATURE [App::DocumentObjectGroupPython] Ne_element001  label="Ne_element : 1"  # scripted group (container) (typed FeaturePython)
  n = 1
  ref = Ne_element
FEATURE [App::DocumentObjectGroupPython] G4_Ne  # scripted group (container) (typed FeaturePython)
  Dunit = g/cm3
  Dvalue = 0.000838505
  Group = -> [Ne_element001]
  conduct = 2
  density = 1
  expand = 3
  formula = Ne
  name = G4_Ne
  specific = 4
FEATURE [App::DocumentObjectGroupPython] Na_element020  label="Na_element : 005"  # scripted group (container) (typed FeaturePython)
  n = 1
  ref = Na_element
FEATURE [App::DocumentObjectGroupPython] G4_Na  # scripted group (container) (typed FeaturePython)
  Dunit = g/cm3
  Dvalue = 0.971
  Group = -> [Na_element020]
  conduct = 2
  density = 1
  expand = 3
  formula = Na
  name = G4_Na
  specific = 4
FEATURE [App::DocumentObjectGroupPython] Mg_element011  label="Mg_element : 005"  # scripted group (container) (typed FeaturePython)
  n = 1
  ref = Mg_element
FEATURE [App::DocumentObjectGroupPython] G4_Mg  # scripted group (container) (typed FeaturePython)
  Dunit = g/cm3
  Dvalue = 1.74
  Group = -> [Mg_element011]
  conduct = 2
  density = 1
  expand = 3
  formula = Mg
  name = G4_Mg
  specific = 4
FEATURE [App::DocumentObjectGroupPython] Al_element004  label="Al_element : 1"  # scripted group (container) (typed FeaturePython)
  n = 1
  ref = Al_element
FEATURE [App::DocumentObjectGroupPython] G4_Al  # scripted group (container) (typed FeaturePython)
  Dunit = g/cm3
  Dvalue = 2.699
  Group = -> [Al_element004]
  conduct = 2
  density = 1
  expand = 3
  formula = Al
  name = G4_Al
  specific = 4
FEATURE [App::DocumentObjectGroupPython] Si_element007  label="Si_element : 002"  # scripted group (container) (typed FeaturePython)
  n = 1
  ref = Si_element
FEATURE [App::DocumentObjectGroupPython] G4_Si  # scripted group (container) (typed FeaturePython)
  Dunit = g/cm3
  Dvalue = 2.33
  Group = -> [Si_element007]
  conduct = 2
  density = 1
  expand = 3
  formula = Si
  name = G4_Si
  specific = 4
FEATURE [App::DocumentObjectGroupPython] P_element013  label="P_element : 002"  # scripted group (container) (typed FeaturePython)
  n = 1
  ref = P_element
FEATURE [App::DocumentObjectGroupPython] G4_P  # scripted group (container) (typed FeaturePython)
  Dunit = g/cm3
  Dvalue = 2.2
  Group = -> [P_element013]
  conduct = 2
  density = 1
  expand = 3
  formula = P
  name = G4_P
  specific = 4
FEATURE [App::DocumentObjectGroupPython] S_element023  label="S_element : 007"  # scripted group (container) (typed FeaturePython)
  n = 1
  ref = S_element
FEATURE [App::DocumentObjectGroupPython] G4_S  # scripted group (container) (typed FeaturePython)
  Dunit = g/cm3
  Dvalue = 2
  Group = -> [S_element023]
  conduct = 2
  density = 1
  expand = 3
  formula = S
  name = G4_S
  specific = 4
FEATURE [App::DocumentObjectGroupPython] Cl_element029  label="Cl_element : 015"  # scripted group (container) (typed FeaturePython)
  n = 1
  ref = Cl_element
FEATURE [App::DocumentObjectGroupPython] G4_Cl  # scripted group (container) (typed FeaturePython)
  Dunit = g/cm3
  Dvalue = 0.00299473
  Group = -> [Cl_element029]
  conduct = 2
  density = 1
  expand = 3
  formula = Cl
  name = G4_Cl
  specific = 4
FEATURE [App::DocumentObjectGroupPython] Ar_element002  label="Ar_element : 1"  # scripted group (container) (typed FeaturePython)
  n = 1
  ref = Ar_element
FEATURE [App::DocumentObjectGroupPython] G4_Ar  # scripted group (container) (typed FeaturePython)
  Dunit = g/cm3
  Dvalue = 0.00166201
  Group = -> [Ar_element002]
  conduct = 2
  density = 1
  expand = 3
  formula = Ar
  name = G4_Ar
  specific = 4
FEATURE [App::DocumentObjectGroupPython] K_element013  label="K_element : 003"  # scripted group (container) (typed FeaturePython)
  n = 1
  ref = K_element
FEATURE [App::DocumentObjectGroupPython] G4_K  # scripted group (container) (typed FeaturePython)
  Dunit = g/cm3
  Dvalue = 0.862
  Group = -> [K_element013]
  conduct = 2
  density = 1
  expand = 3
  formula = K
  name = G4_K
  specific = 4
FEATURE [App::DocumentObjectGroupPython] Ca_element014  label="Ca_element : 007"  # scripted group (container) (typed FeaturePython)
  n = 1
  ref = Ca_element
FEATURE [App::DocumentObjectGroupPython] G4_Ca  # scripted group (container) (typed FeaturePython)
  Dunit = g/cm3
  Dvalue = 1.55
  Group = -> [Ca_element014]
  conduct = 2
  density = 1
  expand = 3
  formula = Ca
  name = G4_Ca
  specific = 4
FEATURE [App::DocumentObjectGroupPython] Sc_element001  label="Sc_element : 1"  # scripted group (container) (typed FeaturePython)
  n = 1
  ref = Sc_element
FEATURE [App::DocumentObjectGroupPython] G4_Sc  # scripted group (container) (typed FeaturePython)
  Dunit = g/cm3
  Dvalue = 2.989
  Group = -> [Sc_element001]
  conduct = 2
  density = 1
  expand = 3
  formula = Sc
  name = G4_Sc
  specific = 4
FEATURE [App::DocumentObjectGroupPython] Ti_element004  label="Ti_element : 002"  # scripted group (container) (typed FeaturePython)
  n = 1
  ref = Ti_element
FEATURE [App::DocumentObjectGroupPython] G4_Ti  # scripted group (container) (typed FeaturePython)
  Dunit = g/cm3
  Dvalue = 4.54
  Group = -> [Ti_element004]
  conduct = 2
  density = 1
  expand = 3
  formula = Ti
  name = G4_Ti
  specific = 4
FEATURE [App::DocumentObjectGroupPython] V_element001  label="V_element : 1"  # scripted group (container) (typed FeaturePython)
  n = 1
  ref = V_element
FEATURE [App::DocumentObjectGroupPython] G4_V  # scripted group (container) (typed FeaturePython)
  Dunit = g/cm3
  Dvalue = 6.11
  Group = -> [V_element001]
  conduct = 2
  density = 1
  expand = 3
  formula = V
  name = G4_V
  specific = 4
FEATURE [App::DocumentObjectGroupPython] Cr_element001  label="Cr_element : 1"  # scripted group (container) (typed FeaturePython)
  n = 1
  ref = Cr_element
FEATURE [App::DocumentObjectGroupPython] G4_Cr  # scripted group (container) (typed FeaturePython)
  Dunit = g/cm3
  Dvalue = 7.18
  Group = -> [Cr_element001]
  conduct = 2
  density = 1
  expand = 3
  formula = Cr
  name = G4_Cr
  specific = 4
FEATURE [App::DocumentObjectGroupPython] Mn_element001  label="Mn_element : 1"  # scripted group (container) (typed FeaturePython)
  n = 1
  ref = Mn_element
FEATURE [App::DocumentObjectGroupPython] G4_Mn  # scripted group (container) (typed FeaturePython)
  Dunit = g/cm3
  Dvalue = 7.44
  Group = -> [Mn_element001]
  conduct = 2
  density = 1
  expand = 3
  formula = Mn
  name = G4_Mn
  specific = 4
FEATURE [App::DocumentObjectGroupPython] Fe_element007  label="Fe_element : 004"  # scripted group (container) (typed FeaturePython)
  n = 1
  ref = Fe_element
FEATURE [App::DocumentObjectGroupPython] G4_Fe  # scripted group (container) (typed FeaturePython)
  Dunit = g/cm3
  Dvalue = 7.874
  Group = -> [Fe_element007]
  conduct = 2
  density = 1
  expand = 3
  formula = Fe
  name = G4_Fe
  specific = 4
FEATURE [App::DocumentObjectGroupPython] Co_element001  label="Co_element : 1"  # scripted group (container) (typed FeaturePython)
  n = 1
  ref = Co_element
FEATURE [App::DocumentObjectGroupPython] G4_Co  # scripted group (container) (typed FeaturePython)
  Dunit = g/cm3
  Dvalue = 8.9
  Group = -> [Co_element001]
  conduct = 2
  density = 1
  expand = 3
  formula = Co
  name = G4_Co
  specific = 4
FEATURE [App::DocumentObjectGroupPython] Ni_element001  label="Ni_element : 1"  # scripted group (container) (typed FeaturePython)
  n = 1
  ref = Ni_element
FEATURE [App::DocumentObjectGroupPython] G4_Ni  # scripted group (container) (typed FeaturePython)
  Dunit = g/cm3
  Dvalue = 8.902
  Group = -> [Ni_element001]
  conduct = 2
  density = 1
  expand = 3
  formula = Ni
  name = G4_Ni
  specific = 4
FEATURE [App::DocumentObjectGroupPython] Cu_element001  label="Cu_element : 1"  # scripted group (container) (typed FeaturePython)
  n = 1
  ref = Cu_element
FEATURE [App::DocumentObjectGroupPython] G4_Cu  # scripted group (container) (typed FeaturePython)
  Dunit = g/cm3
  Dvalue = 8.96
  Group = -> [Cu_element001]
  conduct = 2
  density = 1
  expand = 3
  formula = Cu
  name = G4_Cu
  specific = 4
FEATURE [App::DocumentObjectGroupPython] Zn_element001  label="Zn_element : 1"  # scripted group (container) (typed FeaturePython)
  n = 1
  ref = Zn_element
FEATURE [App::DocumentObjectGroupPython] G4_Zn  # scripted group (container) (typed FeaturePython)
  Dunit = g/cm3
  Dvalue = 7.133
  Group = -> [Zn_element001]
  conduct = 2
  density = 1
  expand = 3
  formula = Zn
  name = G4_Zn
  specific = 4
FEATURE [App::DocumentObjectGroupPython] Ga_element002  label="Ga_element : 002"  # scripted group (container) (typed FeaturePython)
  n = 1
  ref = Ga_element
FEATURE [App::DocumentObjectGroupPython] G4_Ga  # scripted group (container) (typed FeaturePython)
  Dunit = g/cm3
  Dvalue = 5.904
  Group = -> [Ga_element002]
  conduct = 2
  density = 1
  expand = 3
  formula = Ga
  name = G4_Ga
  specific = 4
FEATURE [App::DocumentObjectGroupPython] Ge_element002  label="Ge_element : 1"  # scripted group (container) (typed FeaturePython)
  n = 1
  ref = Ge_element
FEATURE [App::DocumentObjectGroupPython] G4_Ge  # scripted group (container) (typed FeaturePython)
  Dunit = g/cm3
  Dvalue = 5.323
  Group = -> [Ge_element002]
  conduct = 2
  density = 1
  expand = 3
  formula = Ge
  name = G4_Ge
  specific = 4
FEATURE [App::DocumentObjectGroupPython] As_element003  label="As_element : 002"  # scripted group (container) (typed FeaturePython)
  n = 1
  ref = As_element
FEATURE [App::DocumentObjectGroupPython] G4_As  # scripted group (container) (typed FeaturePython)
  Dunit = g/cm3
  Dvalue = 5.73
  Group = -> [As_element003]
  conduct = 2
  density = 1
  expand = 3
  formula = As
  name = G4_As
  specific = 4
FEATURE [App::DocumentObjectGroupPython] Se_element001  label="Se_element : 1"  # scripted group (container) (typed FeaturePython)
  n = 1
  ref = Se_element
FEATURE [App::DocumentObjectGroupPython] G4_Se  # scripted group (container) (typed FeaturePython)
  Dunit = g/cm3
  Dvalue = 4.5
  Group = -> [Se_element001]
  conduct = 2
  density = 1
  expand = 3
  formula = Se
  name = G4_Se
  specific = 4
FEATURE [App::DocumentObjectGroupPython] Br_element007  label="Br_element : 004"  # scripted group (container) (typed FeaturePython)
  n = 1
  ref = Br_element
FEATURE [App::DocumentObjectGroupPython] G4_Br  # scripted group (container) (typed FeaturePython)
  Dunit = g/cm3
  Dvalue = 0.0070721
  Group = -> [Br_element007]
  conduct = 2
  density = 1
  expand = 3
  formula = Br
  name = G4_Br
  specific = 4
FEATURE [App::DocumentObjectGroupPython] Kr_element001  label="Kr_element : 1"  # scripted group (container) (typed FeaturePython)
  n = 1
  ref = Kr_element
FEATURE [App::DocumentObjectGroupPython] G4_Kr  # scripted group (container) (typed FeaturePython)
  Dunit = g/cm3
  Dvalue = 0.00347832
  Group = -> [Kr_element001]
  conduct = 2
  density = 1
  expand = 3
  formula = Kr
  name = G4_Kr
  specific = 4
FEATURE [App::DocumentObjectGroupPython] Rb_element001  label="Rb_element : 1"  # scripted group (container) (typed FeaturePython)
  n = 1
  ref = Rb_element
FEATURE [App::DocumentObjectGroupPython] G4_Rb  # scripted group (container) (typed FeaturePython)
  Dunit = g/cm3
  Dvalue = 1.532
  Group = -> [Rb_element001]
  conduct = 2
  density = 1
  expand = 3
  formula = Rb
  name = G4_Rb
  specific = 4
FEATURE [App::DocumentObjectGroupPython] Sr_element001  label="Sr_element : 1"  # scripted group (container) (typed FeaturePython)
  n = 1
  ref = Sr_element
FEATURE [App::DocumentObjectGroupPython] G4_Sr  # scripted group (container) (typed FeaturePython)
  Dunit = g/cm3
  Dvalue = 2.54
  Group = -> [Sr_element001]
  conduct = 2
  density = 1
  expand = 3
  formula = Sr
  name = G4_Sr
  specific = 4
FEATURE [App::DocumentObjectGroupPython] Y_element001  label="Y_element : 1"  # scripted group (container) (typed FeaturePython)
  n = 1
  ref = Y_element
FEATURE [App::DocumentObjectGroupPython] G4_Y  # scripted group (container) (typed FeaturePython)
  Dunit = g/cm3
  Dvalue = 4.469
  Group = -> [Y_element001]
  conduct = 2
  density = 1
  expand = 3
  formula = Y
  name = G4_Y
  specific = 4
FEATURE [App::DocumentObjectGroupPython] Zr_element001  label="Zr_element : 1"  # scripted group (container) (typed FeaturePython)
  n = 1
  ref = Zr_element
FEATURE [App::DocumentObjectGroupPython] G4_Zr  # scripted group (container) (typed FeaturePython)
  Dunit = g/cm3
  Dvalue = 6.506
  Group = -> [Zr_element001]
  conduct = 2
  density = 1
  expand = 3
  formula = Zr
  name = G4_Zr
  specific = 4
FEATURE [App::DocumentObjectGroupPython] Nb_element001  label="Nb_element : 1"  # scripted group (container) (typed FeaturePython)
  n = 1
  ref = Nb_element
FEATURE [App::DocumentObjectGroupPython] G4_Nb  # scripted group (container) (typed FeaturePython)
  Dunit = g/cm3
  Dvalue = 8.57
  Group = -> [Nb_element001]
  conduct = 2
  density = 1
  expand = 3
  formula = Nb
  name = G4_Nb
  specific = 4
FEATURE [App::DocumentObjectGroupPython] Mo_element001  label="Mo_element : 1"  # scripted group (container) (typed FeaturePython)
  n = 1
  ref = Mo_element
FEATURE [App::DocumentObjectGroupPython] G4_Mo  # scripted group (container) (typed FeaturePython)
  Dunit = g/cm3
  Dvalue = 10.22
  Group = -> [Mo_element001]
  conduct = 2
  density = 1
  expand = 3
  formula = Mo
  name = G4_Mo
  specific = 4
FEATURE [App::DocumentObjectGroupPython] Tc_element001  label="Tc_element : 1"  # scripted group (container) (typed FeaturePython)
  n = 1
  ref = Tc_element
FEATURE [App::DocumentObjectGroupPython] G4_Tc  # scripted group (container) (typed FeaturePython)
  Dunit = g/cm3
  Dvalue = 11.5
  Group = -> [Tc_element001]
  conduct = 2
  density = 1
  expand = 3
  formula = Tc
  name = G4_Tc
  specific = 4
FEATURE [App::DocumentObjectGroupPython] Ru_element001  label="Ru_element : 1"  # scripted group (container) (typed FeaturePython)
  n = 1
  ref = Ru_element
FEATURE [App::DocumentObjectGroupPython] G4_Ru  # scripted group (container) (typed FeaturePython)
  Dunit = g/cm3
  Dvalue = 12.41
  Group = -> [Ru_element001]
  conduct = 2
  density = 1
  expand = 3
  formula = Ru
  name = G4_Ru
  specific = 4
FEATURE [App::DocumentObjectGroupPython] Rh_element001  label="Rh_element : 1"  # scripted group (container) (typed FeaturePython)
  n = 1
  ref = Rh_element
FEATURE [App::DocumentObjectGroupPython] G4_Rh  # scripted group (container) (typed FeaturePython)
  Dunit = g/cm3
  Dvalue = 12.41
  Group = -> [Rh_element001]
  conduct = 2
  density = 1
  expand = 3
  formula = Rh
  name = G4_Rh
  specific = 4
FEATURE [App::DocumentObjectGroupPython] Pd_element001  label="Pd_element : 1"  # scripted group (container) (typed FeaturePython)
  n = 1
  ref = Pd_element
FEATURE [App::DocumentObjectGroupPython] G4_Pd  # scripted group (container) (typed FeaturePython)
  Dunit = g/cm3
  Dvalue = 12.02
  Group = -> [Pd_element001]
  conduct = 2
  density = 1
  expand = 3
  formula = Pd
  name = G4_Pd
  specific = 4
FEATURE [App::DocumentObjectGroupPython] Ag_element006  label="Ag_element : 004"  # scripted group (container) (typed FeaturePython)
  n = 1
  ref = Ag_element
FEATURE [App::DocumentObjectGroupPython] G4_Ag  # scripted group (container) (typed FeaturePython)
  Dunit = g/cm3
  Dvalue = 10.5
  Group = -> [Ag_element006]
  conduct = 2
  density = 1
  expand = 3
  formula = Ag
  name = G4_Ag
  specific = 4
FEATURE [App::DocumentObjectGroupPython] Cd_element003  label="Cd_element : 003"  # scripted group (container) (typed FeaturePython)
  n = 1
  ref = Cd_element
FEATURE [App::DocumentObjectGroupPython] G4_Cd  # scripted group (container) (typed FeaturePython)
  Dunit = g/cm3
  Dvalue = 8.65
  Group = -> [Cd_element003]
  conduct = 2
  density = 1
  expand = 3
  formula = Cd
  name = G4_Cd
  specific = 4
FEATURE [App::DocumentObjectGroupPython] In_element001  label="In_element : 1"  # scripted group (container) (typed FeaturePython)
  n = 1
  ref = In_element
FEATURE [App::DocumentObjectGroupPython] G4_In  # scripted group (container) (typed FeaturePython)
  Dunit = g/cm3
  Dvalue = 7.31
  Group = -> [In_element001]
  conduct = 2
  density = 1
  expand = 3
  formula = In
  name = G4_In
  specific = 4
FEATURE [App::DocumentObjectGroupPython] Sn_element001  label="Sn_element : 1"  # scripted group (container) (typed FeaturePython)
  n = 1
  ref = Sn_element
FEATURE [App::DocumentObjectGroupPython] G4_Sn  # scripted group (container) (typed FeaturePython)
  Dunit = g/cm3
  Dvalue = 7.31
  Group = -> [Sn_element001]
  conduct = 2
  density = 1
  expand = 3
  formula = Sn
  name = G4_Sn
  specific = 4
FEATURE [App::DocumentObjectGroupPython] Sb_element001  label="Sb_element : 1"  # scripted group (container) (typed FeaturePython)
  n = 1
  ref = Sb_element
FEATURE [App::DocumentObjectGroupPython] G4_Sb  # scripted group (container) (typed FeaturePython)
  Dunit = g/cm3
  Dvalue = 6.691
  Group = -> [Sb_element001]
  conduct = 2
  density = 1
  expand = 3
  formula = Sb
  name = G4_Sb
  specific = 4
FEATURE [App::DocumentObjectGroupPython] Te_element002  label="Te_element : 002"  # scripted group (container) (typed FeaturePython)
  n = 1
  ref = Te_element
FEATURE [App::DocumentObjectGroupPython] G4_Te  # scripted group (container) (typed FeaturePython)
  Dunit = g/cm3
  Dvalue = 6.24
  Group = -> [Te_element002]
  conduct = 2
  density = 1
  expand = 3
  formula = Te
  name = G4_Te
  specific = 4
FEATURE [App::DocumentObjectGroupPython] I_element010  label="I_element : 006"  # scripted group (container) (typed FeaturePython)
  n = 1
  ref = I_element
FEATURE [App::DocumentObjectGroupPython] G4_I  # scripted group (container) (typed FeaturePython)
  Dunit = g/cm3
  Dvalue = 4.93
  Group = -> [I_element010]
  conduct = 2
  density = 1
  expand = 3
  formula = I
  name = G4_I
  specific = 4
FEATURE [App::DocumentObjectGroupPython] Xe_element001  label="Xe_element : 1"  # scripted group (container) (typed FeaturePython)
  n = 1
  ref = Xe_element
FEATURE [App::DocumentObjectGroupPython] G4_Xe  # scripted group (container) (typed FeaturePython)
  Dunit = g/cm3
  Dvalue = 0.00548536
  Group = -> [Xe_element001]
  conduct = 2
  density = 1
  expand = 3
  formula = Xe
  name = G4_Xe
  specific = 4
FEATURE [App::DocumentObjectGroupPython] Cs_element003  label="Cs_element : 003"  # scripted group (container) (typed FeaturePython)
  n = 1
  ref = Cs_element
FEATURE [App::DocumentObjectGroupPython] G4_Cs  # scripted group (container) (typed FeaturePython)
  Dunit = g/cm3
  Dvalue = 1.873
  Group = -> [Cs_element003]
  conduct = 2
  density = 1
  expand = 3
  formula = Cs
  name = G4_Cs
  specific = 4
FEATURE [App::DocumentObjectGroupPython] Ba_element003  label="Ba_element : 003"  # scripted group (container) (typed FeaturePython)
  n = 1
  ref = Ba_element
FEATURE [App::DocumentObjectGroupPython] G4_Ba  # scripted group (container) (typed FeaturePython)
  Dunit = g/cm3
  Dvalue = 3.5
  Group = -> [Ba_element003]
  conduct = 2
  density = 1
  expand = 3
  formula = Ba
  name = G4_Ba
  specific = 4
FEATURE [App::DocumentObjectGroupPython] La_element003  label="La_element : 003"  # scripted group (container) (typed FeaturePython)
  n = 1
  ref = La_element
FEATURE [App::DocumentObjectGroupPython] G4_La  # scripted group (container) (typed FeaturePython)
  Dunit = g/cm3
  Dvalue = 6.154
  Group = -> [La_element003]
  conduct = 2
  density = 1
  expand = 3
  formula = La
  name = G4_La
  specific = 4
FEATURE [App::DocumentObjectGroupPython] Ce_element002  label="Ce_element : 1"  # scripted group (container) (typed FeaturePython)
  n = 1
  ref = Ce_element
FEATURE [App::DocumentObjectGroupPython] G4_Ce  # scripted group (container) (typed FeaturePython)
  Dunit = g/cm3
  Dvalue = 6.657
  Group = -> [Ce_element002]
  conduct = 2
  density = 1
  expand = 3
  formula = Ce
  name = G4_Ce
  specific = 4
FEATURE [App::DocumentObjectGroupPython] Pr_element001  label="Pr_element : 1"  # scripted group (container) (typed FeaturePython)
  n = 1
  ref = Pr_element
FEATURE [App::DocumentObjectGroupPython] G4_Pr  # scripted group (container) (typed FeaturePython)
  Dunit = g/cm3
  Dvalue = 6.71
  Group = -> [Pr_element001]
  conduct = 2
  density = 1
  expand = 3
  formula = Pr
  name = G4_Pr
  specific = 4
FEATURE [App::DocumentObjectGroupPython] Nd_element001  label="Nd_element : 1"  # scripted group (container) (typed FeaturePython)
  n = 1
  ref = Nd_element
FEATURE [App::DocumentObjectGroupPython] G4_Nd  # scripted group (container) (typed FeaturePython)
  Dunit = g/cm3
  Dvalue = 6.9
  Group = -> [Nd_element001]
  conduct = 2
  density = 1
  expand = 3
  formula = Nd
  name = G4_Nd
  specific = 4
FEATURE [App::DocumentObjectGroupPython] Pm_element001  label="Pm_element : 1"  # scripted group (container) (typed FeaturePython)
  n = 1
  ref = Pm_element
FEATURE [App::DocumentObjectGroupPython] G4_Pm  # scripted group (container) (typed FeaturePython)
  Dunit = g/cm3
  Dvalue = 7.22
  Group = -> [Pm_element001]
  conduct = 2
  density = 1
  expand = 3
  formula = Pm
  name = G4_Pm
  specific = 4
FEATURE [App::DocumentObjectGroupPython] Sm_element001  label="Sm_element : 1"  # scripted group (container) (typed FeaturePython)
  n = 1
  ref = Sm_element
FEATURE [App::DocumentObjectGroupPython] G4_Sm  # scripted group (container) (typed FeaturePython)
  Dunit = g/cm3
  Dvalue = 7.46
  Group = -> [Sm_element001]
  conduct = 2
  density = 1
  expand = 3
  formula = Sm
  name = G4_Sm
  specific = 4
FEATURE [App::DocumentObjectGroupPython] Eu_element001  label="Eu_element : 1"  # scripted group (container) (typed FeaturePython)
  n = 1
  ref = Eu_element
FEATURE [App::DocumentObjectGroupPython] G4_Eu  # scripted group (container) (typed FeaturePython)
  Dunit = g/cm3
  Dvalue = 5.243
  Group = -> [Eu_element001]
  conduct = 2
  density = 1
  expand = 3
  formula = Eu
  name = G4_Eu
  specific = 4
FEATURE [App::DocumentObjectGroupPython] Gd_element002  label="Gd_element : 1"  # scripted group (container) (typed FeaturePython)
  n = 1
  ref = Gd_element
FEATURE [App::DocumentObjectGroupPython] G4_Gd  # scripted group (container) (typed FeaturePython)
  Dunit = g/cm3
  Dvalue = 7.9004
  Group = -> [Gd_element002]
  conduct = 2
  density = 1
  expand = 3
  formula = Gd
  name = G4_Gd
  specific = 4
FEATURE [App::DocumentObjectGroupPython] Tb_element001  label="Tb_element : 1"  # scripted group (container) (typed FeaturePython)
  n = 1
  ref = Tb_element
FEATURE [App::DocumentObjectGroupPython] G4_Tb  # scripted group (container) (typed FeaturePython)
  Dunit = g/cm3
  Dvalue = 8.229
  Group = -> [Tb_element001]
  conduct = 2
  density = 1
  expand = 3
  formula = Tb
  name = G4_Tb
  specific = 4
FEATURE [App::DocumentObjectGroupPython] Dy_element001  label="Dy_element : 1"  # scripted group (container) (typed FeaturePython)
  n = 1
  ref = Dy_element
FEATURE [App::DocumentObjectGroupPython] G4_Dy  # scripted group (container) (typed FeaturePython)
  Dunit = g/cm3
  Dvalue = 8.55
  Group = -> [Dy_element001]
  conduct = 2
  density = 1
  expand = 3
  formula = Dy
  name = G4_Dy
  specific = 4
FEATURE [App::DocumentObjectGroupPython] Ho_element001  label="Ho_element : 1"  # scripted group (container) (typed FeaturePython)
  n = 1
  ref = Ho_element
FEATURE [App::DocumentObjectGroupPython] G4_Ho  # scripted group (container) (typed FeaturePython)
  Dunit = g/cm3
  Dvalue = 8.795
  Group = -> [Ho_element001]
  conduct = 2
  density = 1
  expand = 3
  formula = Ho
  name = G4_Ho
  specific = 4
FEATURE [App::DocumentObjectGroupPython] Er_element001  label="Er_element : 1"  # scripted group (container) (typed FeaturePython)
  n = 1
  ref = Er_element
FEATURE [App::DocumentObjectGroupPython] G4_Er  # scripted group (container) (typed FeaturePython)
  Dunit = g/cm3
  Dvalue = 9.066
  Group = -> [Er_element001]
  conduct = 2
  density = 1
  expand = 3
  formula = Er
  name = G4_Er
  specific = 4
FEATURE [App::DocumentObjectGroupPython] Tm_element001  label="Tm_element : 1"  # scripted group (container) (typed FeaturePython)
  n = 1
  ref = Tm_element
FEATURE [App::DocumentObjectGroupPython] G4_Tm  # scripted group (container) (typed FeaturePython)
  Dunit = g/cm3
  Dvalue = 9.321
  Group = -> [Tm_element001]
  conduct = 2
  density = 1
  expand = 3
  formula = Tm
  name = G4_Tm
  specific = 4
FEATURE [App::DocumentObjectGroupPython] Yb_element001  label="Yb_element : 1"  # scripted group (container) (typed FeaturePython)
  n = 1
  ref = Yb_element
FEATURE [App::DocumentObjectGroupPython] G4_Yb  # scripted group (container) (typed FeaturePython)
  Dunit = g/cm3
  Dvalue = 6.73
  Group = -> [Yb_element001]
  conduct = 2
  density = 1
  expand = 3
  formula = Yb
  name = G4_Yb
  specific = 4
FEATURE [App::DocumentObjectGroupPython] Lu_element001  label="Lu_element : 1"  # scripted group (container) (typed FeaturePython)
  n = 1
  ref = Lu_element
FEATURE [App::DocumentObjectGroupPython] G4_Lu  # scripted group (container) (typed FeaturePython)
  Dunit = g/cm3
  Dvalue = 9.84
  Group = -> [Lu_element001]
  conduct = 2
  density = 1
  expand = 3
  formula = Lu
  name = G4_Lu
  specific = 4
FEATURE [App::DocumentObjectGroupPython] Hf_element001  label="Hf_element : 1"  # scripted group (container) (typed FeaturePython)
  n = 1
  ref = Hf_element
FEATURE [App::DocumentObjectGroupPython] G4_Hf  # scripted group (container) (typed FeaturePython)
  Dunit = g/cm3
  Dvalue = 13.31
  Group = -> [Hf_element001]
  conduct = 2
  density = 1
  expand = 3
  formula = Hf
  name = G4_Hf
  specific = 4
FEATURE [App::DocumentObjectGroupPython] Ta_element001  label="Ta_element : 1"  # scripted group (container) (typed FeaturePython)
  n = 1
  ref = Ta_element
FEATURE [App::DocumentObjectGroupPython] G4_Ta  # scripted group (container) (typed FeaturePython)
  Dunit = g/cm3
  Dvalue = 16.654
  Group = -> [Ta_element001]
  conduct = 2
  density = 1
  expand = 3
  formula = Ta
  name = G4_Ta
  specific = 4
FEATURE [App::DocumentObjectGroupPython] W_element004  label="W_element : 004"  # scripted group (container) (typed FeaturePython)
  n = 1
  ref = W_element
FEATURE [App::DocumentObjectGroupPython] G4_W  # scripted group (container) (typed FeaturePython)
  Dunit = g/cm3
  Dvalue = 19.3
  Group = -> [W_element004]
  conduct = 2
  density = 1
  expand = 3
  formula = W
  name = G4_W
  specific = 4
FEATURE [App::DocumentObjectGroupPython] Re_element001  label="Re_element : 1"  # scripted group (container) (typed FeaturePython)
  n = 1
  ref = Re_element
FEATURE [App::DocumentObjectGroupPython] G4_Re  # scripted group (container) (typed FeaturePython)
  Dunit = g/cm3
  Dvalue = 21.02
  Group = -> [Re_element001]
  conduct = 2
  density = 1
  expand = 3
  formula = Re
  name = G4_Re
  specific = 4
FEATURE [App::DocumentObjectGroupPython] Os_element001  label="Os_element : 1"  # scripted group (container) (typed FeaturePython)
  n = 1
  ref = Os_element
FEATURE [App::DocumentObjectGroupPython] G4_Os  # scripted group (container) (typed FeaturePython)
  Dunit = g/cm3
  Dvalue = 22.57
  Group = -> [Os_element001]
  conduct = 2
  density = 1
  expand = 3
  formula = Os
  name = G4_Os
  specific = 4
FEATURE [App::DocumentObjectGroupPython] Ir_element001  label="Ir_element : 1"  # scripted group (container) (typed FeaturePython)
  n = 1
  ref = Ir_element
FEATURE [App::DocumentObjectGroupPython] G4_Ir  # scripted group (container) (typed FeaturePython)
  Dunit = g/cm3
  Dvalue = 22.42
  Group = -> [Ir_element001]
  conduct = 2
  density = 1
  expand = 3
  formula = Ir
  name = G4_Ir
  specific = 4
FEATURE [App::DocumentObjectGroupPython] Pt_element001  label="Pt_element : 1"  # scripted group (container) (typed FeaturePython)
  n = 1
  ref = Pt_element
FEATURE [App::DocumentObjectGroupPython] G4_Pt  # scripted group (container) (typed FeaturePython)
  Dunit = g/cm3
  Dvalue = 21.45
  Group = -> [Pt_element001]
  conduct = 2
  density = 1
  expand = 3
  formula = Pt
  name = G4_Pt
  specific = 4
FEATURE [App::DocumentObjectGroupPython] Au_element001  label="Au_element : 1"  # scripted group (container) (typed FeaturePython)
  n = 1
  ref = Au_element
FEATURE [App::DocumentObjectGroupPython] G4_Au  # scripted group (container) (typed FeaturePython)
  Dunit = g/cm3
  Dvalue = 19.32
  Group = -> [Au_element001]
  conduct = 2
  density = 1
  expand = 3
  formula = Au
  name = G4_Au
  specific = 4
FEATURE [App::DocumentObjectGroupPython] Hg_element002  label="Hg_element : 002"  # scripted group (container) (typed FeaturePython)
  n = 1
  ref = Hg_element
FEATURE [App::DocumentObjectGroupPython] G4_Hg  # scripted group (container) (typed FeaturePython)
  Dunit = g/cm3
  Dvalue = 13.546
  Group = -> [Hg_element002]
  conduct = 2
  density = 1
  expand = 3
  formula = Hg
  name = G4_Hg
  specific = 4
FEATURE [App::DocumentObjectGroupPython] Tl_element002  label="Tl_element : 002"  # scripted group (container) (typed FeaturePython)
  n = 1
  ref = Tl_element
FEATURE [App::DocumentObjectGroupPython] G4_Tl  # scripted group (container) (typed FeaturePython)
  Dunit = g/cm3
  Dvalue = 11.72
  Group = -> [Tl_element002]
  conduct = 2
  density = 1
  expand = 3
  formula = Tl
  name = G4_Tl
  specific = 4
FEATURE [App::DocumentObjectGroupPython] Pb_element003  label="Pb_element : 1"  # scripted group (container) (typed FeaturePython)
  n = 1
  ref = Pb_element
FEATURE [App::DocumentObjectGroupPython] G4_Pb  # scripted group (container) (typed FeaturePython)
  Dunit = g/cm3
  Dvalue = 11.35
  Group = -> [Pb_element003]
  conduct = 2
  density = 1
  expand = 3
  formula = Pb
  name = G4_Pb
  specific = 4
FEATURE [App::DocumentObjectGroupPython] Bi_element002  label="Bi_element : 1"  # scripted group (container) (typed FeaturePython)
  n = 1
  ref = Bi_element
FEATURE [App::DocumentObjectGroupPython] G4_Bi  # scripted group (container) (typed FeaturePython)
  Dunit = g/cm3
  Dvalue = 9.747
  Group = -> [Bi_element002]
  conduct = 2
  density = 1
  expand = 3
  formula = Bi
  name = G4_Bi
  specific = 4
FEATURE [App::DocumentObjectGroupPython] Po_element001  label="Po_element : 1"  # scripted group (container) (typed FeaturePython)
  n = 1
  ref = Po_element
FEATURE [App::DocumentObjectGroupPython] G4_Po  # scripted group (container) (typed FeaturePython)
  Dunit = g/cm3
  Dvalue = 9.32
  Group = -> [Po_element001]
  conduct = 2
  density = 1
  expand = 3
  formula = Po
  name = G4_Po
  specific = 4
FEATURE [App::DocumentObjectGroupPython] At_element001  label="At_element : 1"  # scripted group (container) (typed FeaturePython)
  n = 1
  ref = At_element
FEATURE [App::DocumentObjectGroupPython] G4_At  # scripted group (container) (typed FeaturePython)
  Dunit = g/cm3
  Dvalue = 9.32
  Group = -> [At_element001]
  conduct = 2
  density = 1
  expand = 3
  formula = At
  name = G4_At
  specific = 4
FEATURE [App::DocumentObjectGroupPython] Rn_element001  label="Rn_element : 1"  # scripted group (container) (typed FeaturePython)
  n = 1
  ref = Rn_element
FEATURE [App::DocumentObjectGroupPython] G4_Rn  # scripted group (container) (typed FeaturePython)
  Dunit = g/cm3
  Dvalue = 0.00900662
  Group = -> [Rn_element001]
  conduct = 2
  density = 1
  expand = 3
  formula = Rn
  name = G4_Rn
  specific = 4
FEATURE [App::DocumentObjectGroupPython] Fr_element001  label="Fr_element : 1"  # scripted group (container) (typed FeaturePython)
  n = 1
  ref = Fr_element
FEATURE [App::DocumentObjectGroupPython] G4_Fr  # scripted group (container) (typed FeaturePython)
  Dunit = g/cm3
  Dvalue = 1
  Group = -> [Fr_element001]
  conduct = 2
  density = 1
  expand = 3
  formula = Fr
  name = G4_Fr
  specific = 4
FEATURE [App::DocumentObjectGroupPython] Ra_element001  label="Ra_element : 1"  # scripted group (container) (typed FeaturePython)
  n = 1
  ref = Ra_element
FEATURE [App::DocumentObjectGroupPython] G4_Ra  # scripted group (container) (typed FeaturePython)
  Dunit = g/cm3
  Dvalue = 5
  Group = -> [Ra_element001]
  conduct = 2
  density = 1
  expand = 3
  formula = Ra
  name = G4_Ra
  specific = 4
FEATURE [App::DocumentObjectGroupPython] Ac_element001  label="Ac_element : 1"  # scripted group (container) (typed FeaturePython)
  n = 1
  ref = Ac_element
FEATURE [App::DocumentObjectGroupPython] G4_Ac  # scripted group (container) (typed FeaturePython)
  Dunit = g/cm3
  Dvalue = 10.07
  Group = -> [Ac_element001]
  conduct = 2
  density = 1
  expand = 3
  formula = Ac
  name = G4_Ac
  specific = 4
FEATURE [App::DocumentObjectGroupPython] Th_element001  label="Th_element : 1"  # scripted group (container) (typed FeaturePython)
  n = 1
  ref = Th_element
FEATURE [App::DocumentObjectGroupPython] G4_Th  # scripted group (container) (typed FeaturePython)
  Dunit = g/cm3
  Dvalue = 11.72
  Group = -> [Th_element001]
  conduct = 2
  density = 1
  expand = 3
  formula = Th
  name = G4_Th
  specific = 4
FEATURE [App::DocumentObjectGroupPython] Pa_element001  label="Pa_element : 1"  # scripted group (container) (typed FeaturePython)
  n = 1
  ref = Pa_element
FEATURE [App::DocumentObjectGroupPython] G4_Pa  # scripted group (container) (typed FeaturePython)
  Dunit = g/cm3
  Dvalue = 15.37
  Group = -> [Pa_element001]
  conduct = 2
  density = 1
  expand = 3
  formula = Pa
  name = G4_Pa
  specific = 4
FEATURE [App::DocumentObjectGroupPython] U_element004  label="U_element : 004"  # scripted group (container) (typed FeaturePython)
  n = 1
  ref = U_element
FEATURE [App::DocumentObjectGroupPython] G4_U  # scripted group (container) (typed FeaturePython)
  Dunit = g/cm3
  Dvalue = 18.95
  Group = -> [U_element004]
  conduct = 2
  density = 1
  expand = 3
  formula = U
  name = G4_U
  specific = 4
FEATURE [App::DocumentObjectGroupPython] Np_element001  label="Np_element : 1"  # scripted group (container) (typed FeaturePython)
  n = 1
  ref = Np_element
FEATURE [App::DocumentObjectGroupPython] G4_Np  # scripted group (container) (typed FeaturePython)
  Dunit = g/cm3
  Dvalue = 20.25
  Group = -> [Np_element001]
  conduct = 2
  density = 1
  expand = 3
  formula = Np
  name = G4_Np
  specific = 4
FEATURE [App::DocumentObjectGroupPython] Pu_element002  label="Pu_element : 002"  # scripted group (container) (typed FeaturePython)
  n = 1
  ref = Pu_element
FEATURE [App::DocumentObjectGroupPython] G4_Pu  # scripted group (container) (typed FeaturePython)
  Dunit = g/cm3
  Dvalue = 19.84
  Group = -> [Pu_element002]
  conduct = 2
  density = 1
  expand = 3
  formula = Pu
  name = G4_Pu
  specific = 4
FEATURE [App::DocumentObjectGroupPython] Am_element001  label="Am_element : 1"  # scripted group (container) (typed FeaturePython)
  n = 1
  ref = Am_element
FEATURE [App::DocumentObjectGroupPython] G4_Am  # scripted group (container) (typed FeaturePython)
  Dunit = g/cm3
  Dvalue = 13.67
  Group = -> [Am_element001]
  conduct = 2
  density = 1
  expand = 3
  formula = Am
  name = G4_Am
  specific = 4
FEATURE [App::DocumentObjectGroupPython] Cm_element001  label="Cm_element : 1"  # scripted group (container) (typed FeaturePython)
  n = 1
  ref = Cm_element
FEATURE [App::DocumentObjectGroupPython] G4_Cm  # scripted group (container) (typed FeaturePython)
  Dunit = g/cm3
  Dvalue = 13.51
  Group = -> [Cm_element001]
  conduct = 2
  density = 1
  expand = 3
  formula = Cm
  name = G4_Cm
  specific = 4
FEATURE [App::DocumentObjectGroupPython] Bk_element001  label="Bk_element : 1"  # scripted group (container) (typed FeaturePython)
  n = 1
  ref = Bk_element
FEATURE [App::DocumentObjectGroupPython] G4_Bk  # scripted group (container) (typed FeaturePython)
  Dunit = g/cm3
  Dvalue = 14
  Group = -> [Bk_element001]
  conduct = 2
  density = 1
  expand = 3
  formula = Bk
  name = G4_Bk
  specific = 4
FEATURE [App::DocumentObjectGroupPython] Cf_element001  label="Cf_element : 1"  # scripted group (container) (typed FeaturePython)
  n = 1
  ref = Cf_element
FEATURE [App::DocumentObjectGroupPython] G4_Cf  # scripted group (container) (typed FeaturePython)
  Dunit = g/cm3
  Dvalue = 10
  Group = -> [Cf_element001]
  conduct = 2
  density = 1
  expand = 3
  formula = Cf
  name = G4_Cf
  specific = 4
FEATURE [App::DocumentObjectGroupPython] Element  # scripted group (container) (typed FeaturePython)
  Group = -> [G4_H,G4_He,G4_Li,G4_Be,G4_B,G4_C,G4_N,G4_O,G4_F,G4_Ne,G4_Na,G4_Mg,G4_Al,G4_Si,G4_P,G4_S,G4_Cl,G4_Ar,G4_K,G4_Ca,G4_Sc,G4_Ti,G4_V,G4_Cr,G4_Mn,G4_Fe,G4_Co,G4_Ni,G4_Cu,G4_Zn,G4_Ga,G4_Ge,G4_As,G4_Se,G4_Br,G4_Kr,G4_Rb,G4_Sr,G4_Y,G4_Zr,G4_Nb,G4_Mo,G4_Tc,G4_Ru,G4_Rh,G4_Pd,G4_Ag,G4_Cd,G4_In,G4_Sn,G4_Sb,G4_Te,G4_I,G4_Xe,G4_Cs,G4_Ba,G4_La,G4_Ce,G4_Pr,G4_Nd,G4_Pm,G4_Sm,G4_Eu,G4_Gd,G4_Tb,G4_Dy,G4_Ho,G4_Er,+30 more]
FEATURE [App::DocumentObjectGroupPython] H_element114  label="H_element : 063"  # scripted group (container) (typed FeaturePython)
  n = 2
  ref = H_element
FEATURE [App::DocumentObjectGroupPython] G4_lH2  # scripted group (container) (typed FeaturePython)
  Dunit = g/cm3
  Dvalue = 0.0708
  Group = -> [H_element114]
  conduct = 2
  density = 1
  expand = 3
  formula = G4_lH2
  name = G4_lH2
  specific = 4
FEATURE [App::DocumentObjectGroupPython] N_element049  label="N_element : 022"  # scripted group (container) (typed FeaturePython)
  n = 2
  ref = N_element
FEATURE [App::DocumentObjectGroupPython] G4_lN2  # scripted group (container) (typed FeaturePython)
  Dunit = g/cm3
  Dvalue = 0.807
  Group = -> [N_element049]
  conduct = 2
  density = 1
  expand = 3
  formula = G4_lN2
  name = G4_lN2
  specific = 4
FEATURE [App::DocumentObjectGroupPython] O_element106  label="O_element : 060"  # scripted group (container) (typed FeaturePython)
  n = 2
  ref = O_element
FEATURE [App::DocumentObjectGroupPython] G4_lO2  # scripted group (container) (typed FeaturePython)
  Dunit = g/cm3
  Dvalue = 1.141
  Group = -> [O_element106]
  conduct = 2
  density = 1
  expand = 3
  formula = G4_lO2
  name = G4_lO2
  specific = 4
FEATURE [App::DocumentObjectGroupPython] Ar  label="Ar : 1"  # scripted group (container) (typed FeaturePython)
  n = 1
  ref = Ar
FEATURE [App::DocumentObjectGroupPython] G4_lAr  # scripted group (container) (typed FeaturePython)
  Dunit = g/cm3
  Dvalue = 1.396
  Group = -> [Ar]
  conduct = 2
  density = 1
  expand = 3
  formula = G4_lAr
  name = G4_lAr
  specific = 4
FEATURE [App::DocumentObjectGroupPython] Br  label="Br : 1"  # scripted group (container) (typed FeaturePython)
  n = 1
  ref = Br
FEATURE [App::DocumentObjectGroupPython] G4_lBr  # scripted group (container) (typed FeaturePython)
  Dunit = g/cm3
  Dvalue = 3.1028
  Group = -> [Br]
  conduct = 2
  density = 1
  expand = 3
  formula = G4_lBr
  name = G4_lBr
  specific = 4
FEATURE [App::DocumentObjectGroupPython] Kr  label="Kr : 1"  # scripted group (container) (typed FeaturePython)
  n = 1
  ref = Kr
FEATURE [App::DocumentObjectGroupPython] G4_lKr  # scripted group (container) (typed FeaturePython)
  Dunit = g/cm3
  Dvalue = 2.418
  Group = -> [Kr]
  conduct = 2
  density = 1
  expand = 3
  formula = G4_lKr
  name = G4_lKr
  specific = 4
FEATURE [App::DocumentObjectGroupPython] Xe  label="Xe : 1"  # scripted group (container) (typed FeaturePython)
  n = 1
  ref = Xe
FEATURE [App::DocumentObjectGroupPython] G4_lXe  # scripted group (container) (typed FeaturePython)
  Dunit = g/cm3
  Dvalue = 2.953
  Group = -> [Xe]
  conduct = 2
  density = 1
  expand = 3
  formula = G4_lXe
  name = G4_lXe
  specific = 4
FEATURE [App::DocumentObjectGroupPython] O_element107  label="O_element : 061"  # scripted group (container) (typed FeaturePython)
  n = 4
  ref = O_element
FEATURE [App::DocumentObjectGroupPython] Pb_element004  label="Pb_element : 002"  # scripted group (container) (typed FeaturePython)
  n = 1
  ref = Pb_element
FEATURE [App::DocumentObjectGroupPython] W_element005  label="W_element : 005"  # scripted group (container) (typed FeaturePython)
  n = 1
  ref = W_element
FEATURE [App::DocumentObjectGroupPython] G4_PbWO4  # scripted group (container) (typed FeaturePython)
  Dunit = g/cm3
  Dvalue = 8.28
  Group = -> [O_element107,Pb_element004,W_element005]
  conduct = 2
  density = 1
  expand = 3
  formula = G4_PbWO4
  name = G4_PbWO4
  specific = 4
FEATURE [App::DocumentObjectGroupPython] alactic  label="alactic : 1"  # scripted group (container) (typed FeaturePython)
  n = 1
  ref = alactic
FEATURE [App::DocumentObjectGroupPython] G4_Galactic  # scripted group (container) (typed FeaturePython)
  Dunit = g/cm3
  Dvalue = 0
  Group = -> [alactic]
  conduct = 2
  density = 1
  expand = 3
  formula = G4_Galactic
  name = G4_Galactic
  specific = 4
FEATURE [App::DocumentObjectGroupPython] RAPHITE_POROUS  label="RAPHITE_POROUS : 1"  # scripted group (container) (typed FeaturePython)
  n = 1
  ref = RAPHITE_POROUS
FEATURE [App::DocumentObjectGroupPython] G4_GRAPHITE_POROUS  # scripted group (container) (typed FeaturePython)
  Dunit = g/cm3
  Dvalue = 1.7
  Group = -> [RAPHITE_POROUS]
  conduct = 2
  density = 1
  expand = 3
  formula = G4_GRAPHITE_POROUS
  name = G4_GRAPHITE_POROUS
  specific = 4
FEATURE [App::DocumentObjectGroupPython] H_element115  label="H_element : 0.150"  # scripted group (container) (typed FeaturePython)
  n = 0.080538
FEATURE [App::DocumentObjectGroupPython] C_element125  label="C_element : 0.600"  # scripted group (container) (typed FeaturePython)
  n = 0.599848
FEATURE [App::DocumentObjectGroupPython] O_element108  label="O_element : 0.320"  # scripted group (container) (typed FeaturePython)
  n = 0.319614
FEATURE [App::DocumentObjectGroupPython] G4_LUCITE  # scripted group (container) (typed FeaturePython)
  Dunit = g/cm3
  Dvalue = 1.19
  Group = -> [H_element115,C_element125,O_element108]
  conduct = 2
  density = 1
  expand = 3
  formula = G4_LUCITE
  name = G4_LUCITE
  specific = 4
FEATURE [App::DocumentObjectGroupPython] Cu_element002  label="Cu_element : 62"  # scripted group (container) (typed FeaturePython)
  n = 62
  ref = Cu_element
FEATURE [App::DocumentObjectGroupPython] Zn_element002  label="Zn_element : 35"  # scripted group (container) (typed FeaturePython)
  n = 35
  ref = Zn_element
FEATURE [App::DocumentObjectGroupPython] Pb_element005  label="Pb_element : 3"  # scripted group (container) (typed FeaturePython)
  n = 3
  ref = Pb_element
FEATURE [App::DocumentObjectGroupPython] G4_BRASS  # scripted group (container) (typed FeaturePython)
  Dunit = g/cm3
  Dvalue = 8.52
  Group = -> [Cu_element002,Zn_element002,Pb_element005]
  conduct = 2
  density = 1
  expand = 3
  formula = G4_BRASS
  name = G4_BRASS
  specific = 4
FEATURE [App::DocumentObjectGroupPython] Cu_element003  label="Cu_element : 89"  # scripted group (container) (typed FeaturePython)
  n = 89
  ref = Cu_element
FEATURE [App::DocumentObjectGroupPython] Zn_element003  label="Zn_element : 9"  # scripted group (container) (typed FeaturePython)
  n = 9
  ref = Zn_element
FEATURE [App::DocumentObjectGroupPython] Pb_element006  label="Pb_element : 2"  # scripted group (container) (typed FeaturePython)
  n = 2
  ref = Pb_element
FEATURE [App::DocumentObjectGroupPython] G4_BRONZE  # scripted group (container) (typed FeaturePython)
  Dunit = g/cm3
  Dvalue = 8.82
  Group = -> [Cu_element003,Zn_element003,Pb_element006]
  conduct = 2
  density = 1
  expand = 3
  formula = G4_BRONZE
  name = G4_BRONZE
  specific = 4
FEATURE [App::DocumentObjectGroupPython] Fe_element008  label="Fe_element : 74"  # scripted group (container) (typed FeaturePython)
  n = 74
  ref = Fe_element
FEATURE [App::DocumentObjectGroupPython] Cr_element002  label="Cr_element : 18"  # scripted group (container) (typed FeaturePython)
  n = 18
  ref = Cr_element
FEATURE [App::DocumentObjectGroupPython] Ni_element002  label="Ni_element : 8"  # scripted group (container) (typed FeaturePython)
  n = 8
  ref = Ni_element
FEATURE [App::DocumentObjectGroupPython] G4_STAINLESS_STEEL  label="G4_STAINLESS-STEEL"  # scripted group (container) (typed FeaturePython)
  Dunit = g/cm3
  Dvalue = 8
  Group = -> [Fe_element008,Cr_element002,Ni_element002]
  conduct = 2
  density = 1
  expand = 3
  formula = G4_STAINLESS-STEEL
  name = G4_STAINLESS-STEEL
  specific = 4
FEATURE [App::DocumentObjectGroupPython] H_element116  label="H_element : 064"  # scripted group (container) (typed FeaturePython)
  n = 18
  ref = H_element
FEATURE [App::DocumentObjectGroupPython] C_element126  label="C_element : 071"  # scripted group (container) (typed FeaturePython)
  n = 12
  ref = C_element
FEATURE [App::DocumentObjectGroupPython] O_element109  label="O_element : 062"  # scripted group (container) (typed FeaturePython)
  n = 7
  ref = O_element
FEATURE [App::DocumentObjectGroupPython] G4_CR39  # scripted group (container) (typed FeaturePython)
  Dunit = g/cm3
  Dvalue = 1.32
  Group = -> [H_element116,C_element126,O_element109]
  conduct = 2
  density = 1
  expand = 3
  formula = G4_CR39
  name = G4_CR39
  specific = 4
FEATURE [App::DocumentObjectGroupPython] H_element117  label="H_element : 38"  # scripted group (container) (typed FeaturePython)
  n = 38
  ref = H_element
FEATURE [App::DocumentObjectGroupPython] C_element127  label="C_element : 072"  # scripted group (container) (typed FeaturePython)
  n = 18
  ref = C_element
FEATURE [App::DocumentObjectGroupPython] O_element110  label="O_element : 063"  # scripted group (container) (typed FeaturePython)
  n = 1
  ref = O_element
FEATURE [App::DocumentObjectGroupPython] G4_OCTADECANOL  # scripted group (container) (typed FeaturePython)
  Dunit = g/cm3
  Dvalue = 0.812
  Group = -> [H_element117,C_element127,O_element110]
  conduct = 2
  density = 1
  expand = 3
  formula = G4_OCTADECANOL
  name = G4_OCTADECANOL
  specific = 4
FEATURE [App::DocumentObjectGroupPython] HEP  # scripted group (container) (typed FeaturePython)
  Group = -> [G4_lH2,G4_lN2,G4_lO2,G4_lAr,G4_lBr,G4_lKr,G4_lXe,G4_PbWO4,G4_Galactic,G4_GRAPHITE_POROUS,G4_LUCITE,G4_BRASS,G4_BRONZE,G4_STAINLESS_STEEL,G4_CR39,G4_OCTADECANOL]
FEATURE [App::DocumentObjectGroupPython] C_element128  label="C_element : 073"  # scripted group (container) (typed FeaturePython)
  n = 14
  ref = C_element
FEATURE [App::DocumentObjectGroupPython] H_element118  label="H_element : 065"  # scripted group (container) (typed FeaturePython)
  n = 10
  ref = H_element
FEATURE [App::DocumentObjectGroupPython] O_element111  label="O_element : 064"  # scripted group (container) (typed FeaturePython)
  n = 2
  ref = O_element
FEATURE [App::DocumentObjectGroupPython] N_element050  label="N_element : 023"  # scripted group (container) (typed FeaturePython)
  n = 2
  ref = N_element
FEATURE [App::DocumentObjectGroupPython] G4_KEVLAR  # scripted group (container) (typed FeaturePython)
  Dunit = g/cm3
  Dvalue = 1.44
  Group = -> [C_element128,H_element118,O_element111,N_element050]
  conduct = 2
  density = 1
  expand = 3
  formula = G4_KEVLAR
  name = G4_KEVLAR
  specific = 4
FEATURE [App::DocumentObjectGroupPython] C_element129  label="C_element : 074"  # scripted group (container) (typed FeaturePython)
  n = 10
  ref = C_element
FEATURE [App::DocumentObjectGroupPython] H_element119  label="H_element : 066"  # scripted group (container) (typed FeaturePython)
  n = 8
  ref = H_element
FEATURE [App::DocumentObjectGroupPython] O_element112  label="O_element : 065"  # scripted group (container) (typed FeaturePython)
  n = 4
  ref = O_element
FEATURE [App::DocumentObjectGroupPython] G4_DACRON  # scripted group (container) (typed FeaturePython)
  Dunit = g/cm3
  Dvalue = 1.4
  Group = -> [C_element129,H_element119,O_element112]
  conduct = 2
  density = 1
  expand = 3
  formula = G4_DACRON
  name = G4_DACRON
  specific = 4
FEATURE [App::DocumentObjectGroupPython] C_element130  label="C_element : 075"  # scripted group (container) (typed FeaturePython)
  n = 4
  ref = C_element
FEATURE [App::DocumentObjectGroupPython] H_element120  label="H_element : 067"  # scripted group (container) (typed FeaturePython)
  n = 5
  ref = H_element
FEATURE [App::DocumentObjectGroupPython] Cl_element030  label="Cl_element : 016"  # scripted group (container) (typed FeaturePython)
  n = 1
  ref = Cl_element
FEATURE [App::DocumentObjectGroupPython] G4_NEOPRENE  # scripted group (container) (typed FeaturePython)
  Dunit = g/cm3
  Dvalue = 1.23
  Group = -> [C_element130,H_element120,Cl_element030]
  conduct = 2
  density = 1
  expand = 3
  formula = G4_NEOPRENE
  name = G4_NEOPRENE
  specific = 4
FEATURE [App::DocumentObjectGroupPython] Space  # scripted group (container) (typed FeaturePython)
  Group = -> [G4_KEVLAR,G4_DACRON,G4_NEOPRENE]
FEATURE [App::DocumentObjectGroupPython] H_element121  label="H_element : 068"  # scripted group (container) (typed FeaturePython)
  n = 5
  ref = H_element
FEATURE [App::DocumentObjectGroupPython] C_element131  label="C_element : 076"  # scripted group (container) (typed FeaturePython)
  n = 4
  ref = C_element
FEATURE [App::DocumentObjectGroupPython] N_element051  label="N_element : 3"  # scripted group (container) (typed FeaturePython)
  n = 3
  ref = N_element
FEATURE [App::DocumentObjectGroupPython] O_element113  label="O_element : 066"  # scripted group (container) (typed FeaturePython)
  n = 1
  ref = O_element
FEATURE [App::DocumentObjectGroupPython] G4_CYTOSINE  # scripted group (container) (typed FeaturePython)
  Dunit = g/cm3
  Dvalue = 1.55
  Group = -> [H_element121,C_element131,N_element051,O_element113]
  conduct = 2
  density = 1
  expand = 3
  formula = G4_CYTOSINE
  name = G4_CYTOSINE
  specific = 4
FEATURE [App::DocumentObjectGroupPython] H_element122  label="H_element : 069"  # scripted group (container) (typed FeaturePython)
  n = 6
  ref = H_element
FEATURE [App::DocumentObjectGroupPython] C_element132  label="C_element : 077"  # scripted group (container) (typed FeaturePython)
  n = 5
  ref = C_element
FEATURE [App::DocumentObjectGroupPython] N_element052  label="N_element : 024"  # scripted group (container) (typed FeaturePython)
  n = 2
  ref = N_element
FEATURE [App::DocumentObjectGroupPython] O_element114  label="O_element : 067"  # scripted group (container) (typed FeaturePython)
  n = 2
  ref = O_element
FEATURE [App::DocumentObjectGroupPython] G4_THYMINE  # scripted group (container) (typed FeaturePython)
  Dunit = g/cm3
  Dvalue = 1.23
  Group = -> [H_element122,C_element132,N_element052,O_element114]
  conduct = 2
  density = 1
  expand = 3
  formula = G4_THYMINE
  name = G4_THYMINE
  specific = 4
FEATURE [App::DocumentObjectGroupPython] H_element123  label="H_element : 070"  # scripted group (container) (typed FeaturePython)
  n = 4
  ref = H_element
FEATURE [App::DocumentObjectGroupPython] C_element133  label="C_element : 078"  # scripted group (container) (typed FeaturePython)
  n = 4
  ref = C_element
FEATURE [App::DocumentObjectGroupPython] N_element053  label="N_element : 025"  # scripted group (container) (typed FeaturePython)
  n = 2
  ref = N_element
FEATURE [App::DocumentObjectGroupPython] O_element115  label="O_element : 068"  # scripted group (container) (typed FeaturePython)
  n = 2
  ref = O_element
FEATURE [App::DocumentObjectGroupPython] G4_URACIL  # scripted group (container) (typed FeaturePython)
  Dunit = g/cm3
  Dvalue = 1.32
  Group = -> [H_element123,C_element133,N_element053,O_element115]
  conduct = 2
  density = 1
  expand = 3
  formula = G4_URACIL
  name = G4_URACIL
  specific = 4
FEATURE [App::DocumentObjectGroupPython] H_element124  label="H_element : 071"  # scripted group (container) (typed FeaturePython)
  n = 4
  ref = H_element
FEATURE [App::DocumentObjectGroupPython] C_element134  label="C_element : 079"  # scripted group (container) (typed FeaturePython)
  n = 5
  ref = C_element
FEATURE [App::DocumentObjectGroupPython] N_element054  label="N_element : 026"  # scripted group (container) (typed FeaturePython)
  n = 5
  ref = N_element
FEATURE [App::DocumentObjectGroupPython] G4_DNA_ADENINE  # scripted group (container) (typed FeaturePython)
  Dunit = g/cm3
  Dvalue = 1
  Group = -> [H_element124,C_element134,N_element054]
  conduct = 2
  density = 1
  expand = 3
  formula = G4_DNA_ADENINE
  name = G4_DNA_ADENINE
  specific = 4
FEATURE [App::DocumentObjectGroupPython] H_element125  label="H_element : 072"  # scripted group (container) (typed FeaturePython)
  n = 4
  ref = H_element
FEATURE [App::DocumentObjectGroupPython] C_element135  label="C_element : 080"  # scripted group (container) (typed FeaturePython)
  n = 5
  ref = C_element
FEATURE [App::DocumentObjectGroupPython] N_element055  label="N_element : 027"  # scripted group (container) (typed FeaturePython)
  n = 5
  ref = N_element
FEATURE [App::DocumentObjectGroupPython] O_element116  label="O_element : 069"  # scripted group (container) (typed FeaturePython)
  n = 1
  ref = O_element
FEATURE [App::DocumentObjectGroupPython] G4_DNA_GUANINE  # scripted group (container) (typed FeaturePython)
  Dunit = g/cm3
  Dvalue = 1
  Group = -> [H_element125,C_element135,N_element055,O_element116]
  conduct = 2
  density = 1
  expand = 3
  formula = G4_DNA_GUANINE
  name = G4_DNA_GUANINE
  specific = 4
FEATURE [App::DocumentObjectGroupPython] H_element126  label="H_element : 073"  # scripted group (container) (typed FeaturePython)
  n = 4
  ref = H_element
FEATURE [App::DocumentObjectGroupPython] C_element136  label="C_element : 081"  # scripted group (container) (typed FeaturePython)
  n = 4
  ref = C_element
FEATURE [App::DocumentObjectGroupPython] N_element056  label="N_element : 028"  # scripted group (container) (typed FeaturePython)
  n = 3
  ref = N_element
FEATURE [App::DocumentObjectGroupPython] O_element117  label="O_element : 070"  # scripted group (container) (typed FeaturePython)
  n = 1
  ref = O_element
FEATURE [App::DocumentObjectGroupPython] G4_DNA_CYTOSINE  # scripted group (container) (typed FeaturePython)
  Dunit = g/cm3
  Dvalue = 1
  Group = -> [H_element126,C_element136,N_element056,O_element117]
  conduct = 2
  density = 1
  expand = 3
  formula = G4_DNA_CYTOSINE
  name = G4_DNA_CYTOSINE
  specific = 4
FEATURE [App::DocumentObjectGroupPython] H_element127  label="H_element : 074"  # scripted group (container) (typed FeaturePython)
  n = 5
  ref = H_element
FEATURE [App::DocumentObjectGroupPython] C_element137  label="C_element : 082"  # scripted group (container) (typed FeaturePython)
  n = 5
  ref = C_element
FEATURE [App::DocumentObjectGroupPython] N_element057  label="N_element : 029"  # scripted group (container) (typed FeaturePython)
  n = 2
  ref = N_element
FEATURE [App::DocumentObjectGroupPython] O_element118  label="O_element : 071"  # scripted group (container) (typed FeaturePython)
  n = 2
  ref = O_element
FEATURE [App::DocumentObjectGroupPython] G4_DNA_THYMINE  # scripted group (container) (typed FeaturePython)
  Dunit = g/cm3
  Dvalue = 1
  Group = -> [H_element127,C_element137,N_element057,O_element118]
  conduct = 2
  density = 1
  expand = 3
  formula = G4_DNA_THYMINE
  name = G4_DNA_THYMINE
  specific = 4
FEATURE [App::DocumentObjectGroupPython] H_element128  label="H_element : 075"  # scripted group (container) (typed FeaturePython)
  n = 3
  ref = H_element
FEATURE [App::DocumentObjectGroupPython] C_element138  label="C_element : 083"  # scripted group (container) (typed FeaturePython)
  n = 4
  ref = C_element
FEATURE [App::DocumentObjectGroupPython] N_element058  label="N_element : 030"  # scripted group (container) (typed FeaturePython)
  n = 2
  ref = N_element
FEATURE [App::DocumentObjectGroupPython] O_element119  label="O_element : 072"  # scripted group (container) (typed FeaturePython)
  n = 2
  ref = O_element
FEATURE [App::DocumentObjectGroupPython] G4_DNA_URACIL  # scripted group (container) (typed FeaturePython)
  Dunit = g/cm3
  Dvalue = 1
  Group = -> [H_element128,C_element138,N_element058,O_element119]
  conduct = 2
  density = 1
  expand = 3
  formula = G4_DNA_URACIL
  name = G4_DNA_URACIL
  specific = 4
FEATURE [App::DocumentObjectGroupPython] H_element129  label="H_element : 076"  # scripted group (container) (typed FeaturePython)
  n = 10
  ref = H_element
FEATURE [App::DocumentObjectGroupPython] C_element139  label="C_element : 084"  # scripted group (container) (typed FeaturePython)
  n = 10
  ref = C_element
FEATURE [App::DocumentObjectGroupPython] N_element059  label="N_element : 031"  # scripted group (container) (typed FeaturePython)
  n = 5
  ref = N_element
FEATURE [App::DocumentObjectGroupPython] O_element120  label="O_element : 073"  # scripted group (container) (typed FeaturePython)
  n = 4
  ref = O_element
FEATURE [App::DocumentObjectGroupPython] G4_DNA_ADENOSINE  # scripted group (container) (typed FeaturePython)
  Dunit = g/cm3
  Dvalue = 1
  Group = -> [H_element129,C_element139,N_element059,O_element120]
  conduct = 2
  density = 1
  expand = 3
  formula = G4_DNA_ADENOSINE
  name = G4_DNA_ADENOSINE
  specific = 4
FEATURE [App::DocumentObjectGroupPython] H_element130  label="H_element : 077"  # scripted group (container) (typed FeaturePython)
  n = 10
  ref = H_element
FEATURE [App::DocumentObjectGroupPython] C_element140  label="C_element : 085"  # scripted group (container) (typed FeaturePython)
  n = 10
  ref = C_element
FEATURE [App::DocumentObjectGroupPython] N_element060  label="N_element : 032"  # scripted group (container) (typed FeaturePython)
  n = 5
  ref = N_element
FEATURE [App::DocumentObjectGroupPython] O_element121  label="O_element : 074"  # scripted group (container) (typed FeaturePython)
  n = 5
  ref = O_element
FEATURE [App::DocumentObjectGroupPython] G4_DNA_GUANOSINE  # scripted group (container) (typed FeaturePython)
  Dunit = g/cm3
  Dvalue = 1
  Group = -> [H_element130,C_element140,N_element060,O_element121]
  conduct = 2
  density = 1
  expand = 3
  formula = G4_DNA_GUANOSINE
  name = G4_DNA_GUANOSINE
  specific = 4
FEATURE [App::DocumentObjectGroupPython] H_element131  label="H_element : 078"  # scripted group (container) (typed FeaturePython)
  n = 10
  ref = H_element
FEATURE [App::DocumentObjectGroupPython] C_element141  label="C_element : 086"  # scripted group (container) (typed FeaturePython)
  n = 9
  ref = C_element
FEATURE [App::DocumentObjectGroupPython] N_element061  label="N_element : 033"  # scripted group (container) (typed FeaturePython)
  n = 3
  ref = N_element
FEATURE [App::DocumentObjectGroupPython] O_element122  label="O_element : 075"  # scripted group (container) (typed FeaturePython)
  n = 5
  ref = O_element
FEATURE [App::DocumentObjectGroupPython] G4_DNA_CYTIDINE  # scripted group (container) (typed FeaturePython)
  Dunit = g/cm3
  Dvalue = 1
  Group = -> [H_element131,C_element141,N_element061,O_element122]
  conduct = 2
  density = 1
  expand = 3
  formula = G4_DNA_CYTIDINE
  name = G4_DNA_CYTIDINE
  specific = 4
FEATURE [App::DocumentObjectGroupPython] H_element132  label="H_element : 079"  # scripted group (container) (typed FeaturePython)
  n = 9
  ref = H_element
FEATURE [App::DocumentObjectGroupPython] C_element142  label="C_element : 087"  # scripted group (container) (typed FeaturePython)
  n = 9
  ref = C_element
FEATURE [App::DocumentObjectGroupPython] N_element062  label="N_element : 034"  # scripted group (container) (typed FeaturePython)
  n = 2
  ref = N_element
FEATURE [App::DocumentObjectGroupPython] O_element123  label="O_element : 076"  # scripted group (container) (typed FeaturePython)
  n = 6
  ref = O_element
FEATURE [App::DocumentObjectGroupPython] G4_DNA_URIDINE  # scripted group (container) (typed FeaturePython)
  Dunit = g/cm3
  Dvalue = 1
  Group = -> [H_element132,C_element142,N_element062,O_element123]
  conduct = 2
  density = 1
  expand = 3
  formula = G4_DNA_URIDINE
  name = G4_DNA_URIDINE
  specific = 4
FEATURE [App::DocumentObjectGroupPython] H_element133  label="H_element : 080"  # scripted group (container) (typed FeaturePython)
  n = 11
  ref = H_element
FEATURE [App::DocumentObjectGroupPython] C_element143  label="C_element : 088"  # scripted group (container) (typed FeaturePython)
  n = 10
  ref = C_element
FEATURE [App::DocumentObjectGroupPython] N_element063  label="N_element : 035"  # scripted group (container) (typed FeaturePython)
  n = 2
  ref = N_element
FEATURE [App::DocumentObjectGroupPython] O_element124  label="O_element : 077"  # scripted group (container) (typed FeaturePython)
  n = 6
  ref = O_element
FEATURE [App::DocumentObjectGroupPython] G4_DNA_METHYLURIDINE  # scripted group (container) (typed FeaturePython)
  Dunit = g/cm3
  Dvalue = 1
  Group = -> [H_element133,C_element143,N_element063,O_element124]
  conduct = 2
  density = 1
  expand = 3
  formula = G4_DNA_METHYLURIDINE
  name = G4_DNA_METHYLURIDINE
  specific = 4
FEATURE [App::DocumentObjectGroupPython] P_element014  label="P_element : 003"  # scripted group (container) (typed FeaturePython)
  n = 1
  ref = P_element
FEATURE [App::DocumentObjectGroupPython] O_element125  label="O_element : 078"  # scripted group (container) (typed FeaturePython)
  n = 3
  ref = O_element
FEATURE [App::DocumentObjectGroupPython] G4_DNA_MONOPHOSPHATE  # scripted group (container) (typed FeaturePython)
  Dunit = g/cm3
  Dvalue = 1
  Group = -> [P_element014,O_element125]
  conduct = 2
  density = 1
  expand = 3
  formula = G4_DNA_MONOPHOSPHATE
  name = G4_DNA_MONOPHOSPHATE
  specific = 4
FEATURE [App::DocumentObjectGroupPython] H_element134  label="H_element : 081"  # scripted group (container) (typed FeaturePython)
  n = 10
  ref = H_element
FEATURE [App::DocumentObjectGroupPython] C_element144  label="C_element : 089"  # scripted group (container) (typed FeaturePython)
  n = 10
  ref = C_element
FEATURE [App::DocumentObjectGroupPython] N_element064  label="N_element : 036"  # scripted group (container) (typed FeaturePython)
  n = 5
  ref = N_element
FEATURE [App::DocumentObjectGroupPython] O_element126  label="O_element : 079"  # scripted group (container) (typed FeaturePython)
  n = 7
  ref = O_element
FEATURE [App::DocumentObjectGroupPython] P_element015  label="P_element : 004"  # scripted group (container) (typed FeaturePython)
  n = 1
  ref = P_element
FEATURE [App::DocumentObjectGroupPython] G4_DNA_A  # scripted group (container) (typed FeaturePython)
  Dunit = g/cm3
  Dvalue = 1
  Group = -> [H_element134,C_element144,N_element064,O_element126,P_element015]
  conduct = 2
  density = 1
  expand = 3
  formula = G4_DNA_A
  name = G4_DNA_A
  specific = 4
FEATURE [App::DocumentObjectGroupPython] H_element135  label="H_element : 082"  # scripted group (container) (typed FeaturePython)
  n = 10
  ref = H_element
FEATURE [App::DocumentObjectGroupPython] C_element145  label="C_element : 090"  # scripted group (container) (typed FeaturePython)
  n = 10
  ref = C_element
FEATURE [App::DocumentObjectGroupPython] N_element065  label="N_element : 037"  # scripted group (container) (typed FeaturePython)
  n = 5
  ref = N_element
FEATURE [App::DocumentObjectGroupPython] O_element127  label="O_element : 8"  # scripted group (container) (typed FeaturePython)
  n = 8
  ref = O_element
FEATURE [App::DocumentObjectGroupPython] P_element016  label="P_element : 005"  # scripted group (container) (typed FeaturePython)
  n = 1
  ref = P_element
FEATURE [App::DocumentObjectGroupPython] G4_DNA_G  # scripted group (container) (typed FeaturePython)
  Dunit = g/cm3
  Dvalue = 1
  Group = -> [H_element135,C_element145,N_element065,O_element127,P_element016]
  conduct = 2
  density = 1
  expand = 3
  formula = G4_DNA_G
  name = G4_DNA_G
  specific = 4
FEATURE [App::DocumentObjectGroupPython] H_element136  label="H_element : 083"  # scripted group (container) (typed FeaturePython)
  n = 10
  ref = H_element
FEATURE [App::DocumentObjectGroupPython] C_element146  label="C_element : 091"  # scripted group (container) (typed FeaturePython)
  n = 9
  ref = C_element
FEATURE [App::DocumentObjectGroupPython] N_element066  label="N_element : 038"  # scripted group (container) (typed FeaturePython)
  n = 3
  ref = N_element
FEATURE [App::DocumentObjectGroupPython] O_element128  label="O_element : 080"  # scripted group (container) (typed FeaturePython)
  n = 8
  ref = O_element
FEATURE [App::DocumentObjectGroupPython] P_element017  label="P_element : 006"  # scripted group (container) (typed FeaturePython)
  n = 1
  ref = P_element
FEATURE [App::DocumentObjectGroupPython] G4_DNA_C  # scripted group (container) (typed FeaturePython)
  Dunit = g/cm3
  Dvalue = 1
  Group = -> [H_element136,C_element146,N_element066,O_element128,P_element017]
  conduct = 2
  density = 1
  expand = 3
  formula = G4_DNA_C
  name = G4_DNA_C
  specific = 4
FEATURE [App::DocumentObjectGroupPython] H_element137  label="H_element : 084"  # scripted group (container) (typed FeaturePython)
  n = 9
  ref = H_element
FEATURE [App::DocumentObjectGroupPython] C_element147  label="C_element : 092"  # scripted group (container) (typed FeaturePython)
  n = 9
  ref = C_element
FEATURE [App::DocumentObjectGroupPython] N_element067  label="N_element : 039"  # scripted group (container) (typed FeaturePython)
  n = 2
  ref = N_element
FEATURE [App::DocumentObjectGroupPython] O_element129  label="O_element : 9"  # scripted group (container) (typed FeaturePython)
  n = 9
  ref = O_element
FEATURE [App::DocumentObjectGroupPython] P_element018  label="P_element : 007"  # scripted group (container) (typed FeaturePython)
  n = 1
  ref = P_element
FEATURE [App::DocumentObjectGroupPython] G4_DNA_U  # scripted group (container) (typed FeaturePython)
  Dunit = g/cm3
  Dvalue = 1
  Group = -> [H_element137,C_element147,N_element067,O_element129,P_element018]
  conduct = 2
  density = 1
  expand = 3
  formula = G4_DNA_U
  name = G4_DNA_U
  specific = 4
FEATURE [App::DocumentObjectGroupPython] H_element138  label="H_element : 085"  # scripted group (container) (typed FeaturePython)
  n = 11
  ref = H_element
FEATURE [App::DocumentObjectGroupPython] C_element148  label="C_element : 093"  # scripted group (container) (typed FeaturePython)
  n = 10
  ref = C_element
FEATURE [App::DocumentObjectGroupPython] N_element068  label="N_element : 040"  # scripted group (container) (typed FeaturePython)
  n = 2
  ref = N_element
FEATURE [App::DocumentObjectGroupPython] O_element130  label="O_element : 081"  # scripted group (container) (typed FeaturePython)
  n = 9
  ref = O_element
FEATURE [App::DocumentObjectGroupPython] P_element019  label="P_element : 008"  # scripted group (container) (typed FeaturePython)
  n = 1
  ref = P_element
FEATURE [App::DocumentObjectGroupPython] G4_DNA_MU  # scripted group (container) (typed FeaturePython)
  Dunit = g/cm3
  Dvalue = 1
  Group = -> [H_element138,C_element148,N_element068,O_element130,P_element019]
  conduct = 2
  density = 1
  expand = 3
  formula = G4_DNA_MU
  name = G4_DNA_MU
  specific = 4
FEATURE [App::DocumentObjectGroupPython] BioChemical  # scripted group (container) (typed FeaturePython)
  Group = -> [G4_CYTOSINE,G4_THYMINE,G4_URACIL,G4_DNA_ADENINE,G4_DNA_GUANINE,G4_DNA_CYTOSINE,G4_DNA_THYMINE,G4_DNA_URACIL,G4_DNA_ADENOSINE,G4_DNA_GUANOSINE,G4_DNA_CYTIDINE,G4_DNA_URIDINE,G4_DNA_METHYLURIDINE,G4_DNA_MONOPHOSPHATE,G4_DNA_A,G4_DNA_G,G4_DNA_C,G4_DNA_U,G4_DNA_MU]
FEATURE [App::DocumentObjectGroupPython] G4Materials  # scripted group (container) (typed FeaturePython)
  Group = -> [NIST,Element,HEP,Space,BioChemical]
  version = 1
FEATURE [App::DocumentObjectGroupPython] Geant4  # scripted group (container) (typed FeaturePython)
  Group = -> [G4Isotopes,G4Elements,G4Materials]
FEATURE [App::DocumentObjectGroupPython] Materials  # scripted group (container) (typed FeaturePython)
  Group = -> [Geant4]
FEATURE [Part::FeaturePython] GDMLBox_WorldBox  # WARN: FeaturePython — macro-defined, semantics opaque (R4)
  lunit = 2
  material = 5
  x = 273
  y = 273
  z = 130
FEATURE [Part::FeaturePython] GDMLBox_Box  # WARN: FeaturePython — macro-defined, semantics opaque (R4)
  lunit = 2
  material = 0
  x = 10
  y = 10
  z = 10
FEATURE [App::Part] LV_Box
  Group = -> [GDMLBox_Box]
  Origin = -> Origin002
FEATURE [Part::FeaturePython] Array  # Draft array (typed FeaturePython)
  AlwaysSyncPlacement = false
  Angle = 360
  ArrayType = 1
  Axis = (0,0,1)
  Base = -> LV_Box
  Center = (0,0,0)
  Count = 5
  ExpandArray = false
  Fuse = false
  IntervalAxis = (0,0,0)
  IntervalX = (100,0,0)
  IntervalY = (0,100,0)
  IntervalZ = (0,0,100)
  NumberCircles = 3
  NumberPolar = 5
  NumberX = 2
  NumberY = 2
  NumberZ = 1
  PlacementList = 5 placements: [(0,0,0),(0,0,0),(0,0,0),(0,0,0),(0,0,0)]
  RadialDistance = 50
  ScaleList = (5) [(1,1,1),(1,1,1),(1,1,1),(1,1,1),(1,1,1)]
  Symmetry = 1
  TangentialDistance = 25
FEATURE [App::Part] Part  label="experiment"
  Group = -> [LV_Box,Array]
  Origin = -> Origin001
FEATURE [App::Part] worldVOL
  Group = -> [GDMLBox_WorldBox,Part]
  Origin = -> Origin
